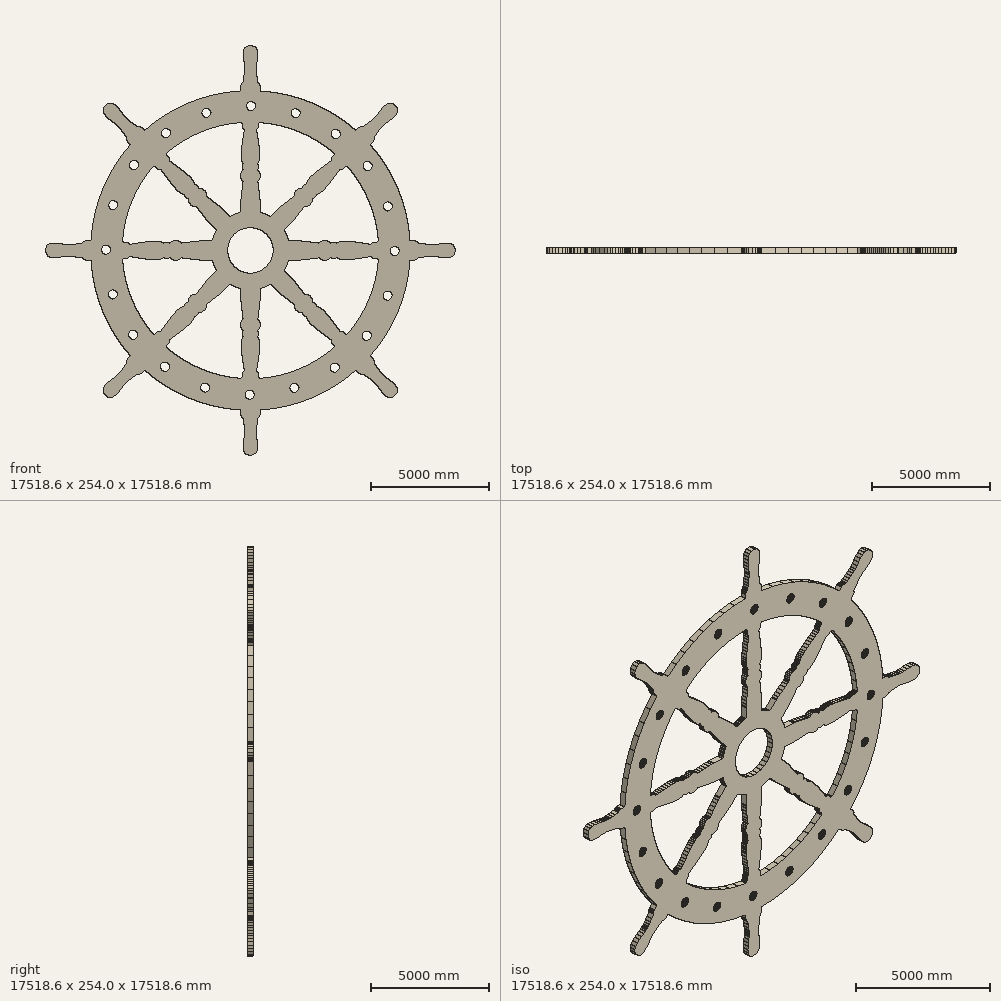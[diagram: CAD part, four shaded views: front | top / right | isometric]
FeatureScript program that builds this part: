
annotation { "Feature Type Name" : "Feature", "Feature Type Description" : "" }
export const myFeature = defineFeature(function(context is Context, id is Id, definition is map)
    precondition{}
    {
        {
            var Q0;
            Q0=qCreatedBy(makeId("Front.planeOp"),FACE);
            var sketch = newSketch(context, id + "F0", { "sketchPlane" : qUnion([Q0])});
            skLineSegment(sketch, "E0", {"start": v(6165.33, -222.67) * mm, "end": v(6126.68, -217.26) * mm});
            skLineSegment(sketch, "E1", {"start": v(6126.68, -217.26) * mm, "end": v(6090.75, -204.87) * mm});
            skLineSegment(sketch, "E2", {"start": v(6090.75, -204.87) * mm, "end": v(6058.31, -186.3) * mm});
            skLineSegment(sketch, "E3", {"start": v(6058.31, -186.3) * mm, "end": v(6030.13, -162.3) * mm});
            skLineSegment(sketch, "E4", {"start": v(6030.13, -162.3) * mm, "end": v(6006.97, -133.67) * mm});
            skLineSegment(sketch, "E5", {"start": v(6006.97, -133.67) * mm, "end": v(5989.6, -101.2) * mm});
            skLineSegment(sketch, "E6", {"start": v(5989.6, -101.2) * mm, "end": v(5978.78, -65.68) * mm});
            skLineSegment(sketch, "E7", {"start": v(5978.78, -65.68) * mm, "end": v(5975.29, -27.88) * mm});
            skLineSegment(sketch, "E8", {"start": v(5975.29, -27.88) * mm, "end": v(5979.97, 9.9) * mm});
            skLineSegment(sketch, "E9", {"start": v(5979.97, 9.9) * mm, "end": v(5991.44, 45.31) * mm});
            skLineSegment(sketch, "E10", {"start": v(5991.44, 45.31) * mm, "end": v(6009.03, 77.59) * mm});
            skLineSegment(sketch, "E11", {"start": v(6009.03, 77.59) * mm, "end": v(6032.1, 105.96) * mm});
            skLineSegment(sketch, "E12", {"start": v(6032.1, 105.96) * mm, "end": v(6060, 129.65) * mm});
            skLineSegment(sketch, "E13", {"start": v(6060, 129.65) * mm, "end": v(6092.04, 147.88) * mm});
            skLineSegment(sketch, "E14", {"start": v(6092.04, 147.88) * mm, "end": v(6127.58, 159.9) * mm});
            skLineSegment(sketch, "E15", {"start": v(6127.58, 159.9) * mm, "end": v(6165.96, 164.9) * mm});
            skLineSegment(sketch, "E16", {"start": v(6165.96, 164.9) * mm, "end": v(6205, 162.05) * mm});
            skLineSegment(sketch, "E17", {"start": v(6205, 162.05) * mm, "end": v(6241.57, 151.48) * mm});
            skLineSegment(sketch, "E18", {"start": v(6241.57, 151.48) * mm, "end": v(6274.8, 134) * mm});
            skLineSegment(sketch, "E19", {"start": v(6274.8, 134) * mm, "end": v(6303.79, 110.38) * mm});
            skLineSegment(sketch, "E20", {"start": v(6303.79, 110.38) * mm, "end": v(6327.65, 81.4) * mm});
            skLineSegment(sketch, "E21", {"start": v(6327.65, 81.4) * mm, "end": v(6345.5, 47.85) * mm});
            skLineSegment(sketch, "E22", {"start": v(6345.5, 47.85) * mm, "end": v(6356.43, 10.5) * mm});
            skLineSegment(sketch, "E23", {"start": v(6356.43, 10.5) * mm, "end": v(6359.56, -29.86) * mm});
            skLineSegment(sketch, "E24", {"start": v(6359.56, -29.86) * mm, "end": v(6355.22, -70.17) * mm});
            skLineSegment(sketch, "E25", {"start": v(6355.22, -70.17) * mm, "end": v(6343.62, -107.4) * mm});
            skLineSegment(sketch, "E26", {"start": v(6343.62, -107.4) * mm, "end": v(6325.54, -140.77) * mm});
            skLineSegment(sketch, "E27", {"start": v(6325.54, -140.77) * mm, "end": v(6301.76, -169.52) * mm});
            skLineSegment(sketch, "E28", {"start": v(6301.76, -169.52) * mm, "end": v(6273.06, -192.85) * mm});
            skLineSegment(sketch, "E29", {"start": v(6273.06, -192.85) * mm, "end": v(6240.24, -210) * mm});
            skLineSegment(sketch, "E30", {"start": v(6240.24, -210) * mm, "end": v(6204.07, -220.2) * mm});
            skLineSegment(sketch, "E31", {"start": v(6204.07, -220.2) * mm, "end": v(6165.33, -222.67) * mm});
            skLineSegment(sketch, "E32", {"start": v(6040.7, -1994.04) * mm, "end": v(6024.87, -2031.33) * mm});
            skLineSegment(sketch, "E33", {"start": v(6024.87, -2031.33) * mm, "end": v(6002.57, -2063.26) * mm});
            skLineSegment(sketch, "E34", {"start": v(6002.57, -2063.26) * mm, "end": v(5974.91, -2089.38) * mm});
            skLineSegment(sketch, "E35", {"start": v(5974.91, -2089.38) * mm, "end": v(5943, -2109.25) * mm});
            skLineSegment(sketch, "E36", {"start": v(5943, -2109.25) * mm, "end": v(5907.94, -2122.4) * mm});
            skLineSegment(sketch, "E37", {"start": v(5907.94, -2122.4) * mm, "end": v(5870.85, -2128.39) * mm});
            skLineSegment(sketch, "E38", {"start": v(5870.85, -2128.39) * mm, "end": v(5832.83, -2126.75) * mm});
            skLineSegment(sketch, "E39", {"start": v(5832.83, -2126.75) * mm, "end": v(5795, -2117.05) * mm});
            skLineSegment(sketch, "E40", {"start": v(5795, -2117.05) * mm, "end": v(5760.14, -2100.05) * mm});
            skLineSegment(sketch, "E41", {"start": v(5760.14, -2100.05) * mm, "end": v(5730.25, -2077.34) * mm});
            skLineSegment(sketch, "E42", {"start": v(5730.25, -2077.34) * mm, "end": v(5705.7, -2049.86) * mm});
            skLineSegment(sketch, "E43", {"start": v(5705.7, -2049.86) * mm, "end": v(5686.86, -2018.55) * mm});
            skLineSegment(sketch, "E44", {"start": v(5686.86, -2018.55) * mm, "end": v(5674.07, -1984.35) * mm});
            skLineSegment(sketch, "E45", {"start": v(5674.07, -1984.35) * mm, "end": v(5667.7, -1948.2) * mm});
            skLineSegment(sketch, "E46", {"start": v(5667.7, -1948.2) * mm, "end": v(5668.14, -1911.01) * mm});
            skLineSegment(sketch, "E47", {"start": v(5668.14, -1911.01) * mm, "end": v(5675.72, -1873.75) * mm});
            skLineSegment(sketch, "E48", {"start": v(5675.72, -1873.75) * mm, "end": v(5691.01, -1839.02) * mm});
            skLineSegment(sketch, "E49", {"start": v(5691.01, -1839.02) * mm, "end": v(5712.57, -1808.8) * mm});
            skLineSegment(sketch, "E50", {"start": v(5712.57, -1808.8) * mm, "end": v(5739.38, -1783.55) * mm});
            skLineSegment(sketch, "E51", {"start": v(5739.38, -1783.55) * mm, "end": v(5770.46, -1763.79) * mm});
            skLineSegment(sketch, "E52", {"start": v(5770.46, -1763.79) * mm, "end": v(5804.81, -1750) * mm});
            skLineSegment(sketch, "E53", {"start": v(5804.81, -1750) * mm, "end": v(5841.44, -1742.66) * mm});
            skLineSegment(sketch, "E54", {"start": v(5841.44, -1742.66) * mm, "end": v(5879.33, -1742.29) * mm});
            skLineSegment(sketch, "E55", {"start": v(5879.33, -1742.29) * mm, "end": v(5917.5, -1749.36) * mm});
            skLineSegment(sketch, "E56", {"start": v(5917.5, -1749.36) * mm, "end": v(5953.66, -1764.05) * mm});
            skLineSegment(sketch, "E57", {"start": v(5953.66, -1764.05) * mm, "end": v(5984.83, -1785.24) * mm});
            skLineSegment(sketch, "E58", {"start": v(5984.83, -1785.24) * mm, "end": v(6010.55, -1811.94) * mm});
            skLineSegment(sketch, "E59", {"start": v(6010.55, -1811.94) * mm, "end": v(6030.34, -1843.18) * mm});
            skLineSegment(sketch, "E60", {"start": v(6030.34, -1843.18) * mm, "end": v(6043.72, -1878) * mm});
            skLineSegment(sketch, "E61", {"start": v(6043.72, -1878) * mm, "end": v(6050.23, -1915.39) * mm});
            skLineSegment(sketch, "E62", {"start": v(6050.23, -1915.39) * mm, "end": v(6049.37, -1954.4) * mm});
            skLineSegment(sketch, "E63", {"start": v(6049.37, -1954.4) * mm, "end": v(6040.7, -1994.04) * mm});
            skLineSegment(sketch, "E64", {"start": v(5397.18, 330.57) * mm, "end": v(5367.67, 344) * mm});
            skLineSegment(sketch, "E65", {"start": v(5367.67, 344) * mm, "end": v(5335.19, 351.84) * mm});
            skLineSegment(sketch, "E66", {"start": v(5335.19, 351.84) * mm, "end": v(5301.14, 353.77) * mm});
            skLineSegment(sketch, "E67", {"start": v(5301.14, 353.77) * mm, "end": v(5266.96, 349.46) * mm});
            skLineSegment(sketch, "E68", {"start": v(5266.96, 349.46) * mm, "end": v(5234.05, 338.56) * mm});
            skLineSegment(sketch, "E69", {"start": v(5234.05, 338.56) * mm, "end": v(5203.85, 320.72) * mm});
            skLineSegment(sketch, "E70", {"start": v(5203.85, 320.72) * mm, "end": v(5177.77, 295.63) * mm});
            skLineSegment(sketch, "E71", {"start": v(5177.77, 295.63) * mm, "end": v(5157.23, 262.93) * mm});
            skLineSegment(sketch, "E72", {"start": v(5157.23, 262.93) * mm, "end": v(5077.23, 273.12) * mm});
            skLineSegment(sketch, "E73", {"start": v(5077.23, 273.12) * mm, "end": v(4981.6, 288) * mm});
            skLineSegment(sketch, "E74", {"start": v(4981.6, 288) * mm, "end": v(4872.77, 306.01) * mm});
            skLineSegment(sketch, "E75", {"start": v(4872.77, 306.01) * mm, "end": v(4753.25, 325.62) * mm});
            skLineSegment(sketch, "E76", {"start": v(4753.25, 325.62) * mm, "end": v(4625.5, 345.3) * mm});
            skLineSegment(sketch, "E77", {"start": v(4625.5, 345.3) * mm, "end": v(4491.98, 363.47) * mm});
            skLineSegment(sketch, "E78", {"start": v(4491.98, 363.47) * mm, "end": v(4355.17, 378.63) * mm});
            skLineSegment(sketch, "E79", {"start": v(4355.17, 378.63) * mm, "end": v(4217.53, 389.22) * mm});
            skLineSegment(sketch, "E80", {"start": v(4217.53, 389.22) * mm, "end": v(4132.41, 393.71) * mm});
            skLineSegment(sketch, "E81", {"start": v(4132.41, 393.71) * mm, "end": v(4054.2, 396.17) * mm});
            skLineSegment(sketch, "E82", {"start": v(4054.2, 396.17) * mm, "end": v(3982.82, 395.69) * mm});
            skLineSegment(sketch, "E83", {"start": v(3982.82, 395.69) * mm, "end": v(3918.18, 391.33) * mm});
            skLineSegment(sketch, "E84", {"start": v(3918.18, 391.33) * mm, "end": v(3860.2, 382.17) * mm});
            skLineSegment(sketch, "E85", {"start": v(3860.2, 382.17) * mm, "end": v(3808.8, 367.3) * mm});
            skLineSegment(sketch, "E86", {"start": v(3808.8, 367.3) * mm, "end": v(3763.9, 345.8) * mm});
            skLineSegment(sketch, "E87", {"start": v(3763.9, 345.8) * mm, "end": v(3725.4, 316.73) * mm});
            skLineSegment(sketch, "E88", {"start": v(3725.4, 316.73) * mm, "end": v(3697.85, 284.72) * mm});
            skLineSegment(sketch, "E89", {"start": v(3697.85, 284.72) * mm, "end": v(3671.26, 314.52) * mm});
            skLineSegment(sketch, "E90", {"start": v(3671.26, 314.52) * mm, "end": v(3639.37, 335.7) * mm});
            skLineSegment(sketch, "E91", {"start": v(3639.37, 335.7) * mm, "end": v(3603.92, 348.64) * mm});
            skLineSegment(sketch, "E92", {"start": v(3603.92, 348.64) * mm, "end": v(3566.66, 353.65) * mm});
            skLineSegment(sketch, "E93", {"start": v(3566.66, 353.65) * mm, "end": v(3529.36, 351.09) * mm});
            skLineSegment(sketch, "E94", {"start": v(3529.36, 351.09) * mm, "end": v(3493.75, 341.3) * mm});
            skLineSegment(sketch, "E95", {"start": v(3493.75, 341.3) * mm, "end": v(3461.59, 324.61) * mm});
            skLineSegment(sketch, "E96", {"start": v(3461.59, 324.61) * mm, "end": v(3434.63, 301.38) * mm});
            skLineSegment(sketch, "E97", {"start": v(3434.63, 301.38) * mm, "end": v(3386.15, 355.66) * mm});
            skLineSegment(sketch, "E98", {"start": v(3386.15, 355.66) * mm, "end": v(3327.83, 394.55) * mm});
            skLineSegment(sketch, "E99", {"start": v(3327.83, 394.55) * mm, "end": v(3262.94, 418.1) * mm});
            skLineSegment(sketch, "E100", {"start": v(3262.94, 418.1) * mm, "end": v(3194.72, 426.34) * mm});
            skLineSegment(sketch, "E101", {"start": v(3194.72, 426.34) * mm, "end": v(3126.42, 419.32) * mm});
            skLineSegment(sketch, "E102", {"start": v(3126.42, 419.32) * mm, "end": v(3061.29, 397.08) * mm});
            skLineSegment(sketch, "E103", {"start": v(3061.29, 397.08) * mm, "end": v(3002.58, 359.67) * mm});
            skLineSegment(sketch, "E104", {"start": v(3002.58, 359.67) * mm, "end": v(2953.55, 307.12) * mm});
            skLineSegment(sketch, "E105", {"start": v(2953.55, 307.12) * mm, "end": v(2912.72, 316.6) * mm});
            skLineSegment(sketch, "E106", {"start": v(2912.72, 316.6) * mm, "end": v(2815.67, 330.94) * mm});
            skLineSegment(sketch, "E107", {"start": v(2815.67, 330.94) * mm, "end": v(2681.25, 348.26) * mm});
            skLineSegment(sketch, "E108", {"start": v(2681.25, 348.26) * mm, "end": v(2528.3, 366.67) * mm});
            skLineSegment(sketch, "E109", {"start": v(2528.3, 366.67) * mm, "end": v(2375.69, 384.28) * mm});
            skLineSegment(sketch, "E110", {"start": v(2375.69, 384.28) * mm, "end": v(2242.25, 399.2) * mm});
            skLineSegment(sketch, "E111", {"start": v(2242.25, 399.2) * mm, "end": v(2146.85, 409.53) * mm});
            skLineSegment(sketch, "E112", {"start": v(2146.85, 409.53) * mm, "end": v(2108.31, 413.4) * mm});
            skLineSegment(sketch, "E113", {"start": v(2108.31, 413.4) * mm, "end": v(1632.95, 413.4) * mm});
            skLineSegment(sketch, "E114", {"start": v(1632.95, 413.4) * mm, "end": v(1616.76, 472.95) * mm});
            skLineSegment(sketch, "E115", {"start": v(1616.76, 472.95) * mm, "end": v(1598.48, 531.58) * mm});
            skLineSegment(sketch, "E116", {"start": v(1598.48, 531.58) * mm, "end": v(1578.16, 589.26) * mm});
            skLineSegment(sketch, "E117", {"start": v(1578.16, 589.26) * mm, "end": v(1555.84, 645.95) * mm});
            skLineSegment(sketch, "E118", {"start": v(1555.84, 645.95) * mm, "end": v(1531.54, 701.62) * mm});
            skLineSegment(sketch, "E119", {"start": v(1531.54, 701.62) * mm, "end": v(1505.3, 756.22) * mm});
            skLineSegment(sketch, "E120", {"start": v(1505.3, 756.22) * mm, "end": v(1477.18, 809.72) * mm});
            skLineSegment(sketch, "E121", {"start": v(1477.18, 809.72) * mm, "end": v(1447.18, 862.09) * mm});
            skLineSegment(sketch, "E122", {"start": v(1447.18, 862.09) * mm, "end": v(1783.35, 1198.26) * mm});
            skLineSegment(sketch, "E123", {"start": v(1783.35, 1198.26) * mm, "end": v(1807.94, 1228.36) * mm});
            skLineSegment(sketch, "E124", {"start": v(1807.94, 1228.36) * mm, "end": v(1868.11, 1303.26) * mm});
            skLineSegment(sketch, "E125", {"start": v(1868.11, 1303.26) * mm, "end": v(1951.9, 1408.28) * mm});
            skLineSegment(sketch, "E126", {"start": v(1951.9, 1408.28) * mm, "end": v(2047.3, 1528.73) * mm});
            skLineSegment(sketch, "E127", {"start": v(2047.3, 1528.73) * mm, "end": v(2142.36, 1649.94) * mm});
            skLineSegment(sketch, "E128", {"start": v(2142.36, 1649.94) * mm, "end": v(2225.1, 1757.23) * mm});
            skLineSegment(sketch, "E129", {"start": v(2225.1, 1757.23) * mm, "end": v(2283.54, 1835.91) * mm});
            skLineSegment(sketch, "E130", {"start": v(2283.54, 1835.91) * mm, "end": v(2305.7, 1871.3) * mm});
            skLineSegment(sketch, "E131", {"start": v(2305.7, 1871.3) * mm, "end": v(2377.28, 1868.88) * mm});
            skLineSegment(sketch, "E132", {"start": v(2377.28, 1868.88) * mm, "end": v(2445.15, 1883.9) * mm});
            skLineSegment(sketch, "E133", {"start": v(2445.15, 1883.9) * mm, "end": v(2506.94, 1914.13) * mm});
            skLineSegment(sketch, "E134", {"start": v(2506.94, 1914.13) * mm, "end": v(2560.27, 1957.35) * mm});
            skLineSegment(sketch, "E135", {"start": v(2560.27, 1957.35) * mm, "end": v(2602.78, 2011.34) * mm});
            skLineSegment(sketch, "E136", {"start": v(2602.78, 2011.34) * mm, "end": v(2632.1, 2073.87) * mm});
            skLineSegment(sketch, "E137", {"start": v(2632.1, 2073.87) * mm, "end": v(2645.85, 2142.7) * mm});
            skLineSegment(sketch, "E138", {"start": v(2645.85, 2142.7) * mm, "end": v(2641.66, 2215.63) * mm});
            skLineSegment(sketch, "E139", {"start": v(2641.66, 2215.63) * mm, "end": v(2677.56, 2218.4) * mm});
            skLineSegment(sketch, "E140", {"start": v(2677.56, 2218.4) * mm, "end": v(2712.27, 2229.58) * mm});
            skLineSegment(sketch, "E141", {"start": v(2712.27, 2229.58) * mm, "end": v(2744.37, 2248.12) * mm});
            skLineSegment(sketch, "E142", {"start": v(2744.37, 2248.12) * mm, "end": v(2772.44, 2272.94) * mm});
            skLineSegment(sketch, "E143", {"start": v(2772.44, 2272.94) * mm, "end": v(2795.04, 2302.98) * mm});
            skLineSegment(sketch, "E144", {"start": v(2795.04, 2302.98) * mm, "end": v(2810.75, 2337.17) * mm});
            skLineSegment(sketch, "E145", {"start": v(2810.75, 2337.17) * mm, "end": v(2818.15, 2374.44) * mm});
            skLineSegment(sketch, "E146", {"start": v(2818.15, 2374.44) * mm, "end": v(2815.8, 2413.72) * mm});
            skLineSegment(sketch, "E147", {"start": v(2815.8, 2413.72) * mm, "end": v(2858.15, 2410.4) * mm});
            skLineSegment(sketch, "E148", {"start": v(2858.15, 2410.4) * mm, "end": v(2905.94, 2417.03) * mm});
            skLineSegment(sketch, "E149", {"start": v(2905.94, 2417.03) * mm, "end": v(2952.9, 2433.57) * mm});
            skLineSegment(sketch, "E150", {"start": v(2952.9, 2433.57) * mm, "end": v(2999.76, 2459.4) * mm});
            skLineSegment(sketch, "E151", {"start": v(2999.76, 2459.4) * mm, "end": v(3047.22, 2493.93) * mm});
            skLineSegment(sketch, "E152", {"start": v(3047.22, 2493.93) * mm, "end": v(3096, 2536.56) * mm});
            skLineSegment(sketch, "E153", {"start": v(3096, 2536.56) * mm, "end": v(3146.82, 2586.68) * mm});
            skLineSegment(sketch, "E154", {"start": v(3146.82, 2586.68) * mm, "end": v(3200.41, 2643.7) * mm});
            skLineSegment(sketch, "E155", {"start": v(3200.41, 2643.7) * mm, "end": v(3257.49, 2707) * mm});
            skLineSegment(sketch, "E156", {"start": v(3257.49, 2707) * mm, "end": v(3347.23, 2811.91) * mm});
            skLineSegment(sketch, "E157", {"start": v(3347.23, 2811.91) * mm, "end": v(3433.2, 2919.44) * mm});
            skLineSegment(sketch, "E158", {"start": v(3433.2, 2919.44) * mm, "end": v(3514.72, 3026.74) * mm});
            skLineSegment(sketch, "E159", {"start": v(3514.72, 3026.74) * mm, "end": v(3591.15, 3131) * mm});
            skLineSegment(sketch, "E160", {"start": v(3591.15, 3131) * mm, "end": v(3661.81, 3229.35) * mm});
            skLineSegment(sketch, "E161", {"start": v(3661.81, 3229.35) * mm, "end": v(3726.06, 3319) * mm});
            skLineSegment(sketch, "E162", {"start": v(3726.06, 3319) * mm, "end": v(3783.22, 3397.08) * mm});
            skLineSegment(sketch, "E163", {"start": v(3783.22, 3397.08) * mm, "end": v(3832.64, 3460.79) * mm});
            skLineSegment(sketch, "E164", {"start": v(3832.64, 3460.79) * mm, "end": v(3870.51, 3452.18) * mm});
            skLineSegment(sketch, "E165", {"start": v(3870.51, 3452.18) * mm, "end": v(3906.84, 3453) * mm});
            skLineSegment(sketch, "E166", {"start": v(3906.84, 3453) * mm, "end": v(3940.88, 3461.94) * mm});
            skLineSegment(sketch, "E167", {"start": v(3940.88, 3461.94) * mm, "end": v(3971.86, 3477.7) * mm});
            skLineSegment(sketch, "E168", {"start": v(3971.86, 3477.7) * mm, "end": v(3999.04, 3498.95) * mm});
            skLineSegment(sketch, "E169", {"start": v(3999.04, 3498.95) * mm, "end": v(4021.65, 3524.4) * mm});
            skLineSegment(sketch, "E170", {"start": v(4021.65, 3524.4) * mm, "end": v(4038.94, 3552.72) * mm});
            skLineSegment(sketch, "E171", {"start": v(4038.94, 3552.72) * mm, "end": v(4050.14, 3582.63) * mm});
            skLineSegment(sketch, "E172", {"start": v(4050.14, 3582.63) * mm, "end": v(4062.27, 3578.85) * mm});
            skLineSegment(sketch, "E173", {"start": v(4062.27, 3578.85) * mm, "end": v(4074.6, 3576.1) * mm});
            skLineSegment(sketch, "E174", {"start": v(4074.6, 3576.1) * mm, "end": v(4087.07, 3574.34) * mm});
            skLineSegment(sketch, "E175", {"start": v(4087.07, 3574.34) * mm, "end": v(4099.64, 3573.56) * mm});
            skLineSegment(sketch, "E176", {"start": v(4099.64, 3573.56) * mm, "end": v(4112.24, 3573.74) * mm});
            skLineSegment(sketch, "E177", {"start": v(4112.24, 3573.74) * mm, "end": v(4124.83, 3574.86) * mm});
            skLineSegment(sketch, "E178", {"start": v(4124.83, 3574.86) * mm, "end": v(4137.35, 3576.88) * mm});
            skLineSegment(sketch, "E179", {"start": v(4137.35, 3576.88) * mm, "end": v(4149.74, 3579.79) * mm});
            skLineSegment(sketch, "E180", {"start": v(4149.74, 3579.79) * mm, "end": v(4417.16, 3244.49) * mm});
            skLineSegment(sketch, "E181", {"start": v(4417.16, 3244.49) * mm, "end": v(4658.11, 2888.58) * mm});
            skLineSegment(sketch, "E182", {"start": v(4658.11, 2888.58) * mm, "end": v(4871.13, 2513.54) * mm});
            skLineSegment(sketch, "E183", {"start": v(4871.13, 2513.54) * mm, "end": v(5054.73, 2120.85) * mm});
            skLineSegment(sketch, "E184", {"start": v(5054.73, 2120.85) * mm, "end": v(5207.44, 1711.98) * mm});
            skLineSegment(sketch, "E185", {"start": v(5207.44, 1711.98) * mm, "end": v(5327.78, 1288.4) * mm});
            skLineSegment(sketch, "E186", {"start": v(5327.78, 1288.4) * mm, "end": v(5414.28, 851.6) * mm});
            skLineSegment(sketch, "E187", {"start": v(5414.28, 851.6) * mm, "end": v(5465.46, 403.06) * mm});
            skLineSegment(sketch, "E188", {"start": v(5465.46, 403.06) * mm, "end": v(5454.66, 396.39) * mm});
            skLineSegment(sketch, "E189", {"start": v(5454.66, 396.39) * mm, "end": v(5444.4, 388.99) * mm});
            skLineSegment(sketch, "E190", {"start": v(5444.4, 388.99) * mm, "end": v(5434.73, 380.9) * mm});
            skLineSegment(sketch, "E191", {"start": v(5434.73, 380.9) * mm, "end": v(5425.7, 372.11) * mm});
            skLineSegment(sketch, "E192", {"start": v(5425.7, 372.11) * mm, "end": v(5417.39, 362.67) * mm});
            skLineSegment(sketch, "E193", {"start": v(5417.39, 362.67) * mm, "end": v(5409.83, 352.58) * mm});
            skLineSegment(sketch, "E194", {"start": v(5409.83, 352.58) * mm, "end": v(5403.07, 341.88) * mm});
            skLineSegment(sketch, "E195", {"start": v(5403.07, 341.88) * mm, "end": v(5397.18, 330.57) * mm});
            skLineSegment(sketch, "E196", {"start": v(4149.69, -3579.66) * mm, "end": v(4137.33, -3576.74) * mm});
            skLineSegment(sketch, "E197", {"start": v(4137.33, -3576.74) * mm, "end": v(4124.84, -3574.72) * mm});
            skLineSegment(sketch, "E198", {"start": v(4124.84, -3574.72) * mm, "end": v(4112.27, -3573.6) * mm});
            skLineSegment(sketch, "E199", {"start": v(4112.27, -3573.6) * mm, "end": v(4099.67, -3573.43) * mm});
            skLineSegment(sketch, "E200", {"start": v(4099.67, -3573.43) * mm, "end": v(4087.11, -3574.22) * mm});
            skLineSegment(sketch, "E201", {"start": v(4087.11, -3574.22) * mm, "end": v(4074.63, -3576) * mm});
            skLineSegment(sketch, "E202", {"start": v(4074.63, -3576) * mm, "end": v(4062.28, -3578.8) * mm});
            skLineSegment(sketch, "E203", {"start": v(4062.28, -3578.8) * mm, "end": v(4050.12, -3582.63) * mm});
            skLineSegment(sketch, "E204", {"start": v(4050.12, -3582.63) * mm, "end": v(4038.75, -3552.27) * mm});
            skLineSegment(sketch, "E205", {"start": v(4038.75, -3552.27) * mm, "end": v(4021.33, -3523.75) * mm});
            skLineSegment(sketch, "E206", {"start": v(4021.33, -3523.75) * mm, "end": v(3998.63, -3498.31) * mm});
            skLineSegment(sketch, "E207", {"start": v(3998.63, -3498.31) * mm, "end": v(3971.4, -3477.2) * mm});
            skLineSegment(sketch, "E208", {"start": v(3971.4, -3477.2) * mm, "end": v(3940.42, -3461.63) * mm});
            skLineSegment(sketch, "E209", {"start": v(3940.42, -3461.63) * mm, "end": v(3906.45, -3452.89) * mm});
            skLineSegment(sketch, "E210", {"start": v(3906.45, -3452.89) * mm, "end": v(3870.26, -3452.2) * mm});
            skLineSegment(sketch, "E211", {"start": v(3870.26, -3452.2) * mm, "end": v(3832.62, -3460.79) * mm});
            skLineSegment(sketch, "E212", {"start": v(3832.62, -3460.79) * mm, "end": v(3783.27, -3397.01) * mm});
            skLineSegment(sketch, "E213", {"start": v(3783.27, -3397.01) * mm, "end": v(3726.16, -3318.87) * mm});
            skLineSegment(sketch, "E214", {"start": v(3726.16, -3318.87) * mm, "end": v(3661.96, -3229.18) * mm});
            skLineSegment(sketch, "E215", {"start": v(3661.96, -3229.18) * mm, "end": v(3591.31, -3130.8) * mm});
            skLineSegment(sketch, "E216", {"start": v(3591.31, -3130.8) * mm, "end": v(3514.88, -3026.56) * mm});
            skLineSegment(sketch, "E217", {"start": v(3514.88, -3026.56) * mm, "end": v(3433.33, -2919.3) * mm});
            skLineSegment(sketch, "E218", {"start": v(3433.33, -2919.3) * mm, "end": v(3347.3, -2811.83) * mm});
            skLineSegment(sketch, "E219", {"start": v(3347.3, -2811.83) * mm, "end": v(3257.46, -2707.02) * mm});
            skLineSegment(sketch, "E220", {"start": v(3257.46, -2707.02) * mm, "end": v(3200.45, -2643.66) * mm});
            skLineSegment(sketch, "E221", {"start": v(3200.45, -2643.66) * mm, "end": v(3146.88, -2586.61) * mm});
            skLineSegment(sketch, "E222", {"start": v(3146.88, -2586.61) * mm, "end": v(3096.07, -2536.48) * mm});
            skLineSegment(sketch, "E223", {"start": v(3096.07, -2536.48) * mm, "end": v(3047.28, -2493.86) * mm});
            skLineSegment(sketch, "E224", {"start": v(3047.28, -2493.86) * mm, "end": v(2999.8, -2459.34) * mm});
            skLineSegment(sketch, "E225", {"start": v(2999.8, -2459.34) * mm, "end": v(2952.94, -2433.51) * mm});
            skLineSegment(sketch, "E226", {"start": v(2952.94, -2433.51) * mm, "end": v(2905.98, -2416.97) * mm});
            skLineSegment(sketch, "E227", {"start": v(2905.98, -2416.97) * mm, "end": v(2858.2, -2410.32) * mm});
            skLineSegment(sketch, "E228", {"start": v(2858.2, -2410.32) * mm, "end": v(2816.09, -2413.44) * mm});
            skLineSegment(sketch, "E229", {"start": v(2816.09, -2413.44) * mm, "end": v(2818.36, -2373.57) * mm});
            skLineSegment(sketch, "E230", {"start": v(2818.36, -2373.57) * mm, "end": v(2810.8, -2336.03) * mm});
            skLineSegment(sketch, "E231", {"start": v(2810.8, -2336.03) * mm, "end": v(2794.87, -2301.82) * mm});
            skLineSegment(sketch, "E232", {"start": v(2794.87, -2301.82) * mm, "end": v(2772.07, -2271.93) * mm});
            skLineSegment(sketch, "E233", {"start": v(2772.07, -2271.93) * mm, "end": v(2743.88, -2247.36) * mm});
            skLineSegment(sketch, "E234", {"start": v(2743.88, -2247.36) * mm, "end": v(2711.78, -2229.1) * mm});
            skLineSegment(sketch, "E235", {"start": v(2711.78, -2229.1) * mm, "end": v(2677.25, -2218.16) * mm});
            skLineSegment(sketch, "E236", {"start": v(2677.25, -2218.16) * mm, "end": v(2641.77, -2215.53) * mm});
            skLineSegment(sketch, "E237", {"start": v(2641.77, -2215.53) * mm, "end": v(2645.86, -2142.87) * mm});
            skLineSegment(sketch, "E238", {"start": v(2645.86, -2142.87) * mm, "end": v(2632.13, -2074.14) * mm});
            skLineSegment(sketch, "E239", {"start": v(2632.13, -2074.14) * mm, "end": v(2602.9, -2011.6) * mm});
            skLineSegment(sketch, "E240", {"start": v(2602.9, -2011.6) * mm, "end": v(2560.48, -1957.53) * mm});
            skLineSegment(sketch, "E241", {"start": v(2560.48, -1957.53) * mm, "end": v(2507.22, -1914.2) * mm});
            skLineSegment(sketch, "E242", {"start": v(2507.22, -1914.2) * mm, "end": v(2445.44, -1883.87) * mm});
            skLineSegment(sketch, "E243", {"start": v(2445.44, -1883.87) * mm, "end": v(2377.47, -1868.82) * mm});
            skLineSegment(sketch, "E244", {"start": v(2377.47, -1868.82) * mm, "end": v(2305.65, -1871.3) * mm});
            skLineSegment(sketch, "E245", {"start": v(2305.65, -1871.3) * mm, "end": v(2283.47, -1835.73) * mm});
            skLineSegment(sketch, "E246", {"start": v(2283.47, -1835.73) * mm, "end": v(2224.98, -1756.96) * mm});
            skLineSegment(sketch, "E247", {"start": v(2224.98, -1756.96) * mm, "end": v(2142.17, -1649.66) * mm});
            skLineSegment(sketch, "E248", {"start": v(2142.17, -1649.66) * mm, "end": v(2047.04, -1528.5) * mm});
            skLineSegment(sketch, "E249", {"start": v(2047.04, -1528.5) * mm, "end": v(1951.58, -1408.13) * mm});
            skLineSegment(sketch, "E250", {"start": v(1951.58, -1408.13) * mm, "end": v(1867.77, -1303.24) * mm});
            skLineSegment(sketch, "E251", {"start": v(1867.77, -1303.24) * mm, "end": v(1807.62, -1228.47) * mm});
            skLineSegment(sketch, "E252", {"start": v(1807.62, -1228.47) * mm, "end": v(1783.12, -1198.49) * mm});
            skLineSegment(sketch, "E253", {"start": v(1783.12, -1198.49) * mm, "end": v(1446.97, -862.37) * mm});
            skLineSegment(sketch, "E254", {"start": v(1446.97, -862.37) * mm, "end": v(1476.99, -810) * mm});
            skLineSegment(sketch, "E255", {"start": v(1476.99, -810) * mm, "end": v(1505.14, -756.5) * mm});
            skLineSegment(sketch, "E256", {"start": v(1505.14, -756.5) * mm, "end": v(1531.38, -701.9) * mm});
            skLineSegment(sketch, "E257", {"start": v(1531.38, -701.9) * mm, "end": v(1555.69, -646.25) * mm});
            skLineSegment(sketch, "E258", {"start": v(1555.69, -646.25) * mm, "end": v(1578.02, -589.57) * mm});
            skLineSegment(sketch, "E259", {"start": v(1578.02, -589.57) * mm, "end": v(1598.35, -531.9) * mm});
            skLineSegment(sketch, "E260", {"start": v(1598.35, -531.9) * mm, "end": v(1616.64, -473.27) * mm});
            skLineSegment(sketch, "E261", {"start": v(1616.64, -473.27) * mm, "end": v(1632.85, -413.73) * mm});
            skLineSegment(sketch, "E262", {"start": v(1632.85, -413.73) * mm, "end": v(2108.31, -413.73) * mm});
            skLineSegment(sketch, "E263", {"start": v(2108.31, -413.73) * mm, "end": v(2146.99, -409.83) * mm});
            skLineSegment(sketch, "E264", {"start": v(2146.99, -409.83) * mm, "end": v(2242.5, -399.42) * mm});
            skLineSegment(sketch, "E265", {"start": v(2242.5, -399.42) * mm, "end": v(2376, -384.4) * mm});
            skLineSegment(sketch, "E266", {"start": v(2376, -384.4) * mm, "end": v(2528.63, -366.7) * mm});
            skLineSegment(sketch, "E267", {"start": v(2528.63, -366.7) * mm, "end": v(2681.55, -348.2) * mm});
            skLineSegment(sketch, "E268", {"start": v(2681.55, -348.2) * mm, "end": v(2815.9, -330.84) * mm});
            skLineSegment(sketch, "E269", {"start": v(2815.9, -330.84) * mm, "end": v(2912.86, -316.53) * mm});
            skLineSegment(sketch, "E270", {"start": v(2912.86, -316.53) * mm, "end": v(2953.55, -307.17) * mm});
            skLineSegment(sketch, "E271", {"start": v(2953.55, -307.17) * mm, "end": v(3002.46, -359.5) * mm});
            skLineSegment(sketch, "E272", {"start": v(3002.46, -359.5) * mm, "end": v(3061.07, -396.87) * mm});
            skLineSegment(sketch, "E273", {"start": v(3061.07, -396.87) * mm, "end": v(3126.15, -419.18) * mm});
            skLineSegment(sketch, "E274", {"start": v(3126.15, -419.18) * mm, "end": v(3194.43, -426.33) * mm});
            skLineSegment(sketch, "E275", {"start": v(3194.43, -426.33) * mm, "end": v(3262.67, -418.21) * mm});
            skLineSegment(sketch, "E276", {"start": v(3262.67, -418.21) * mm, "end": v(3327.62, -394.73) * mm});
            skLineSegment(sketch, "E277", {"start": v(3327.62, -394.73) * mm, "end": v(3386.02, -355.78) * mm});
            skLineSegment(sketch, "E278", {"start": v(3386.02, -355.78) * mm, "end": v(3434.63, -301.26) * mm});
            skLineSegment(sketch, "E279", {"start": v(3434.63, -301.26) * mm, "end": v(3461.96, -324.68) * mm});
            skLineSegment(sketch, "E280", {"start": v(3461.96, -324.68) * mm, "end": v(3494.42, -341.31) * mm});
            skLineSegment(sketch, "E281", {"start": v(3494.42, -341.31) * mm, "end": v(3530.22, -350.9) * mm});
            skLineSegment(sketch, "E282", {"start": v(3530.22, -350.9) * mm, "end": v(3567.62, -353.2) * mm});
            skLineSegment(sketch, "E283", {"start": v(3567.62, -353.2) * mm, "end": v(3604.84, -347.93) * mm});
            skLineSegment(sketch, "E284", {"start": v(3604.84, -347.93) * mm, "end": v(3640.13, -334.87) * mm});
            skLineSegment(sketch, "E285", {"start": v(3640.13, -334.87) * mm, "end": v(3671.72, -313.75) * mm});
            skLineSegment(sketch, "E286", {"start": v(3671.72, -313.75) * mm, "end": v(3697.85, -284.31) * mm});
            skLineSegment(sketch, "E287", {"start": v(3697.85, -284.31) * mm, "end": v(3725.4, -316.6) * mm});
            skLineSegment(sketch, "E288", {"start": v(3725.4, -316.6) * mm, "end": v(3763.9, -345.7) * mm});
            skLineSegment(sketch, "E289", {"start": v(3763.9, -345.7) * mm, "end": v(3808.8, -367.23) * mm});
            skLineSegment(sketch, "E290", {"start": v(3808.8, -367.23) * mm, "end": v(3860.2, -382.09) * mm});
            skLineSegment(sketch, "E291", {"start": v(3860.2, -382.09) * mm, "end": v(3918.18, -391.23) * mm});
            skLineSegment(sketch, "E292", {"start": v(3918.18, -391.23) * mm, "end": v(3982.82, -395.58) * mm});
            skLineSegment(sketch, "E293", {"start": v(3982.82, -395.58) * mm, "end": v(4054.2, -396.08) * mm});
            skLineSegment(sketch, "E294", {"start": v(4054.2, -396.08) * mm, "end": v(4132.41, -393.66) * mm});
            skLineSegment(sketch, "E295", {"start": v(4132.41, -393.66) * mm, "end": v(4217.53, -389.24) * mm});
            skLineSegment(sketch, "E296", {"start": v(4217.53, -389.24) * mm, "end": v(4355.17, -378.52) * mm});
            skLineSegment(sketch, "E297", {"start": v(4355.17, -378.52) * mm, "end": v(4491.98, -363.28) * mm});
            skLineSegment(sketch, "E298", {"start": v(4491.98, -363.28) * mm, "end": v(4625.5, -345.05) * mm});
            skLineSegment(sketch, "E299", {"start": v(4625.5, -345.05) * mm, "end": v(4753.25, -325.38) * mm});
            skLineSegment(sketch, "E300", {"start": v(4753.25, -325.38) * mm, "end": v(4872.77, -305.8) * mm});
            skLineSegment(sketch, "E301", {"start": v(4872.77, -305.8) * mm, "end": v(4981.6, -287.85) * mm});
            skLineSegment(sketch, "E302", {"start": v(4981.6, -287.85) * mm, "end": v(5077.23, -273.05) * mm});
            skLineSegment(sketch, "E303", {"start": v(5077.23, -273.05) * mm, "end": v(5157.23, -262.95) * mm});
            skLineSegment(sketch, "E304", {"start": v(5157.23, -262.95) * mm, "end": v(5177.92, -295.8) * mm});
            skLineSegment(sketch, "E305", {"start": v(5177.92, -295.8) * mm, "end": v(5204.19, -320.91) * mm});
            skLineSegment(sketch, "E306", {"start": v(5204.19, -320.91) * mm, "end": v(5234.58, -338.66) * mm});
            skLineSegment(sketch, "E307", {"start": v(5234.58, -338.66) * mm, "end": v(5267.62, -349.43) * mm});
            skLineSegment(sketch, "E308", {"start": v(5267.62, -349.43) * mm, "end": v(5301.87, -353.62) * mm});
            skLineSegment(sketch, "E309", {"start": v(5301.87, -353.62) * mm, "end": v(5335.85, -351.61) * mm});
            skLineSegment(sketch, "E310", {"start": v(5335.85, -351.61) * mm, "end": v(5368.1, -343.81) * mm});
            skLineSegment(sketch, "E311", {"start": v(5368.1, -343.81) * mm, "end": v(5397.18, -330.6) * mm});
            skLineSegment(sketch, "E312", {"start": v(5397.18, -330.6) * mm, "end": v(5403.07, -341.82) * mm});
            skLineSegment(sketch, "E313", {"start": v(5403.07, -341.82) * mm, "end": v(5409.83, -352.47) * mm});
            skLineSegment(sketch, "E314", {"start": v(5409.83, -352.47) * mm, "end": v(5417.39, -362.51) * mm});
            skLineSegment(sketch, "E315", {"start": v(5417.39, -362.51) * mm, "end": v(5425.7, -371.94) * mm});
            skLineSegment(sketch, "E316", {"start": v(5425.7, -371.94) * mm, "end": v(5434.73, -380.72) * mm});
            skLineSegment(sketch, "E317", {"start": v(5434.73, -380.72) * mm, "end": v(5444.4, -388.83) * mm});
            skLineSegment(sketch, "E318", {"start": v(5444.4, -388.83) * mm, "end": v(5454.66, -396.25) * mm});
            skLineSegment(sketch, "E319", {"start": v(5454.66, -396.25) * mm, "end": v(5465.46, -402.96) * mm});
            skLineSegment(sketch, "E320", {"start": v(5465.46, -402.96) * mm, "end": v(5414.28, -851.5) * mm});
            skLineSegment(sketch, "E321", {"start": v(5414.28, -851.5) * mm, "end": v(5327.78, -1288.3) * mm});
            skLineSegment(sketch, "E322", {"start": v(5327.78, -1288.3) * mm, "end": v(5207.44, -1711.86) * mm});
            skLineSegment(sketch, "E323", {"start": v(5207.44, -1711.86) * mm, "end": v(5054.73, -2120.73) * mm});
            skLineSegment(sketch, "E324", {"start": v(5054.73, -2120.73) * mm, "end": v(4871.12, -2513.41) * mm});
            skLineSegment(sketch, "E325", {"start": v(4871.12, -2513.41) * mm, "end": v(4658.1, -2888.45) * mm});
            skLineSegment(sketch, "E326", {"start": v(4658.1, -2888.45) * mm, "end": v(4417.12, -3244.36) * mm});
            skLineSegment(sketch, "E327", {"start": v(4417.12, -3244.36) * mm, "end": v(4149.69, -3579.66) * mm});
            skLineSegment(sketch, "E328", {"start": v(5129.03, -3763.35) * mm, "end": v(5101.35, -3793.08) * mm});
            skLineSegment(sketch, "E329", {"start": v(5101.35, -3793.08) * mm, "end": v(5069.63, -3816.05) * mm});
            skLineSegment(sketch, "E330", {"start": v(5069.63, -3816.05) * mm, "end": v(5034.98, -3832.12) * mm});
            skLineSegment(sketch, "E331", {"start": v(5034.98, -3832.12) * mm, "end": v(4998.5, -3841.13) * mm});
            skLineSegment(sketch, "E332", {"start": v(4998.5, -3841.13) * mm, "end": v(4961.3, -3842.92) * mm});
            skLineSegment(sketch, "E333", {"start": v(4961.3, -3842.92) * mm, "end": v(4924.46, -3837.33) * mm});
            skLineSegment(sketch, "E334", {"start": v(4924.46, -3837.33) * mm, "end": v(4889.08, -3824.2) * mm});
            skLineSegment(sketch, "E335", {"start": v(4889.08, -3824.2) * mm, "end": v(4856.26, -3803.36) * mm});
            skLineSegment(sketch, "E336", {"start": v(4856.26, -3803.36) * mm, "end": v(4828.24, -3776.28) * mm});
            skLineSegment(sketch, "E337", {"start": v(4828.24, -3776.28) * mm, "end": v(4806.61, -3745.22) * mm});
            skLineSegment(sketch, "E338", {"start": v(4806.61, -3745.22) * mm, "end": v(4791.52, -3711.27) * mm});
            skLineSegment(sketch, "E339", {"start": v(4791.52, -3711.27) * mm, "end": v(4783.12, -3675.5) * mm});
            skLineSegment(sketch, "E340", {"start": v(4783.12, -3675.5) * mm, "end": v(4781.55, -3638.98) * mm});
            skLineSegment(sketch, "E341", {"start": v(4781.55, -3638.98) * mm, "end": v(4786.98, -3602.8) * mm});
            skLineSegment(sketch, "E342", {"start": v(4786.98, -3602.8) * mm, "end": v(4799.55, -3568.04) * mm});
            skLineSegment(sketch, "E343", {"start": v(4799.55, -3568.04) * mm, "end": v(4819.4, -3535.77) * mm});
            skLineSegment(sketch, "E344", {"start": v(4819.4, -3535.77) * mm, "end": v(4844.57, -3507.4) * mm});
            skLineSegment(sketch, "E345", {"start": v(4844.57, -3507.4) * mm, "end": v(4874.07, -3485.09) * mm});
            skLineSegment(sketch, "E346", {"start": v(4874.07, -3485.09) * mm, "end": v(4906.9, -3469.06) * mm});
            skLineSegment(sketch, "E347", {"start": v(4906.9, -3469.06) * mm, "end": v(4942.06, -3459.53) * mm});
            skLineSegment(sketch, "E348", {"start": v(4942.06, -3459.53) * mm, "end": v(4978.5, -3456.74) * mm});
            skLineSegment(sketch, "E349", {"start": v(4978.5, -3456.74) * mm, "end": v(5015.24, -3460.88) * mm});
            skLineSegment(sketch, "E350", {"start": v(5015.24, -3460.88) * mm, "end": v(5051.25, -3472.2) * mm});
            skLineSegment(sketch, "E351", {"start": v(5051.25, -3472.2) * mm, "end": v(5085.52, -3490.91) * mm});
            skLineSegment(sketch, "E352", {"start": v(5085.52, -3490.91) * mm, "end": v(5115.15, -3515.97) * mm});
            skLineSegment(sketch, "E353", {"start": v(5115.15, -3515.97) * mm, "end": v(5138.33, -3545.88) * mm});
            skLineSegment(sketch, "E354", {"start": v(5138.33, -3545.88) * mm, "end": v(5154.84, -3579.5) * mm});
            skLineSegment(sketch, "E355", {"start": v(5154.84, -3579.5) * mm, "end": v(5164.44, -3615.68) * mm});
            skLineSegment(sketch, "E356", {"start": v(5164.44, -3615.68) * mm, "end": v(5166.9, -3653.3) * mm});
            skLineSegment(sketch, "E357", {"start": v(5166.9, -3653.3) * mm, "end": v(5161.97, -3691.22) * mm});
            skLineSegment(sketch, "E358", {"start": v(5161.97, -3691.22) * mm, "end": v(5149.43, -3728.28) * mm});
            skLineSegment(sketch, "E359", {"start": v(5149.43, -3728.28) * mm, "end": v(5129.03, -3763.35) * mm});
            skLineSegment(sketch, "E360", {"start": v(3714.23, -5162.87) * mm, "end": v(3679.52, -5183.73) * mm});
            skLineSegment(sketch, "E361", {"start": v(3679.52, -5183.73) * mm, "end": v(3642.7, -5196.44) * mm});
            skLineSegment(sketch, "E362", {"start": v(3642.7, -5196.44) * mm, "end": v(3604.96, -5201.3) * mm});
            skLineSegment(sketch, "E363", {"start": v(3604.96, -5201.3) * mm, "end": v(3567.45, -5198.59) * mm});
            skLineSegment(sketch, "E364", {"start": v(3567.45, -5198.59) * mm, "end": v(3531.34, -5188.6) * mm});
            skLineSegment(sketch, "E365", {"start": v(3531.34, -5188.6) * mm, "end": v(3497.8, -5171.65) * mm});
            skLineSegment(sketch, "E366", {"start": v(3497.8, -5171.65) * mm, "end": v(3468, -5148.02) * mm});
            skLineSegment(sketch, "E367", {"start": v(3468, -5148.02) * mm, "end": v(3443.1, -5117.99) * mm});
            skLineSegment(sketch, "E368", {"start": v(3443.1, -5117.99) * mm, "end": v(3424.85, -5083.7) * mm});
            skLineSegment(sketch, "E369", {"start": v(3424.85, -5083.7) * mm, "end": v(3413.99, -5047.76) * mm});
            skLineSegment(sketch, "E370", {"start": v(3413.99, -5047.76) * mm, "end": v(3410.27, -5011.1) * mm});
            skLineSegment(sketch, "E371", {"start": v(3410.27, -5011.1) * mm, "end": v(3413.43, -4974.72) * mm});
            skLineSegment(sketch, "E372", {"start": v(3413.43, -4974.72) * mm, "end": v(3423.21, -4939.56) * mm});
            skLineSegment(sketch, "E373", {"start": v(3423.21, -4939.56) * mm, "end": v(3439.34, -4906.6) * mm});
            skLineSegment(sketch, "E374", {"start": v(3439.34, -4906.6) * mm, "end": v(3461.56, -4876.78) * mm});
            skLineSegment(sketch, "E375", {"start": v(3461.56, -4876.78) * mm, "end": v(3489.62, -4851.08) * mm});
            skLineSegment(sketch, "E376", {"start": v(3489.62, -4851.08) * mm, "end": v(3522.4, -4831.95) * mm});
            skLineSegment(sketch, "E377", {"start": v(3522.4, -4831.95) * mm, "end": v(3557.6, -4820.16) * mm});
            skLineSegment(sketch, "E378", {"start": v(3557.6, -4820.16) * mm, "end": v(3594.14, -4815.5) * mm});
            skLineSegment(sketch, "E379", {"start": v(3594.14, -4815.5) * mm, "end": v(3630.91, -4817.77) * mm});
            skLineSegment(sketch, "E380", {"start": v(3630.91, -4817.77) * mm, "end": v(3666.81, -4826.8) * mm});
            skLineSegment(sketch, "E381", {"start": v(3666.81, -4826.8) * mm, "end": v(3700.73, -4842.37) * mm});
            skLineSegment(sketch, "E382", {"start": v(3700.73, -4842.37) * mm, "end": v(3731.58, -4864.3) * mm});
            skLineSegment(sketch, "E383", {"start": v(3731.58, -4864.3) * mm, "end": v(3758.25, -4892.38) * mm});
            skLineSegment(sketch, "E384", {"start": v(3758.25, -4892.38) * mm, "end": v(3778.92, -4925.6) * mm});
            skLineSegment(sketch, "E385", {"start": v(3778.92, -4925.6) * mm, "end": v(3791.72, -4961.1) * mm});
            skLineSegment(sketch, "E386", {"start": v(3791.72, -4961.1) * mm, "end": v(3796.84, -4997.84) * mm});
            skLineSegment(sketch, "E387", {"start": v(3796.84, -4997.84) * mm, "end": v(3794.5, -5034.75) * mm});
            skLineSegment(sketch, "E388", {"start": v(3794.5, -5034.75) * mm, "end": v(3784.86, -5070.77) * mm});
            skLineSegment(sketch, "E389", {"start": v(3784.86, -5070.77) * mm, "end": v(3768.14, -5104.84) * mm});
            skLineSegment(sketch, "E390", {"start": v(3768.14, -5104.84) * mm, "end": v(3744.53, -5135.9) * mm});
            skLineSegment(sketch, "E391", {"start": v(3744.53, -5135.9) * mm, "end": v(3714.23, -5162.87) * mm});
            skLineSegment(sketch, "E392", {"start": v(1937.73, -6060.17) * mm, "end": v(1897.87, -6068.02) * mm});
            skLineSegment(sketch, "E393", {"start": v(1897.87, -6068.02) * mm, "end": v(1858.7, -6068.05) * mm});
            skLineSegment(sketch, "E394", {"start": v(1858.7, -6068.05) * mm, "end": v(1821.23, -6060.76) * mm});
            skLineSegment(sketch, "E395", {"start": v(1821.23, -6060.76) * mm, "end": v(1786.42, -6046.67) * mm});
            skLineSegment(sketch, "E396", {"start": v(1786.42, -6046.67) * mm, "end": v(1755.26, -6026.3) * mm});
            skLineSegment(sketch, "E397", {"start": v(1755.26, -6026.3) * mm, "end": v(1728.72, -6000.16) * mm});
            skLineSegment(sketch, "E398", {"start": v(1728.72, -6000.16) * mm, "end": v(1707.8, -5968.77) * mm});
            skLineSegment(sketch, "E399", {"start": v(1707.8, -5968.77) * mm, "end": v(1693.48, -5932.64) * mm});
            skLineSegment(sketch, "E400", {"start": v(1693.48, -5932.64) * mm, "end": v(1686.7, -5894.25) * mm});
            skLineSegment(sketch, "E401", {"start": v(1686.7, -5894.25) * mm, "end": v(1687.43, -5856.39) * mm});
            skLineSegment(sketch, "E402", {"start": v(1687.43, -5856.39) * mm, "end": v(1695.14, -5820.02) * mm});
            skLineSegment(sketch, "E403", {"start": v(1695.14, -5820.02) * mm, "end": v(1709.33, -5786.1) * mm});
            skLineSegment(sketch, "E404", {"start": v(1709.33, -5786.1) * mm, "end": v(1729.5, -5755.6) * mm});
            skLineSegment(sketch, "E405", {"start": v(1729.5, -5755.6) * mm, "end": v(1755.11, -5729.46) * mm});
            skLineSegment(sketch, "E406", {"start": v(1755.11, -5729.46) * mm, "end": v(1785.68, -5708.67) * mm});
            skLineSegment(sketch, "E407", {"start": v(1785.68, -5708.67) * mm, "end": v(1820.68, -5694.16) * mm});
            skLineSegment(sketch, "E408", {"start": v(1820.68, -5694.16) * mm, "end": v(1857.76, -5686.2) * mm});
            skLineSegment(sketch, "E409", {"start": v(1857.76, -5686.2) * mm, "end": v(1894.76, -5685.56) * mm});
            skLineSegment(sketch, "E410", {"start": v(1894.76, -5685.56) * mm, "end": v(1930.75, -5691.86) * mm});
            skLineSegment(sketch, "E411", {"start": v(1930.75, -5691.86) * mm, "end": v(1964.77, -5704.73) * mm});
            skLineSegment(sketch, "E412", {"start": v(1964.77, -5704.73) * mm, "end": v(1995.9, -5723.78) * mm});
            skLineSegment(sketch, "E413", {"start": v(1995.9, -5723.78) * mm, "end": v(2023.18, -5748.62) * mm});
            skLineSegment(sketch, "E414", {"start": v(2023.18, -5748.62) * mm, "end": v(2045.68, -5778.88) * mm});
            skLineSegment(sketch, "E415", {"start": v(2045.68, -5778.88) * mm, "end": v(2062.47, -5814.17) * mm});
            skLineSegment(sketch, "E416", {"start": v(2062.47, -5814.17) * mm, "end": v(2071.73, -5851.81) * mm});
            skLineSegment(sketch, "E417", {"start": v(2071.73, -5851.81) * mm, "end": v(2072.96, -5889.67) * mm});
            skLineSegment(sketch, "E418", {"start": v(2072.96, -5889.67) * mm, "end": v(2066.62, -5926.66) * mm});
            skLineSegment(sketch, "E419", {"start": v(2066.62, -5926.66) * mm, "end": v(2053.18, -5961.67) * mm});
            skLineSegment(sketch, "E420", {"start": v(2053.18, -5961.67) * mm, "end": v(2033.1, -5993.62) * mm});
            skLineSegment(sketch, "E421", {"start": v(2033.1, -5993.62) * mm, "end": v(2006.86, -6021.42) * mm});
            skLineSegment(sketch, "E422", {"start": v(2006.86, -6021.42) * mm, "end": v(1974.9, -6043.97) * mm});
            skLineSegment(sketch, "E423", {"start": v(1974.9, -6043.97) * mm, "end": v(1937.73, -6060.17) * mm});
            skLineSegment(sketch, "E424", {"start": v(403.06, -5465.48) * mm, "end": v(396.39, -5454.68) * mm});
            skLineSegment(sketch, "E425", {"start": v(396.39, -5454.68) * mm, "end": v(388.99, -5444.4) * mm});
            skLineSegment(sketch, "E426", {"start": v(388.99, -5444.4) * mm, "end": v(380.9, -5434.74) * mm});
            skLineSegment(sketch, "E427", {"start": v(380.9, -5434.74) * mm, "end": v(372.11, -5425.71) * mm});
            skLineSegment(sketch, "E428", {"start": v(372.11, -5425.71) * mm, "end": v(362.67, -5417.4) * mm});
            skLineSegment(sketch, "E429", {"start": v(362.67, -5417.4) * mm, "end": v(352.58, -5409.83) * mm});
            skLineSegment(sketch, "E430", {"start": v(352.58, -5409.83) * mm, "end": v(341.88, -5403.07) * mm});
            skLineSegment(sketch, "E431", {"start": v(341.88, -5403.07) * mm, "end": v(330.57, -5397.18) * mm});
            skLineSegment(sketch, "E432", {"start": v(330.57, -5397.18) * mm, "end": v(344, -5367.67) * mm});
            skLineSegment(sketch, "E433", {"start": v(344, -5367.67) * mm, "end": v(351.84, -5335.18) * mm});
            skLineSegment(sketch, "E434", {"start": v(351.84, -5335.18) * mm, "end": v(353.77, -5301.13) * mm});
            skLineSegment(sketch, "E435", {"start": v(353.77, -5301.13) * mm, "end": v(349.46, -5266.95) * mm});
            skLineSegment(sketch, "E436", {"start": v(349.46, -5266.95) * mm, "end": v(338.55, -5234.04) * mm});
            skLineSegment(sketch, "E437", {"start": v(338.55, -5234.04) * mm, "end": v(320.71, -5203.84) * mm});
            skLineSegment(sketch, "E438", {"start": v(320.71, -5203.84) * mm, "end": v(295.61, -5177.76) * mm});
            skLineSegment(sketch, "E439", {"start": v(295.61, -5177.76) * mm, "end": v(262.9, -5157.23) * mm});
            skLineSegment(sketch, "E440", {"start": v(262.9, -5157.23) * mm, "end": v(273.1, -5077.23) * mm});
            skLineSegment(sketch, "E441", {"start": v(273.1, -5077.23) * mm, "end": v(287.99, -4981.59) * mm});
            skLineSegment(sketch, "E442", {"start": v(287.99, -4981.59) * mm, "end": v(306, -4872.77) * mm});
            skLineSegment(sketch, "E443", {"start": v(306, -4872.77) * mm, "end": v(325.62, -4753.25) * mm});
            skLineSegment(sketch, "E444", {"start": v(325.62, -4753.25) * mm, "end": v(345.29, -4625.5) * mm});
            skLineSegment(sketch, "E445", {"start": v(345.29, -4625.5) * mm, "end": v(363.47, -4491.97) * mm});
            skLineSegment(sketch, "E446", {"start": v(363.47, -4491.97) * mm, "end": v(378.63, -4355.15) * mm});
            skLineSegment(sketch, "E447", {"start": v(378.63, -4355.15) * mm, "end": v(389.22, -4217.5) * mm});
            skLineSegment(sketch, "E448", {"start": v(389.22, -4217.5) * mm, "end": v(393.7, -4132.4) * mm});
            skLineSegment(sketch, "E449", {"start": v(393.7, -4132.4) * mm, "end": v(396.16, -4054.19) * mm});
            skLineSegment(sketch, "E450", {"start": v(396.16, -4054.19) * mm, "end": v(395.68, -3982.8) * mm});
            skLineSegment(sketch, "E451", {"start": v(395.68, -3982.8) * mm, "end": v(391.32, -3918.17) * mm});
            skLineSegment(sketch, "E452", {"start": v(391.32, -3918.17) * mm, "end": v(382.16, -3860.19) * mm});
            skLineSegment(sketch, "E453", {"start": v(382.16, -3860.19) * mm, "end": v(367.29, -3808.79) * mm});
            skLineSegment(sketch, "E454", {"start": v(367.29, -3808.79) * mm, "end": v(345.78, -3763.88) * mm});
            skLineSegment(sketch, "E455", {"start": v(345.78, -3763.88) * mm, "end": v(316.7, -3725.38) * mm});
            skLineSegment(sketch, "E456", {"start": v(316.7, -3725.38) * mm, "end": v(284.72, -3697.85) * mm});
            skLineSegment(sketch, "E457", {"start": v(284.72, -3697.85) * mm, "end": v(314.52, -3671.25) * mm});
            skLineSegment(sketch, "E458", {"start": v(314.52, -3671.25) * mm, "end": v(335.7, -3639.35) * mm});
            skLineSegment(sketch, "E459", {"start": v(335.7, -3639.35) * mm, "end": v(348.64, -3603.9) * mm});
            skLineSegment(sketch, "E460", {"start": v(348.64, -3603.9) * mm, "end": v(353.65, -3566.64) * mm});
            skLineSegment(sketch, "E461", {"start": v(353.65, -3566.64) * mm, "end": v(351.09, -3529.33) * mm});
            skLineSegment(sketch, "E462", {"start": v(351.09, -3529.33) * mm, "end": v(341.3, -3493.72) * mm});
            skLineSegment(sketch, "E463", {"start": v(341.3, -3493.72) * mm, "end": v(324.61, -3461.56) * mm});
            skLineSegment(sketch, "E464", {"start": v(324.61, -3461.56) * mm, "end": v(301.38, -3434.6) * mm});
            skLineSegment(sketch, "E465", {"start": v(301.38, -3434.6) * mm, "end": v(355.66, -3386.13) * mm});
            skLineSegment(sketch, "E466", {"start": v(355.66, -3386.13) * mm, "end": v(394.54, -3327.82) * mm});
            skLineSegment(sketch, "E467", {"start": v(394.54, -3327.82) * mm, "end": v(418.08, -3262.93) * mm});
            skLineSegment(sketch, "E468", {"start": v(418.08, -3262.93) * mm, "end": v(426.33, -3194.71) * mm});
            skLineSegment(sketch, "E469", {"start": v(426.33, -3194.71) * mm, "end": v(419.3, -3126.41) * mm});
            skLineSegment(sketch, "E470", {"start": v(419.3, -3126.41) * mm, "end": v(397.07, -3061.29) * mm});
            skLineSegment(sketch, "E471", {"start": v(397.07, -3061.29) * mm, "end": v(359.67, -3002.58) * mm});
            skLineSegment(sketch, "E472", {"start": v(359.67, -3002.58) * mm, "end": v(307.12, -2953.55) * mm});
            skLineSegment(sketch, "E473", {"start": v(307.12, -2953.55) * mm, "end": v(316.6, -2912.7) * mm});
            skLineSegment(sketch, "E474", {"start": v(316.6, -2912.7) * mm, "end": v(330.94, -2815.65) * mm});
            skLineSegment(sketch, "E475", {"start": v(330.94, -2815.65) * mm, "end": v(348.25, -2681.23) * mm});
            skLineSegment(sketch, "E476", {"start": v(348.25, -2681.23) * mm, "end": v(366.66, -2528.28) * mm});
            skLineSegment(sketch, "E477", {"start": v(366.66, -2528.28) * mm, "end": v(384.26, -2375.67) * mm});
            skLineSegment(sketch, "E478", {"start": v(384.26, -2375.67) * mm, "end": v(399.17, -2242.24) * mm});
            skLineSegment(sketch, "E479", {"start": v(399.17, -2242.24) * mm, "end": v(409.5, -2146.84) * mm});
            skLineSegment(sketch, "E480", {"start": v(409.5, -2146.84) * mm, "end": v(413.37, -2108.31) * mm});
            skLineSegment(sketch, "E481", {"start": v(413.37, -2108.31) * mm, "end": v(413.37, -1632.98) * mm});
            skLineSegment(sketch, "E482", {"start": v(413.37, -1632.98) * mm, "end": v(472.92, -1616.78) * mm});
            skLineSegment(sketch, "E483", {"start": v(472.92, -1616.78) * mm, "end": v(531.56, -1598.5) * mm});
            skLineSegment(sketch, "E484", {"start": v(531.56, -1598.5) * mm, "end": v(589.24, -1578.18) * mm});
            skLineSegment(sketch, "E485", {"start": v(589.24, -1578.18) * mm, "end": v(645.93, -1555.85) * mm});
            skLineSegment(sketch, "E486", {"start": v(645.93, -1555.85) * mm, "end": v(701.6, -1531.55) * mm});
            skLineSegment(sketch, "E487", {"start": v(701.6, -1531.55) * mm, "end": v(756.2, -1505.32) * mm});
            skLineSegment(sketch, "E488", {"start": v(756.2, -1505.32) * mm, "end": v(809.71, -1477.18) * mm});
            skLineSegment(sketch, "E489", {"start": v(809.71, -1477.18) * mm, "end": v(862.09, -1447.18) * mm});
            skLineSegment(sketch, "E490", {"start": v(862.09, -1447.18) * mm, "end": v(1198.26, -1783.35) * mm});
            skLineSegment(sketch, "E491", {"start": v(1198.26, -1783.35) * mm, "end": v(1228.35, -1807.94) * mm});
            skLineSegment(sketch, "E492", {"start": v(1228.35, -1807.94) * mm, "end": v(1303.25, -1868.11) * mm});
            skLineSegment(sketch, "E493", {"start": v(1303.25, -1868.11) * mm, "end": v(1408.27, -1951.9) * mm});
            skLineSegment(sketch, "E494", {"start": v(1408.27, -1951.9) * mm, "end": v(1528.72, -2047.3) * mm});
            skLineSegment(sketch, "E495", {"start": v(1528.72, -2047.3) * mm, "end": v(1649.93, -2142.36) * mm});
            skLineSegment(sketch, "E496", {"start": v(1649.93, -2142.36) * mm, "end": v(1757.22, -2225.1) * mm});
            skLineSegment(sketch, "E497", {"start": v(1757.22, -2225.1) * mm, "end": v(1835.9, -2283.54) * mm});
            skLineSegment(sketch, "E498", {"start": v(1835.9, -2283.54) * mm, "end": v(1871.28, -2305.7) * mm});
            skLineSegment(sketch, "E499", {"start": v(1871.28, -2305.7) * mm, "end": v(1868.85, -2377.28) * mm});
            skLineSegment(sketch, "E500", {"start": v(1868.85, -2377.28) * mm, "end": v(1883.87, -2445.15) * mm});
            skLineSegment(sketch, "E501", {"start": v(1883.87, -2445.15) * mm, "end": v(1914.1, -2506.94) * mm});
            skLineSegment(sketch, "E502", {"start": v(1914.1, -2506.94) * mm, "end": v(1957.34, -2560.27) * mm});
            skLineSegment(sketch, "E503", {"start": v(1957.34, -2560.27) * mm, "end": v(2011.34, -2602.78) * mm});
            skLineSegment(sketch, "E504", {"start": v(2011.34, -2602.78) * mm, "end": v(2073.87, -2632.1) * mm});
            skLineSegment(sketch, "E505", {"start": v(2073.87, -2632.1) * mm, "end": v(2142.7, -2645.85) * mm});
            skLineSegment(sketch, "E506", {"start": v(2142.7, -2645.85) * mm, "end": v(2215.63, -2641.66) * mm});
            skLineSegment(sketch, "E507", {"start": v(2215.63, -2641.66) * mm, "end": v(2218.4, -2677.56) * mm});
            skLineSegment(sketch, "E508", {"start": v(2218.4, -2677.56) * mm, "end": v(2229.58, -2712.27) * mm});
            skLineSegment(sketch, "E509", {"start": v(2229.58, -2712.27) * mm, "end": v(2248.12, -2744.37) * mm});
            skLineSegment(sketch, "E510", {"start": v(2248.12, -2744.37) * mm, "end": v(2272.94, -2772.44) * mm});
            skLineSegment(sketch, "E511", {"start": v(2272.94, -2772.44) * mm, "end": v(2302.98, -2795.04) * mm});
            skLineSegment(sketch, "E512", {"start": v(2302.98, -2795.04) * mm, "end": v(2337.17, -2810.75) * mm});
            skLineSegment(sketch, "E513", {"start": v(2337.17, -2810.75) * mm, "end": v(2374.44, -2818.15) * mm});
            skLineSegment(sketch, "E514", {"start": v(2374.44, -2818.15) * mm, "end": v(2413.72, -2815.8) * mm});
            skLineSegment(sketch, "E515", {"start": v(2413.72, -2815.8) * mm, "end": v(2410.37, -2858.12) * mm});
            skLineSegment(sketch, "E516", {"start": v(2410.37, -2858.12) * mm, "end": v(2417, -2905.93) * mm});
            skLineSegment(sketch, "E517", {"start": v(2417, -2905.93) * mm, "end": v(2433.55, -2952.9) * mm});
            skLineSegment(sketch, "E518", {"start": v(2433.55, -2952.9) * mm, "end": v(2459.39, -2999.75) * mm});
            skLineSegment(sketch, "E519", {"start": v(2459.39, -2999.75) * mm, "end": v(2493.92, -3047.21) * mm});
            skLineSegment(sketch, "E520", {"start": v(2493.92, -3047.21) * mm, "end": v(2536.55, -3096) * mm});
            skLineSegment(sketch, "E521", {"start": v(2536.55, -3096) * mm, "end": v(2586.68, -3146.82) * mm});
            skLineSegment(sketch, "E522", {"start": v(2586.68, -3146.82) * mm, "end": v(2643.69, -3200.41) * mm});
            skLineSegment(sketch, "E523", {"start": v(2643.69, -3200.41) * mm, "end": v(2707, -3257.49) * mm});
            skLineSegment(sketch, "E524", {"start": v(2707, -3257.49) * mm, "end": v(2811.9, -3347.23) * mm});
            skLineSegment(sketch, "E525", {"start": v(2811.9, -3347.23) * mm, "end": v(2919.42, -3433.2) * mm});
            skLineSegment(sketch, "E526", {"start": v(2919.42, -3433.2) * mm, "end": v(3026.72, -3514.71) * mm});
            skLineSegment(sketch, "E527", {"start": v(3026.72, -3514.71) * mm, "end": v(3130.97, -3591.14) * mm});
            skLineSegment(sketch, "E528", {"start": v(3130.97, -3591.14) * mm, "end": v(3229.33, -3661.8) * mm});
            skLineSegment(sketch, "E529", {"start": v(3229.33, -3661.8) * mm, "end": v(3318.98, -3726.05) * mm});
            skLineSegment(sketch, "E530", {"start": v(3318.98, -3726.05) * mm, "end": v(3397.07, -3783.22) * mm});
            skLineSegment(sketch, "E531", {"start": v(3397.07, -3783.22) * mm, "end": v(3460.79, -3832.64) * mm});
            skLineSegment(sketch, "E532", {"start": v(3460.79, -3832.64) * mm, "end": v(3452.18, -3870.5) * mm});
            skLineSegment(sketch, "E533", {"start": v(3452.18, -3870.5) * mm, "end": v(3453, -3906.83) * mm});
            skLineSegment(sketch, "E534", {"start": v(3453, -3906.83) * mm, "end": v(3461.93, -3940.87) * mm});
            skLineSegment(sketch, "E535", {"start": v(3461.93, -3940.87) * mm, "end": v(3477.68, -3971.86) * mm});
            skLineSegment(sketch, "E536", {"start": v(3477.68, -3971.86) * mm, "end": v(3498.93, -3999.03) * mm});
            skLineSegment(sketch, "E537", {"start": v(3498.93, -3999.03) * mm, "end": v(3524.38, -4021.65) * mm});
            skLineSegment(sketch, "E538", {"start": v(3524.38, -4021.65) * mm, "end": v(3552.7, -4038.94) * mm});
            skLineSegment(sketch, "E539", {"start": v(3552.7, -4038.94) * mm, "end": v(3582.6, -4050.14) * mm});
            skLineSegment(sketch, "E540", {"start": v(3582.6, -4050.14) * mm, "end": v(3578.83, -4062.26) * mm});
            skLineSegment(sketch, "E541", {"start": v(3578.83, -4062.26) * mm, "end": v(3576.08, -4074.57) * mm});
            skLineSegment(sketch, "E542", {"start": v(3576.08, -4074.57) * mm, "end": v(3574.32, -4087.03) * mm});
            skLineSegment(sketch, "E543", {"start": v(3574.32, -4087.03) * mm, "end": v(3573.54, -4099.59) * mm});
            skLineSegment(sketch, "E544", {"start": v(3573.54, -4099.59) * mm, "end": v(3573.72, -4112.18) * mm});
            skLineSegment(sketch, "E545", {"start": v(3573.72, -4112.18) * mm, "end": v(3574.82, -4124.75) * mm});
            skLineSegment(sketch, "E546", {"start": v(3574.82, -4124.75) * mm, "end": v(3576.84, -4137.26) * mm});
            skLineSegment(sketch, "E547", {"start": v(3576.84, -4137.26) * mm, "end": v(3579.74, -4149.64) * mm});
            skLineSegment(sketch, "E548", {"start": v(3579.74, -4149.64) * mm, "end": v(3244.45, -4417.07) * mm});
            skLineSegment(sketch, "E549", {"start": v(3244.45, -4417.07) * mm, "end": v(2888.56, -4658.05) * mm});
            skLineSegment(sketch, "E550", {"start": v(2888.56, -4658.05) * mm, "end": v(2513.54, -4871.09) * mm});
            skLineSegment(sketch, "E551", {"start": v(2513.54, -4871.09) * mm, "end": v(2120.86, -5054.7) * mm});
            skLineSegment(sketch, "E552", {"start": v(2120.86, -5054.7) * mm, "end": v(1712, -5207.43) * mm});
            skLineSegment(sketch, "E553", {"start": v(1712, -5207.43) * mm, "end": v(1288.43, -5327.79) * mm});
            skLineSegment(sketch, "E554", {"start": v(1288.43, -5327.79) * mm, "end": v(851.62, -5414.3) * mm});
            skLineSegment(sketch, "E555", {"start": v(851.62, -5414.3) * mm, "end": v(403.06, -5465.48) * mm});
            skLineSegment(sketch, "E556", {"start": v(-0.01, -974.86) * mm, "end": v(-196.5, -955.06) * mm});
            skLineSegment(sketch, "E557", {"start": v(-196.5, -955.06) * mm, "end": v(-379.5, -898.25) * mm});
            skLineSegment(sketch, "E558", {"start": v(-379.5, -898.25) * mm, "end": v(-545.11, -808.36) * mm});
            skLineSegment(sketch, "E559", {"start": v(-545.11, -808.36) * mm, "end": v(-689.4, -689.32) * mm});
            skLineSegment(sketch, "E560", {"start": v(-689.4, -689.32) * mm, "end": v(-808.44, -545.04) * mm});
            skLineSegment(sketch, "E561", {"start": v(-808.44, -545.04) * mm, "end": v(-898.33, -379.44) * mm});
            skLineSegment(sketch, "E562", {"start": v(-898.33, -379.44) * mm, "end": v(-955.13, -196.45) * mm});
            skLineSegment(sketch, "E563", {"start": v(-955.13, -196.45) * mm, "end": v(-974.94, 0.01) * mm});
            skLineSegment(sketch, "E564", {"start": v(-974.94, 0.01) * mm, "end": v(-955.13, 196.5) * mm});
            skLineSegment(sketch, "E565", {"start": v(-955.13, 196.5) * mm, "end": v(-898.33, 379.5) * mm});
            skLineSegment(sketch, "E566", {"start": v(-898.33, 379.5) * mm, "end": v(-808.44, 545.1) * mm});
            skLineSegment(sketch, "E567", {"start": v(-808.44, 545.1) * mm, "end": v(-689.4, 689.38) * mm});
            skLineSegment(sketch, "E568", {"start": v(-689.4, 689.38) * mm, "end": v(-545.11, 808.42) * mm});
            skLineSegment(sketch, "E569", {"start": v(-545.11, 808.42) * mm, "end": v(-379.5, 898.3) * mm});
            skLineSegment(sketch, "E570", {"start": v(-379.5, 898.3) * mm, "end": v(-196.5, 955.1) * mm});
            skLineSegment(sketch, "E571", {"start": v(-196.5, 955.1) * mm, "end": v(-0.01, 974.92) * mm});
            skLineSegment(sketch, "E572", {"start": v(-0.01, 974.92) * mm, "end": v(196.46, 955.1) * mm});
            skLineSegment(sketch, "E573", {"start": v(196.46, 955.1) * mm, "end": v(379.46, 898.3) * mm});
            skLineSegment(sketch, "E574", {"start": v(379.46, 898.3) * mm, "end": v(545.06, 808.42) * mm});
            skLineSegment(sketch, "E575", {"start": v(545.06, 808.42) * mm, "end": v(689.34, 689.38) * mm});
            skLineSegment(sketch, "E576", {"start": v(689.34, 689.38) * mm, "end": v(808.38, 545.1) * mm});
            skLineSegment(sketch, "E577", {"start": v(808.38, 545.1) * mm, "end": v(898.26, 379.5) * mm});
            skLineSegment(sketch, "E578", {"start": v(898.26, 379.5) * mm, "end": v(955.06, 196.5) * mm});
            skLineSegment(sketch, "E579", {"start": v(955.06, 196.5) * mm, "end": v(974.86, 0.01) * mm});
            skLineSegment(sketch, "E580", {"start": v(974.86, 0.01) * mm, "end": v(955.06, -196.45) * mm});
            skLineSegment(sketch, "E581", {"start": v(955.06, -196.45) * mm, "end": v(898.26, -379.44) * mm});
            skLineSegment(sketch, "E582", {"start": v(898.26, -379.44) * mm, "end": v(808.38, -545.04) * mm});
            skLineSegment(sketch, "E583", {"start": v(808.38, -545.04) * mm, "end": v(689.34, -689.32) * mm});
            skLineSegment(sketch, "E584", {"start": v(689.34, -689.32) * mm, "end": v(545.06, -808.36) * mm});
            skLineSegment(sketch, "E585", {"start": v(545.06, -808.36) * mm, "end": v(379.46, -898.25) * mm});
            skLineSegment(sketch, "E586", {"start": v(379.46, -898.25) * mm, "end": v(196.46, -955.06) * mm});
            skLineSegment(sketch, "E587", {"start": v(196.46, -955.06) * mm, "end": v(-0.01, -974.86) * mm});
            skLineSegment(sketch, "E588", {"start": v(-29.86, -6359.56) * mm, "end": v(-70.17, -6355.22) * mm});
            skLineSegment(sketch, "E589", {"start": v(-70.17, -6355.22) * mm, "end": v(-107.4, -6343.62) * mm});
            skLineSegment(sketch, "E590", {"start": v(-107.4, -6343.62) * mm, "end": v(-140.78, -6325.54) * mm});
            skLineSegment(sketch, "E591", {"start": v(-140.78, -6325.54) * mm, "end": v(-169.53, -6301.76) * mm});
            skLineSegment(sketch, "E592", {"start": v(-169.53, -6301.76) * mm, "end": v(-192.87, -6273.06) * mm});
            skLineSegment(sketch, "E593", {"start": v(-192.87, -6273.06) * mm, "end": v(-210.03, -6240.24) * mm});
            skLineSegment(sketch, "E594", {"start": v(-210.03, -6240.24) * mm, "end": v(-220.23, -6204.07) * mm});
            skLineSegment(sketch, "E595", {"start": v(-220.23, -6204.07) * mm, "end": v(-222.7, -6165.33) * mm});
            skLineSegment(sketch, "E596", {"start": v(-222.7, -6165.33) * mm, "end": v(-217.28, -6126.68) * mm});
            skLineSegment(sketch, "E597", {"start": v(-217.28, -6126.68) * mm, "end": v(-204.89, -6090.75) * mm});
            skLineSegment(sketch, "E598", {"start": v(-204.89, -6090.75) * mm, "end": v(-186.3, -6058.3) * mm});
            skLineSegment(sketch, "E599", {"start": v(-186.3, -6058.3) * mm, "end": v(-162.3, -6030.12) * mm});
            skLineSegment(sketch, "E600", {"start": v(-162.3, -6030.12) * mm, "end": v(-133.69, -6006.96) * mm});
            skLineSegment(sketch, "E601", {"start": v(-133.69, -6006.96) * mm, "end": v(-101.22, -5989.59) * mm});
            skLineSegment(sketch, "E602", {"start": v(-101.22, -5989.59) * mm, "end": v(-65.69, -5978.78) * mm});
            skLineSegment(sketch, "E603", {"start": v(-65.69, -5978.78) * mm, "end": v(-27.88, -5975.29) * mm});
            skLineSegment(sketch, "E604", {"start": v(-27.88, -5975.29) * mm, "end": v(9.9, -5979.96) * mm});
            skLineSegment(sketch, "E605", {"start": v(9.9, -5979.96) * mm, "end": v(45.31, -5991.42) * mm});
            skLineSegment(sketch, "E606", {"start": v(45.31, -5991.42) * mm, "end": v(77.59, -6009.02) * mm});
            skLineSegment(sketch, "E607", {"start": v(77.59, -6009.02) * mm, "end": v(105.96, -6032.09) * mm});
            skLineSegment(sketch, "E608", {"start": v(105.96, -6032.09) * mm, "end": v(129.64, -6059.98) * mm});
            skLineSegment(sketch, "E609", {"start": v(129.64, -6059.98) * mm, "end": v(147.87, -6092.02) * mm});
            skLineSegment(sketch, "E610", {"start": v(147.87, -6092.02) * mm, "end": v(159.88, -6127.57) * mm});
            skLineSegment(sketch, "E611", {"start": v(159.88, -6127.57) * mm, "end": v(164.88, -6165.96) * mm});
            skLineSegment(sketch, "E612", {"start": v(164.88, -6165.96) * mm, "end": v(162.03, -6205) * mm});
            skLineSegment(sketch, "E613", {"start": v(162.03, -6205) * mm, "end": v(151.47, -6241.57) * mm});
            skLineSegment(sketch, "E614", {"start": v(151.47, -6241.57) * mm, "end": v(133.99, -6274.8) * mm});
            skLineSegment(sketch, "E615", {"start": v(133.99, -6274.8) * mm, "end": v(110.37, -6303.79) * mm});
            skLineSegment(sketch, "E616", {"start": v(110.37, -6303.79) * mm, "end": v(81.39, -6327.65) * mm});
            skLineSegment(sketch, "E617", {"start": v(81.39, -6327.65) * mm, "end": v(47.84, -6345.5) * mm});
            skLineSegment(sketch, "E618", {"start": v(47.84, -6345.5) * mm, "end": v(10.5, -6356.43) * mm});
            skLineSegment(sketch, "E619", {"start": v(10.5, -6356.43) * mm, "end": v(-29.86, -6359.56) * mm});
            skLineSegment(sketch, "E620", {"start": v(-330.6, -5397.18) * mm, "end": v(-341.83, -5403.07) * mm});
            skLineSegment(sketch, "E621", {"start": v(-341.83, -5403.07) * mm, "end": v(-352.48, -5409.83) * mm});
            skLineSegment(sketch, "E622", {"start": v(-352.48, -5409.83) * mm, "end": v(-362.54, -5417.4) * mm});
            skLineSegment(sketch, "E623", {"start": v(-362.54, -5417.4) * mm, "end": v(-371.97, -5425.72) * mm});
            skLineSegment(sketch, "E624", {"start": v(-371.97, -5425.72) * mm, "end": v(-380.75, -5434.75) * mm});
            skLineSegment(sketch, "E625", {"start": v(-380.75, -5434.75) * mm, "end": v(-388.87, -5444.42) * mm});
            skLineSegment(sketch, "E626", {"start": v(-388.87, -5444.42) * mm, "end": v(-396.28, -5454.68) * mm});
            skLineSegment(sketch, "E627", {"start": v(-396.28, -5454.68) * mm, "end": v(-402.98, -5465.48) * mm});
            skLineSegment(sketch, "E628", {"start": v(-402.98, -5465.48) * mm, "end": v(-851.53, -5414.3) * mm});
            skLineSegment(sketch, "E629", {"start": v(-851.53, -5414.3) * mm, "end": v(-1288.33, -5327.81) * mm});
            skLineSegment(sketch, "E630", {"start": v(-1288.33, -5327.81) * mm, "end": v(-1711.9, -5207.48) * mm});
            skLineSegment(sketch, "E631", {"start": v(-1711.9, -5207.48) * mm, "end": v(-2120.77, -5054.77) * mm});
            skLineSegment(sketch, "E632", {"start": v(-2120.77, -5054.77) * mm, "end": v(-2513.46, -4871.17) * mm});
            skLineSegment(sketch, "E633", {"start": v(-2513.46, -4871.17) * mm, "end": v(-2888.5, -4658.16) * mm});
            skLineSegment(sketch, "E634", {"start": v(-2888.5, -4658.16) * mm, "end": v(-3244.4, -4417.2) * mm});
            skLineSegment(sketch, "E635", {"start": v(-3244.4, -4417.2) * mm, "end": v(-3579.71, -4149.79) * mm});
            skLineSegment(sketch, "E636", {"start": v(-3579.71, -4149.79) * mm, "end": v(-3576.79, -4137.42) * mm});
            skLineSegment(sketch, "E637", {"start": v(-3576.79, -4137.42) * mm, "end": v(-3574.75, -4124.91) * mm});
            skLineSegment(sketch, "E638", {"start": v(-3574.75, -4124.91) * mm, "end": v(-3573.63, -4112.33) * mm});
            skLineSegment(sketch, "E639", {"start": v(-3573.63, -4112.33) * mm, "end": v(-3573.45, -4099.73) * mm});
            skLineSegment(sketch, "E640", {"start": v(-3573.45, -4099.73) * mm, "end": v(-3574.24, -4087.15) * mm});
            skLineSegment(sketch, "E641", {"start": v(-3574.24, -4087.15) * mm, "end": v(-3576.02, -4074.65) * mm});
            skLineSegment(sketch, "E642", {"start": v(-3576.02, -4074.65) * mm, "end": v(-3578.82, -4062.3) * mm});
            skLineSegment(sketch, "E643", {"start": v(-3578.82, -4062.3) * mm, "end": v(-3582.66, -4050.12) * mm});
            skLineSegment(sketch, "E644", {"start": v(-3582.66, -4050.12) * mm, "end": v(-3552.3, -4038.75) * mm});
            skLineSegment(sketch, "E645", {"start": v(-3552.3, -4038.75) * mm, "end": v(-3523.77, -4021.33) * mm});
            skLineSegment(sketch, "E646", {"start": v(-3523.77, -4021.33) * mm, "end": v(-3498.33, -3998.63) * mm});
            skLineSegment(sketch, "E647", {"start": v(-3498.33, -3998.63) * mm, "end": v(-3477.2, -3971.4) * mm});
            skLineSegment(sketch, "E648", {"start": v(-3477.2, -3971.4) * mm, "end": v(-3461.65, -3940.42) * mm});
            skLineSegment(sketch, "E649", {"start": v(-3461.65, -3940.42) * mm, "end": v(-3452.9, -3906.45) * mm});
            skLineSegment(sketch, "E650", {"start": v(-3452.9, -3906.45) * mm, "end": v(-3452.2, -3870.26) * mm});
            skLineSegment(sketch, "E651", {"start": v(-3452.2, -3870.26) * mm, "end": v(-3460.81, -3832.62) * mm});
            skLineSegment(sketch, "E652", {"start": v(-3460.81, -3832.62) * mm, "end": v(-3397.03, -3783.27) * mm});
            skLineSegment(sketch, "E653", {"start": v(-3397.03, -3783.27) * mm, "end": v(-3318.88, -3726.16) * mm});
            skLineSegment(sketch, "E654", {"start": v(-3318.88, -3726.16) * mm, "end": v(-3229.2, -3661.96) * mm});
            skLineSegment(sketch, "E655", {"start": v(-3229.2, -3661.96) * mm, "end": v(-3130.82, -3591.31) * mm});
            skLineSegment(sketch, "E656", {"start": v(-3130.82, -3591.31) * mm, "end": v(-3026.57, -3514.88) * mm});
            skLineSegment(sketch, "E657", {"start": v(-3026.57, -3514.88) * mm, "end": v(-2919.3, -3433.33) * mm});
            skLineSegment(sketch, "E658", {"start": v(-2919.3, -3433.33) * mm, "end": v(-2811.84, -3347.3) * mm});
            skLineSegment(sketch, "E659", {"start": v(-2811.84, -3347.3) * mm, "end": v(-2707.02, -3257.46) * mm});
            skLineSegment(sketch, "E660", {"start": v(-2707.02, -3257.46) * mm, "end": v(-2643.66, -3200.45) * mm});
            skLineSegment(sketch, "E661", {"start": v(-2643.66, -3200.45) * mm, "end": v(-2586.62, -3146.88) * mm});
            skLineSegment(sketch, "E662", {"start": v(-2586.62, -3146.88) * mm, "end": v(-2536.5, -3096.06) * mm});
            skLineSegment(sketch, "E663", {"start": v(-2536.5, -3096.06) * mm, "end": v(-2493.87, -3047.27) * mm});
            skLineSegment(sketch, "E664", {"start": v(-2493.87, -3047.27) * mm, "end": v(-2459.35, -2999.8) * mm});
            skLineSegment(sketch, "E665", {"start": v(-2459.35, -2999.8) * mm, "end": v(-2433.52, -2952.93) * mm});
            skLineSegment(sketch, "E666", {"start": v(-2433.52, -2952.93) * mm, "end": v(-2416.98, -2905.97) * mm});
            skLineSegment(sketch, "E667", {"start": v(-2416.98, -2905.97) * mm, "end": v(-2410.32, -2858.2) * mm});
            skLineSegment(sketch, "E668", {"start": v(-2410.32, -2858.2) * mm, "end": v(-2413.44, -2816.09) * mm});
            skLineSegment(sketch, "E669", {"start": v(-2413.44, -2816.09) * mm, "end": v(-2373.58, -2818.36) * mm});
            skLineSegment(sketch, "E670", {"start": v(-2373.58, -2818.36) * mm, "end": v(-2336.04, -2810.8) * mm});
            skLineSegment(sketch, "E671", {"start": v(-2336.04, -2810.8) * mm, "end": v(-2301.84, -2794.87) * mm});
            skLineSegment(sketch, "E672", {"start": v(-2301.84, -2794.87) * mm, "end": v(-2271.95, -2772.07) * mm});
            skLineSegment(sketch, "E673", {"start": v(-2271.95, -2772.07) * mm, "end": v(-2247.38, -2743.88) * mm});
            skLineSegment(sketch, "E674", {"start": v(-2247.38, -2743.88) * mm, "end": v(-2229.13, -2711.77) * mm});
            skLineSegment(sketch, "E675", {"start": v(-2229.13, -2711.77) * mm, "end": v(-2218.19, -2677.23) * mm});
            skLineSegment(sketch, "E676", {"start": v(-2218.19, -2677.23) * mm, "end": v(-2215.55, -2641.74) * mm});
            skLineSegment(sketch, "E677", {"start": v(-2215.55, -2641.74) * mm, "end": v(-2142.9, -2645.84) * mm});
            skLineSegment(sketch, "E678", {"start": v(-2142.9, -2645.84) * mm, "end": v(-2074.16, -2632.1) * mm});
            skLineSegment(sketch, "E679", {"start": v(-2074.16, -2632.1) * mm, "end": v(-2011.63, -2602.87) * mm});
            skLineSegment(sketch, "E680", {"start": v(-2011.63, -2602.87) * mm, "end": v(-1957.56, -2560.46) * mm});
            skLineSegment(sketch, "E681", {"start": v(-1957.56, -2560.46) * mm, "end": v(-1914.22, -2507.2) * mm});
            skLineSegment(sketch, "E682", {"start": v(-1914.22, -2507.2) * mm, "end": v(-1883.9, -2445.43) * mm});
            skLineSegment(sketch, "E683", {"start": v(-1883.9, -2445.43) * mm, "end": v(-1868.84, -2377.47) * mm});
            skLineSegment(sketch, "E684", {"start": v(-1868.84, -2377.47) * mm, "end": v(-1871.33, -2305.65) * mm});
            skLineSegment(sketch, "E685", {"start": v(-1871.33, -2305.65) * mm, "end": v(-1835.75, -2283.47) * mm});
            skLineSegment(sketch, "E686", {"start": v(-1835.75, -2283.47) * mm, "end": v(-1756.98, -2224.98) * mm});
            skLineSegment(sketch, "E687", {"start": v(-1756.98, -2224.98) * mm, "end": v(-1649.68, -2142.17) * mm});
            skLineSegment(sketch, "E688", {"start": v(-1649.68, -2142.17) * mm, "end": v(-1528.51, -2047.04) * mm});
            skLineSegment(sketch, "E689", {"start": v(-1528.51, -2047.04) * mm, "end": v(-1408.15, -1951.57) * mm});
            skLineSegment(sketch, "E690", {"start": v(-1408.15, -1951.57) * mm, "end": v(-1303.25, -1867.76) * mm});
            skLineSegment(sketch, "E691", {"start": v(-1303.25, -1867.76) * mm, "end": v(-1228.48, -1807.6) * mm});
            skLineSegment(sketch, "E692", {"start": v(-1228.48, -1807.6) * mm, "end": v(-1198.51, -1783.1) * mm});
            skLineSegment(sketch, "E693", {"start": v(-1198.51, -1783.1) * mm, "end": v(-862.4, -1446.97) * mm});
            skLineSegment(sketch, "E694", {"start": v(-862.4, -1446.97) * mm, "end": v(-810.03, -1477) * mm});
            skLineSegment(sketch, "E695", {"start": v(-810.03, -1477) * mm, "end": v(-756.53, -1505.14) * mm});
            skLineSegment(sketch, "E696", {"start": v(-756.53, -1505.14) * mm, "end": v(-701.93, -1531.39) * mm});
            skLineSegment(sketch, "E697", {"start": v(-701.93, -1531.39) * mm, "end": v(-646.27, -1555.7) * mm});
            skLineSegment(sketch, "E698", {"start": v(-646.27, -1555.7) * mm, "end": v(-589.59, -1578.05) * mm});
            skLineSegment(sketch, "E699", {"start": v(-589.59, -1578.05) * mm, "end": v(-531.9, -1598.38) * mm});
            skLineSegment(sketch, "E700", {"start": v(-531.9, -1598.38) * mm, "end": v(-473.28, -1616.68) * mm});
            skLineSegment(sketch, "E701", {"start": v(-473.28, -1616.68) * mm, "end": v(-413.73, -1632.9) * mm});
            skLineSegment(sketch, "E702", {"start": v(-413.73, -1632.9) * mm, "end": v(-413.73, -2108.31) * mm});
            skLineSegment(sketch, "E703", {"start": v(-413.73, -2108.31) * mm, "end": v(-409.83, -2146.98) * mm});
            skLineSegment(sketch, "E704", {"start": v(-409.83, -2146.98) * mm, "end": v(-399.42, -2242.49) * mm});
            skLineSegment(sketch, "E705", {"start": v(-399.42, -2242.49) * mm, "end": v(-384.4, -2375.98) * mm});
            skLineSegment(sketch, "E706", {"start": v(-384.4, -2375.98) * mm, "end": v(-366.7, -2528.62) * mm});
            skLineSegment(sketch, "E707", {"start": v(-366.7, -2528.62) * mm, "end": v(-348.2, -2681.54) * mm});
            skLineSegment(sketch, "E708", {"start": v(-348.2, -2681.54) * mm, "end": v(-330.84, -2815.9) * mm});
            skLineSegment(sketch, "E709", {"start": v(-330.84, -2815.9) * mm, "end": v(-316.53, -2912.86) * mm});
            skLineSegment(sketch, "E710", {"start": v(-316.53, -2912.86) * mm, "end": v(-307.17, -2953.55) * mm});
            skLineSegment(sketch, "E711", {"start": v(-307.17, -2953.55) * mm, "end": v(-359.5, -3002.46) * mm});
            skLineSegment(sketch, "E712", {"start": v(-359.5, -3002.46) * mm, "end": v(-396.88, -3061.07) * mm});
            skLineSegment(sketch, "E713", {"start": v(-396.88, -3061.07) * mm, "end": v(-419.2, -3126.15) * mm});
            skLineSegment(sketch, "E714", {"start": v(-419.2, -3126.15) * mm, "end": v(-426.34, -3194.43) * mm});
            skLineSegment(sketch, "E715", {"start": v(-426.34, -3194.43) * mm, "end": v(-418.22, -3262.67) * mm});
            skLineSegment(sketch, "E716", {"start": v(-418.22, -3262.67) * mm, "end": v(-394.74, -3327.6) * mm});
            skLineSegment(sketch, "E717", {"start": v(-394.74, -3327.6) * mm, "end": v(-355.8, -3386) * mm});
            skLineSegment(sketch, "E718", {"start": v(-355.8, -3386) * mm, "end": v(-301.28, -3434.6) * mm});
            skLineSegment(sketch, "E719", {"start": v(-301.28, -3434.6) * mm, "end": v(-324.7, -3461.95) * mm});
            skLineSegment(sketch, "E720", {"start": v(-324.7, -3461.95) * mm, "end": v(-341.34, -3494.4) * mm});
            skLineSegment(sketch, "E721", {"start": v(-341.34, -3494.4) * mm, "end": v(-350.93, -3530.22) * mm});
            skLineSegment(sketch, "E722", {"start": v(-350.93, -3530.22) * mm, "end": v(-353.22, -3567.61) * mm});
            skLineSegment(sketch, "E723", {"start": v(-353.22, -3567.61) * mm, "end": v(-347.95, -3604.84) * mm});
            skLineSegment(sketch, "E724", {"start": v(-347.95, -3604.84) * mm, "end": v(-334.88, -3640.13) * mm});
            skLineSegment(sketch, "E725", {"start": v(-334.88, -3640.13) * mm, "end": v(-313.75, -3671.72) * mm});
            skLineSegment(sketch, "E726", {"start": v(-313.75, -3671.72) * mm, "end": v(-284.31, -3697.85) * mm});
            skLineSegment(sketch, "E727", {"start": v(-284.31, -3697.85) * mm, "end": v(-316.62, -3725.38) * mm});
            skLineSegment(sketch, "E728", {"start": v(-316.62, -3725.38) * mm, "end": v(-345.73, -3763.88) * mm});
            skLineSegment(sketch, "E729", {"start": v(-345.73, -3763.88) * mm, "end": v(-367.25, -3808.79) * mm});
            skLineSegment(sketch, "E730", {"start": v(-367.25, -3808.79) * mm, "end": v(-382.1, -3860.19) * mm});
            skLineSegment(sketch, "E731", {"start": v(-382.1, -3860.19) * mm, "end": v(-391.25, -3918.17) * mm});
            skLineSegment(sketch, "E732", {"start": v(-391.25, -3918.17) * mm, "end": v(-395.6, -3982.8) * mm});
            skLineSegment(sketch, "E733", {"start": v(-395.6, -3982.8) * mm, "end": v(-396.1, -4054.19) * mm});
            skLineSegment(sketch, "E734", {"start": v(-396.1, -4054.19) * mm, "end": v(-393.67, -4132.4) * mm});
            skLineSegment(sketch, "E735", {"start": v(-393.67, -4132.4) * mm, "end": v(-389.27, -4217.5) * mm});
            skLineSegment(sketch, "E736", {"start": v(-389.27, -4217.5) * mm, "end": v(-378.54, -4355.15) * mm});
            skLineSegment(sketch, "E737", {"start": v(-378.54, -4355.15) * mm, "end": v(-363.29, -4491.97) * mm});
            skLineSegment(sketch, "E738", {"start": v(-363.29, -4491.97) * mm, "end": v(-345.06, -4625.5) * mm});
            skLineSegment(sketch, "E739", {"start": v(-345.06, -4625.5) * mm, "end": v(-325.39, -4753.25) * mm});
            skLineSegment(sketch, "E740", {"start": v(-325.39, -4753.25) * mm, "end": v(-305.8, -4872.77) * mm});
            skLineSegment(sketch, "E741", {"start": v(-305.8, -4872.77) * mm, "end": v(-287.85, -4981.59) * mm});
            skLineSegment(sketch, "E742", {"start": v(-287.85, -4981.59) * mm, "end": v(-273.05, -5077.23) * mm});
            skLineSegment(sketch, "E743", {"start": v(-273.05, -5077.23) * mm, "end": v(-262.95, -5157.23) * mm});
            skLineSegment(sketch, "E744", {"start": v(-262.95, -5157.23) * mm, "end": v(-295.82, -5177.92) * mm});
            skLineSegment(sketch, "E745", {"start": v(-295.82, -5177.92) * mm, "end": v(-320.93, -5204.19) * mm});
            skLineSegment(sketch, "E746", {"start": v(-320.93, -5204.19) * mm, "end": v(-338.67, -5234.58) * mm});
            skLineSegment(sketch, "E747", {"start": v(-338.67, -5234.58) * mm, "end": v(-349.45, -5267.62) * mm});
            skLineSegment(sketch, "E748", {"start": v(-349.45, -5267.62) * mm, "end": v(-353.63, -5301.87) * mm});
            skLineSegment(sketch, "E749", {"start": v(-353.63, -5301.87) * mm, "end": v(-351.63, -5335.85) * mm});
            skLineSegment(sketch, "E750", {"start": v(-351.63, -5335.85) * mm, "end": v(-343.82, -5368.1) * mm});
            skLineSegment(sketch, "E751", {"start": v(-343.82, -5368.1) * mm, "end": v(-330.6, -5397.18) * mm});
            skLineSegment(sketch, "E752", {"start": v(-1749.36, -5917.48) * mm, "end": v(-1764.05, -5953.64) * mm});
            skLineSegment(sketch, "E753", {"start": v(-1764.05, -5953.64) * mm, "end": v(-1785.24, -5984.82) * mm});
            skLineSegment(sketch, "E754", {"start": v(-1785.24, -5984.82) * mm, "end": v(-1811.94, -6010.55) * mm});
            skLineSegment(sketch, "E755", {"start": v(-1811.94, -6010.55) * mm, "end": v(-1843.18, -6030.33) * mm});
            skLineSegment(sketch, "E756", {"start": v(-1843.18, -6030.33) * mm, "end": v(-1878, -6043.72) * mm});
            skLineSegment(sketch, "E757", {"start": v(-1878, -6043.72) * mm, "end": v(-1915.39, -6050.21) * mm});
            skLineSegment(sketch, "E758", {"start": v(-1915.39, -6050.21) * mm, "end": v(-1954.4, -6049.36) * mm});
            skLineSegment(sketch, "E759", {"start": v(-1954.4, -6049.36) * mm, "end": v(-1994.04, -6040.67) * mm});
            skLineSegment(sketch, "E760", {"start": v(-1994.04, -6040.67) * mm, "end": v(-2031.33, -6024.85) * mm});
            skLineSegment(sketch, "E761", {"start": v(-2031.33, -6024.85) * mm, "end": v(-2063.27, -6002.56) * mm});
            skLineSegment(sketch, "E762", {"start": v(-2063.27, -6002.56) * mm, "end": v(-2089.4, -5974.9) * mm});
            skLineSegment(sketch, "E763", {"start": v(-2089.4, -5974.9) * mm, "end": v(-2109.26, -5943) * mm});
            skLineSegment(sketch, "E764", {"start": v(-2109.26, -5943) * mm, "end": v(-2122.4, -5907.94) * mm});
            skLineSegment(sketch, "E765", {"start": v(-2122.4, -5907.94) * mm, "end": v(-2128.39, -5870.85) * mm});
            skLineSegment(sketch, "E766", {"start": v(-2128.39, -5870.85) * mm, "end": v(-2126.75, -5832.83) * mm});
            skLineSegment(sketch, "E767", {"start": v(-2126.75, -5832.83) * mm, "end": v(-2117.05, -5795) * mm});
            skLineSegment(sketch, "E768", {"start": v(-2117.05, -5795) * mm, "end": v(-2100.05, -5760.14) * mm});
            skLineSegment(sketch, "E769", {"start": v(-2100.05, -5760.14) * mm, "end": v(-2077.35, -5730.25) * mm});
            skLineSegment(sketch, "E770", {"start": v(-2077.35, -5730.25) * mm, "end": v(-2049.87, -5705.7) * mm});
            skLineSegment(sketch, "E771", {"start": v(-2049.87, -5705.7) * mm, "end": v(-2018.56, -5686.86) * mm});
            skLineSegment(sketch, "E772", {"start": v(-2018.56, -5686.86) * mm, "end": v(-1984.36, -5674.07) * mm});
            skLineSegment(sketch, "E773", {"start": v(-1984.36, -5674.07) * mm, "end": v(-1948.2, -5667.7) * mm});
            skLineSegment(sketch, "E774", {"start": v(-1948.2, -5667.7) * mm, "end": v(-1911.01, -5668.14) * mm});
            skLineSegment(sketch, "E775", {"start": v(-1911.01, -5668.14) * mm, "end": v(-1873.75, -5675.72) * mm});
            skLineSegment(sketch, "E776", {"start": v(-1873.75, -5675.72) * mm, "end": v(-1839.03, -5691.01) * mm});
            skLineSegment(sketch, "E777", {"start": v(-1839.03, -5691.01) * mm, "end": v(-1808.8, -5712.56) * mm});
            skLineSegment(sketch, "E778", {"start": v(-1808.8, -5712.56) * mm, "end": v(-1783.57, -5739.38) * mm});
            skLineSegment(sketch, "E779", {"start": v(-1783.57, -5739.38) * mm, "end": v(-1763.8, -5770.46) * mm});
            skLineSegment(sketch, "E780", {"start": v(-1763.8, -5770.46) * mm, "end": v(-1750, -5804.8) * mm});
            skLineSegment(sketch, "E781", {"start": v(-1750, -5804.8) * mm, "end": v(-1742.68, -5841.43) * mm});
            skLineSegment(sketch, "E782", {"start": v(-1742.68, -5841.43) * mm, "end": v(-1742.3, -5879.31) * mm});
            skLineSegment(sketch, "E783", {"start": v(-1742.3, -5879.31) * mm, "end": v(-1749.36, -5917.48) * mm});
            skLineSegment(sketch, "E784", {"start": v(-3490.91, -5085.5) * mm, "end": v(-3515.98, -5115.13) * mm});
            skLineSegment(sketch, "E785", {"start": v(-3515.98, -5115.13) * mm, "end": v(-3545.89, -5138.32) * mm});
            skLineSegment(sketch, "E786", {"start": v(-3545.89, -5138.32) * mm, "end": v(-3579.5, -5154.83) * mm});
            skLineSegment(sketch, "E787", {"start": v(-3579.5, -5154.83) * mm, "end": v(-3615.7, -5164.42) * mm});
            skLineSegment(sketch, "E788", {"start": v(-3615.7, -5164.42) * mm, "end": v(-3653.32, -5166.87) * mm});
            skLineSegment(sketch, "E789", {"start": v(-3653.32, -5166.87) * mm, "end": v(-3691.23, -5161.94) * mm});
            skLineSegment(sketch, "E790", {"start": v(-3691.23, -5161.94) * mm, "end": v(-3728.3, -5149.4) * mm});
            skLineSegment(sketch, "E791", {"start": v(-3728.3, -5149.4) * mm, "end": v(-3763.38, -5129) * mm});
            skLineSegment(sketch, "E792", {"start": v(-3763.38, -5129) * mm, "end": v(-3793.1, -5101.33) * mm});
            skLineSegment(sketch, "E793", {"start": v(-3793.1, -5101.33) * mm, "end": v(-3816.07, -5069.62) * mm});
            skLineSegment(sketch, "E794", {"start": v(-3816.07, -5069.62) * mm, "end": v(-3832.14, -5034.98) * mm});
            skLineSegment(sketch, "E795", {"start": v(-3832.14, -5034.98) * mm, "end": v(-3841.15, -4998.5) * mm});
            skLineSegment(sketch, "E796", {"start": v(-3841.15, -4998.5) * mm, "end": v(-3842.93, -4961.3) * mm});
            skLineSegment(sketch, "E797", {"start": v(-3842.93, -4961.3) * mm, "end": v(-3837.34, -4924.44) * mm});
            skLineSegment(sketch, "E798", {"start": v(-3837.34, -4924.44) * mm, "end": v(-3824.2, -4889.06) * mm});
            skLineSegment(sketch, "E799", {"start": v(-3824.2, -4889.06) * mm, "end": v(-3803.36, -4856.24) * mm});
            skLineSegment(sketch, "E800", {"start": v(-3803.36, -4856.24) * mm, "end": v(-3776.28, -4828.22) * mm});
            skLineSegment(sketch, "E801", {"start": v(-3776.28, -4828.22) * mm, "end": v(-3745.22, -4806.59) * mm});
            skLineSegment(sketch, "E802", {"start": v(-3745.22, -4806.59) * mm, "end": v(-3711.27, -4791.5) * mm});
            skLineSegment(sketch, "E803", {"start": v(-3711.27, -4791.5) * mm, "end": v(-3675.5, -4783.1) * mm});
            skLineSegment(sketch, "E804", {"start": v(-3675.5, -4783.1) * mm, "end": v(-3638.98, -4781.54) * mm});
            skLineSegment(sketch, "E805", {"start": v(-3638.98, -4781.54) * mm, "end": v(-3602.8, -4786.98) * mm});
            skLineSegment(sketch, "E806", {"start": v(-3602.8, -4786.98) * mm, "end": v(-3568.04, -4799.55) * mm});
            skLineSegment(sketch, "E807", {"start": v(-3568.04, -4799.55) * mm, "end": v(-3535.77, -4819.4) * mm});
            skLineSegment(sketch, "E808", {"start": v(-3535.77, -4819.4) * mm, "end": v(-3507.4, -4844.57) * mm});
            skLineSegment(sketch, "E809", {"start": v(-3507.4, -4844.57) * mm, "end": v(-3485.1, -4874.07) * mm});
            skLineSegment(sketch, "E810", {"start": v(-3485.1, -4874.07) * mm, "end": v(-3469.07, -4906.9) * mm});
            skLineSegment(sketch, "E811", {"start": v(-3469.07, -4906.9) * mm, "end": v(-3459.54, -4942.04) * mm});
            skLineSegment(sketch, "E812", {"start": v(-3459.54, -4942.04) * mm, "end": v(-3456.75, -4978.49) * mm});
            skLineSegment(sketch, "E813", {"start": v(-3456.75, -4978.49) * mm, "end": v(-3460.9, -5015.22) * mm});
            skLineSegment(sketch, "E814", {"start": v(-3460.9, -5015.22) * mm, "end": v(-3472.21, -5051.23) * mm});
            skLineSegment(sketch, "E815", {"start": v(-3472.21, -5051.23) * mm, "end": v(-3490.91, -5085.5) * mm});
            skLineSegment(sketch, "E816", {"start": v(-4050.14, -3582.6) * mm, "end": v(-4062.27, -3578.82) * mm});
            skLineSegment(sketch, "E817", {"start": v(-4062.27, -3578.82) * mm, "end": v(-4074.6, -3576.07) * mm});
            skLineSegment(sketch, "E818", {"start": v(-4074.6, -3576.07) * mm, "end": v(-4087.09, -3574.31) * mm});
            skLineSegment(sketch, "E819", {"start": v(-4087.09, -3574.31) * mm, "end": v(-4099.66, -3573.54) * mm});
            skLineSegment(sketch, "E820", {"start": v(-4099.66, -3573.54) * mm, "end": v(-4112.27, -3573.72) * mm});
            skLineSegment(sketch, "E821", {"start": v(-4112.27, -3573.72) * mm, "end": v(-4124.86, -3574.84) * mm});
            skLineSegment(sketch, "E822", {"start": v(-4124.86, -3574.84) * mm, "end": v(-4137.37, -3576.87) * mm});
            skLineSegment(sketch, "E823", {"start": v(-4137.37, -3576.87) * mm, "end": v(-4149.76, -3579.79) * mm});
            skLineSegment(sketch, "E824", {"start": v(-4149.76, -3579.79) * mm, "end": v(-4417.22, -3244.5) * mm});
            skLineSegment(sketch, "E825", {"start": v(-4417.22, -3244.5) * mm, "end": v(-4658.21, -2888.6) * mm});
            skLineSegment(sketch, "E826", {"start": v(-4658.21, -2888.6) * mm, "end": v(-4871.27, -2513.58) * mm});
            skLineSegment(sketch, "E827", {"start": v(-4871.27, -2513.58) * mm, "end": v(-5054.9, -2120.9) * mm});
            skLineSegment(sketch, "E828", {"start": v(-5054.9, -2120.9) * mm, "end": v(-5207.65, -1712.05) * mm});
            skLineSegment(sketch, "E829", {"start": v(-5207.65, -1712.05) * mm, "end": v(-5328.02, -1288.5) * mm});
            skLineSegment(sketch, "E830", {"start": v(-5328.02, -1288.5) * mm, "end": v(-5414.54, -851.72) * mm});
            skLineSegment(sketch, "E831", {"start": v(-5414.54, -851.72) * mm, "end": v(-5465.74, -403.19) * mm});
            skLineSegment(sketch, "E832", {"start": v(-5465.74, -403.19) * mm, "end": v(-5454.9, -396.5) * mm});
            skLineSegment(sketch, "E833", {"start": v(-5454.9, -396.5) * mm, "end": v(-5444.58, -389.1) * mm});
            skLineSegment(sketch, "E834", {"start": v(-5444.58, -389.1) * mm, "end": v(-5434.87, -380.99) * mm});
            skLineSegment(sketch, "E835", {"start": v(-5434.87, -380.99) * mm, "end": v(-5425.81, -372.19) * mm});
            skLineSegment(sketch, "E836", {"start": v(-5425.81, -372.19) * mm, "end": v(-5417.46, -362.73) * mm});
            skLineSegment(sketch, "E837", {"start": v(-5417.46, -362.73) * mm, "end": v(-5409.86, -352.62) * mm});
            skLineSegment(sketch, "E838", {"start": v(-5409.86, -352.62) * mm, "end": v(-5403.09, -341.89) * mm});
            skLineSegment(sketch, "E839", {"start": v(-5403.09, -341.89) * mm, "end": v(-5397.18, -330.54) * mm});
            skLineSegment(sketch, "E840", {"start": v(-5397.18, -330.54) * mm, "end": v(-5367.68, -343.97) * mm});
            skLineSegment(sketch, "E841", {"start": v(-5367.68, -343.97) * mm, "end": v(-5335.2, -351.82) * mm});
            skLineSegment(sketch, "E842", {"start": v(-5335.2, -351.82) * mm, "end": v(-5301.15, -353.76) * mm});
            skLineSegment(sketch, "E843", {"start": v(-5301.15, -353.76) * mm, "end": v(-5266.97, -349.44) * mm});
            skLineSegment(sketch, "E844", {"start": v(-5266.97, -349.44) * mm, "end": v(-5234.06, -338.54) * mm});
            skLineSegment(sketch, "E845", {"start": v(-5234.06, -338.54) * mm, "end": v(-5203.85, -320.7) * mm});
            skLineSegment(sketch, "E846", {"start": v(-5203.85, -320.7) * mm, "end": v(-5177.77, -295.6) * mm});
            skLineSegment(sketch, "E847", {"start": v(-5177.77, -295.6) * mm, "end": v(-5157.23, -262.9) * mm});
            skLineSegment(sketch, "E848", {"start": v(-5157.23, -262.9) * mm, "end": v(-5077.23, -273.1) * mm});
            skLineSegment(sketch, "E849", {"start": v(-5077.23, -273.1) * mm, "end": v(-4981.6, -287.99) * mm});
            skLineSegment(sketch, "E850", {"start": v(-4981.6, -287.99) * mm, "end": v(-4872.77, -306) * mm});
            skLineSegment(sketch, "E851", {"start": v(-4872.77, -306) * mm, "end": v(-4753.25, -325.61) * mm});
            skLineSegment(sketch, "E852", {"start": v(-4753.25, -325.61) * mm, "end": v(-4625.5, -345.28) * mm});
            skLineSegment(sketch, "E853", {"start": v(-4625.5, -345.28) * mm, "end": v(-4491.98, -363.46) * mm});
            skLineSegment(sketch, "E854", {"start": v(-4491.98, -363.46) * mm, "end": v(-4355.17, -378.62) * mm});
            skLineSegment(sketch, "E855", {"start": v(-4355.17, -378.62) * mm, "end": v(-4217.53, -389.22) * mm});
            skLineSegment(sketch, "E856", {"start": v(-4217.53, -389.22) * mm, "end": v(-4132.41, -393.7) * mm});
            skLineSegment(sketch, "E857", {"start": v(-4132.41, -393.7) * mm, "end": v(-4054.2, -396.16) * mm});
            skLineSegment(sketch, "E858", {"start": v(-4054.2, -396.16) * mm, "end": v(-3982.82, -395.68) * mm});
            skLineSegment(sketch, "E859", {"start": v(-3982.82, -395.68) * mm, "end": v(-3918.18, -391.32) * mm});
            skLineSegment(sketch, "E860", {"start": v(-3918.18, -391.32) * mm, "end": v(-3860.2, -382.16) * mm});
            skLineSegment(sketch, "E861", {"start": v(-3860.2, -382.16) * mm, "end": v(-3808.8, -367.29) * mm});
            skLineSegment(sketch, "E862", {"start": v(-3808.8, -367.29) * mm, "end": v(-3763.9, -345.78) * mm});
            skLineSegment(sketch, "E863", {"start": v(-3763.9, -345.78) * mm, "end": v(-3725.4, -316.7) * mm});
            skLineSegment(sketch, "E864", {"start": v(-3725.4, -316.7) * mm, "end": v(-3697.85, -284.72) * mm});
            skLineSegment(sketch, "E865", {"start": v(-3697.85, -284.72) * mm, "end": v(-3671.26, -314.52) * mm});
            skLineSegment(sketch, "E866", {"start": v(-3671.26, -314.52) * mm, "end": v(-3639.37, -335.7) * mm});
            skLineSegment(sketch, "E867", {"start": v(-3639.37, -335.7) * mm, "end": v(-3603.92, -348.64) * mm});
            skLineSegment(sketch, "E868", {"start": v(-3603.92, -348.64) * mm, "end": v(-3566.66, -353.65) * mm});
            skLineSegment(sketch, "E869", {"start": v(-3566.66, -353.65) * mm, "end": v(-3529.36, -351.09) * mm});
            skLineSegment(sketch, "E870", {"start": v(-3529.36, -351.09) * mm, "end": v(-3493.75, -341.3) * mm});
            skLineSegment(sketch, "E871", {"start": v(-3493.75, -341.3) * mm, "end": v(-3461.59, -324.61) * mm});
            skLineSegment(sketch, "E872", {"start": v(-3461.59, -324.61) * mm, "end": v(-3434.63, -301.38) * mm});
            skLineSegment(sketch, "E873", {"start": v(-3434.63, -301.38) * mm, "end": v(-3386.15, -355.66) * mm});
            skLineSegment(sketch, "E874", {"start": v(-3386.15, -355.66) * mm, "end": v(-3327.84, -394.54) * mm});
            skLineSegment(sketch, "E875", {"start": v(-3327.84, -394.54) * mm, "end": v(-3262.95, -418.08) * mm});
            skLineSegment(sketch, "E876", {"start": v(-3262.95, -418.08) * mm, "end": v(-3194.73, -426.32) * mm});
            skLineSegment(sketch, "E877", {"start": v(-3194.73, -426.32) * mm, "end": v(-3126.43, -419.3) * mm});
            skLineSegment(sketch, "E878", {"start": v(-3126.43, -419.3) * mm, "end": v(-3061.3, -397.06) * mm});
            skLineSegment(sketch, "E879", {"start": v(-3061.3, -397.06) * mm, "end": v(-3002.6, -359.65) * mm});
            skLineSegment(sketch, "E880", {"start": v(-3002.6, -359.65) * mm, "end": v(-2953.58, -307.1) * mm});
            skLineSegment(sketch, "E881", {"start": v(-2953.58, -307.1) * mm, "end": v(-2912.74, -316.58) * mm});
            skLineSegment(sketch, "E882", {"start": v(-2912.74, -316.58) * mm, "end": v(-2815.68, -330.93) * mm});
            skLineSegment(sketch, "E883", {"start": v(-2815.68, -330.93) * mm, "end": v(-2681.25, -348.25) * mm});
            skLineSegment(sketch, "E884", {"start": v(-2681.25, -348.25) * mm, "end": v(-2528.3, -366.66) * mm});
            skLineSegment(sketch, "E885", {"start": v(-2528.3, -366.66) * mm, "end": v(-2375.7, -384.26) * mm});
            skLineSegment(sketch, "E886", {"start": v(-2375.7, -384.26) * mm, "end": v(-2242.25, -399.17) * mm});
            skLineSegment(sketch, "E887", {"start": v(-2242.25, -399.17) * mm, "end": v(-2146.85, -409.5) * mm});
            skLineSegment(sketch, "E888", {"start": v(-2146.85, -409.5) * mm, "end": v(-2108.31, -413.37) * mm});
            skLineSegment(sketch, "E889", {"start": v(-2108.31, -413.37) * mm, "end": v(-1632.95, -413.37) * mm});
            skLineSegment(sketch, "E890", {"start": v(-1632.95, -413.37) * mm, "end": v(-1616.75, -472.92) * mm});
            skLineSegment(sketch, "E891", {"start": v(-1616.75, -472.92) * mm, "end": v(-1598.47, -531.56) * mm});
            skLineSegment(sketch, "E892", {"start": v(-1598.47, -531.56) * mm, "end": v(-1578.15, -589.24) * mm});
            skLineSegment(sketch, "E893", {"start": v(-1578.15, -589.24) * mm, "end": v(-1555.83, -645.93) * mm});
            skLineSegment(sketch, "E894", {"start": v(-1555.83, -645.93) * mm, "end": v(-1531.54, -701.6) * mm});
            skLineSegment(sketch, "E895", {"start": v(-1531.54, -701.6) * mm, "end": v(-1505.3, -756.2) * mm});
            skLineSegment(sketch, "E896", {"start": v(-1505.3, -756.2) * mm, "end": v(-1477.17, -809.7) * mm});
            skLineSegment(sketch, "E897", {"start": v(-1477.17, -809.7) * mm, "end": v(-1447.18, -862.06) * mm});
            skLineSegment(sketch, "E898", {"start": v(-1447.18, -862.06) * mm, "end": v(-1783.37, -1198.26) * mm});
            skLineSegment(sketch, "E899", {"start": v(-1783.37, -1198.26) * mm, "end": v(-1807.96, -1228.35) * mm});
            skLineSegment(sketch, "E900", {"start": v(-1807.96, -1228.35) * mm, "end": v(-1868.13, -1303.25) * mm});
            skLineSegment(sketch, "E901", {"start": v(-1868.13, -1303.25) * mm, "end": v(-1951.9, -1408.26) * mm});
            skLineSegment(sketch, "E902", {"start": v(-1951.9, -1408.26) * mm, "end": v(-2047.3, -1528.71) * mm});
            skLineSegment(sketch, "E903", {"start": v(-2047.3, -1528.71) * mm, "end": v(-2142.37, -1649.92) * mm});
            skLineSegment(sketch, "E904", {"start": v(-2142.37, -1649.92) * mm, "end": v(-2225.1, -1757.2) * mm});
            skLineSegment(sketch, "E905", {"start": v(-2225.1, -1757.2) * mm, "end": v(-2283.54, -1835.89) * mm});
            skLineSegment(sketch, "E906", {"start": v(-2283.54, -1835.89) * mm, "end": v(-2305.7, -1871.28) * mm});
            skLineSegment(sketch, "E907", {"start": v(-2305.7, -1871.28) * mm, "end": v(-2377.28, -1868.85) * mm});
            skLineSegment(sketch, "E908", {"start": v(-2377.28, -1868.85) * mm, "end": v(-2445.15, -1883.87) * mm});
            skLineSegment(sketch, "E909", {"start": v(-2445.15, -1883.87) * mm, "end": v(-2506.94, -1914.1) * mm});
            skLineSegment(sketch, "E910", {"start": v(-2506.94, -1914.1) * mm, "end": v(-2560.28, -1957.33) * mm});
            skLineSegment(sketch, "E911", {"start": v(-2560.28, -1957.33) * mm, "end": v(-2602.79, -2011.32) * mm});
            skLineSegment(sketch, "E912", {"start": v(-2602.79, -2011.32) * mm, "end": v(-2632.1, -2073.85) * mm});
            skLineSegment(sketch, "E913", {"start": v(-2632.1, -2073.85) * mm, "end": v(-2645.87, -2142.68) * mm});
            skLineSegment(sketch, "E914", {"start": v(-2645.87, -2142.68) * mm, "end": v(-2641.69, -2215.6) * mm});
            skLineSegment(sketch, "E915", {"start": v(-2641.69, -2215.6) * mm, "end": v(-2677.58, -2218.37) * mm});
            skLineSegment(sketch, "E916", {"start": v(-2677.58, -2218.37) * mm, "end": v(-2712.3, -2229.56) * mm});
            skLineSegment(sketch, "E917", {"start": v(-2712.3, -2229.56) * mm, "end": v(-2744.4, -2248.1) * mm});
            skLineSegment(sketch, "E918", {"start": v(-2744.4, -2248.1) * mm, "end": v(-2772.45, -2272.93) * mm});
            skLineSegment(sketch, "E919", {"start": v(-2772.45, -2272.93) * mm, "end": v(-2795.05, -2302.97) * mm});
            skLineSegment(sketch, "E920", {"start": v(-2795.05, -2302.97) * mm, "end": v(-2810.76, -2337.16) * mm});
            skLineSegment(sketch, "E921", {"start": v(-2810.76, -2337.16) * mm, "end": v(-2818.17, -2374.44) * mm});
            skLineSegment(sketch, "E922", {"start": v(-2818.17, -2374.44) * mm, "end": v(-2815.83, -2413.72) * mm});
            skLineSegment(sketch, "E923", {"start": v(-2815.83, -2413.72) * mm, "end": v(-2858.15, -2410.37) * mm});
            skLineSegment(sketch, "E924", {"start": v(-2858.15, -2410.37) * mm, "end": v(-2905.95, -2417) * mm});
            skLineSegment(sketch, "E925", {"start": v(-2905.95, -2417) * mm, "end": v(-2952.91, -2433.55) * mm});
            skLineSegment(sketch, "E926", {"start": v(-2952.91, -2433.55) * mm, "end": v(-2999.77, -2459.39) * mm});
            skLineSegment(sketch, "E927", {"start": v(-2999.77, -2459.39) * mm, "end": v(-3047.23, -2493.92) * mm});
            skLineSegment(sketch, "E928", {"start": v(-3047.23, -2493.92) * mm, "end": v(-3096, -2536.55) * mm});
            skLineSegment(sketch, "E929", {"start": v(-3096, -2536.55) * mm, "end": v(-3146.83, -2586.68) * mm});
            skLineSegment(sketch, "E930", {"start": v(-3146.83, -2586.68) * mm, "end": v(-3200.42, -2643.69) * mm});
            skLineSegment(sketch, "E931", {"start": v(-3200.42, -2643.69) * mm, "end": v(-3257.49, -2707) * mm});
            skLineSegment(sketch, "E932", {"start": v(-3257.49, -2707) * mm, "end": v(-3347.23, -2811.9) * mm});
            skLineSegment(sketch, "E933", {"start": v(-3347.23, -2811.9) * mm, "end": v(-3433.2, -2919.42) * mm});
            skLineSegment(sketch, "E934", {"start": v(-3433.2, -2919.42) * mm, "end": v(-3514.72, -3026.72) * mm});
            skLineSegment(sketch, "E935", {"start": v(-3514.72, -3026.72) * mm, "end": v(-3591.15, -3130.97) * mm});
            skLineSegment(sketch, "E936", {"start": v(-3591.15, -3130.97) * mm, "end": v(-3661.81, -3229.33) * mm});
            skLineSegment(sketch, "E937", {"start": v(-3661.81, -3229.33) * mm, "end": v(-3726.06, -3318.97) * mm});
            skLineSegment(sketch, "E938", {"start": v(-3726.06, -3318.97) * mm, "end": v(-3783.22, -3397.06) * mm});
            skLineSegment(sketch, "E939", {"start": v(-3783.22, -3397.06) * mm, "end": v(-3832.64, -3460.76) * mm});
            skLineSegment(sketch, "E940", {"start": v(-3832.64, -3460.76) * mm, "end": v(-3870.51, -3452.16) * mm});
            skLineSegment(sketch, "E941", {"start": v(-3870.51, -3452.16) * mm, "end": v(-3906.85, -3452.98) * mm});
            skLineSegment(sketch, "E942", {"start": v(-3906.85, -3452.98) * mm, "end": v(-3940.89, -3461.92) * mm});
            skLineSegment(sketch, "E943", {"start": v(-3940.89, -3461.92) * mm, "end": v(-3971.87, -3477.67) * mm});
            skLineSegment(sketch, "E944", {"start": v(-3971.87, -3477.67) * mm, "end": v(-3999.05, -3498.92) * mm});
            skLineSegment(sketch, "E945", {"start": v(-3999.05, -3498.92) * mm, "end": v(-4021.66, -3524.37) * mm});
            skLineSegment(sketch, "E946", {"start": v(-4021.66, -3524.37) * mm, "end": v(-4038.94, -3552.7) * mm});
            skLineSegment(sketch, "E947", {"start": v(-4038.94, -3552.7) * mm, "end": v(-4050.14, -3582.6) * mm});
            skLineSegment(sketch, "E948", {"start": v(-4892.4, -3758.22) * mm, "end": v(-4925.62, -3778.9) * mm});
            skLineSegment(sketch, "E949", {"start": v(-4925.62, -3778.9) * mm, "end": v(-4961.12, -3791.7) * mm});
            skLineSegment(sketch, "E950", {"start": v(-4961.12, -3791.7) * mm, "end": v(-4997.86, -3796.82) * mm});
            skLineSegment(sketch, "E951", {"start": v(-4997.86, -3796.82) * mm, "end": v(-5034.77, -3794.47) * mm});
            skLineSegment(sketch, "E952", {"start": v(-5034.77, -3794.47) * mm, "end": v(-5070.79, -3784.84) * mm});
            skLineSegment(sketch, "E953", {"start": v(-5070.79, -3784.84) * mm, "end": v(-5104.85, -3768.13) * mm});
            skLineSegment(sketch, "E954", {"start": v(-5104.85, -3768.13) * mm, "end": v(-5135.9, -3744.52) * mm});
            skLineSegment(sketch, "E955", {"start": v(-5135.9, -3744.52) * mm, "end": v(-5162.87, -3714.23) * mm});
            skLineSegment(sketch, "E956", {"start": v(-5162.87, -3714.23) * mm, "end": v(-5183.73, -3679.52) * mm});
            skLineSegment(sketch, "E957", {"start": v(-5183.73, -3679.52) * mm, "end": v(-5196.44, -3642.7) * mm});
            skLineSegment(sketch, "E958", {"start": v(-5196.44, -3642.7) * mm, "end": v(-5201.3, -3604.96) * mm});
            skLineSegment(sketch, "E959", {"start": v(-5201.3, -3604.96) * mm, "end": v(-5198.59, -3567.45) * mm});
            skLineSegment(sketch, "E960", {"start": v(-5198.59, -3567.45) * mm, "end": v(-5188.6, -3531.34) * mm});
            skLineSegment(sketch, "E961", {"start": v(-5188.6, -3531.34) * mm, "end": v(-5171.65, -3497.8) * mm});
            skLineSegment(sketch, "E962", {"start": v(-5171.65, -3497.8) * mm, "end": v(-5148.02, -3468) * mm});
            skLineSegment(sketch, "E963", {"start": v(-5148.02, -3468) * mm, "end": v(-5117.99, -3443.1) * mm});
            skLineSegment(sketch, "E964", {"start": v(-5117.99, -3443.1) * mm, "end": v(-5083.71, -3424.85) * mm});
            skLineSegment(sketch, "E965", {"start": v(-5083.71, -3424.85) * mm, "end": v(-5047.77, -3413.99) * mm});
            skLineSegment(sketch, "E966", {"start": v(-5047.77, -3413.99) * mm, "end": v(-5011.12, -3410.27) * mm});
            skLineSegment(sketch, "E967", {"start": v(-5011.12, -3410.27) * mm, "end": v(-4974.73, -3413.43) * mm});
            skLineSegment(sketch, "E968", {"start": v(-4974.73, -3413.43) * mm, "end": v(-4939.57, -3423.21) * mm});
            skLineSegment(sketch, "E969", {"start": v(-4939.57, -3423.21) * mm, "end": v(-4906.6, -3439.34) * mm});
            skLineSegment(sketch, "E970", {"start": v(-4906.6, -3439.34) * mm, "end": v(-4876.78, -3461.56) * mm});
            skLineSegment(sketch, "E971", {"start": v(-4876.78, -3461.56) * mm, "end": v(-4851.08, -3489.62) * mm});
            skLineSegment(sketch, "E972", {"start": v(-4851.08, -3489.62) * mm, "end": v(-4831.96, -3522.4) * mm});
            skLineSegment(sketch, "E973", {"start": v(-4831.96, -3522.4) * mm, "end": v(-4820.17, -3557.6) * mm});
            skLineSegment(sketch, "E974", {"start": v(-4820.17, -3557.6) * mm, "end": v(-4815.5, -3594.14) * mm});
            skLineSegment(sketch, "E975", {"start": v(-4815.5, -3594.14) * mm, "end": v(-4817.79, -3630.91) * mm});
            skLineSegment(sketch, "E976", {"start": v(-4817.79, -3630.91) * mm, "end": v(-4826.81, -3666.8) * mm});
            skLineSegment(sketch, "E977", {"start": v(-4826.81, -3666.8) * mm, "end": v(-4842.38, -3700.72) * mm});
            skLineSegment(sketch, "E978", {"start": v(-4842.38, -3700.72) * mm, "end": v(-4864.32, -3731.56) * mm});
            skLineSegment(sketch, "E979", {"start": v(-4864.32, -3731.56) * mm, "end": v(-4892.4, -3758.22) * mm});
            skLineSegment(sketch, "E980", {"start": v(-4149.94, 3579.76) * mm, "end": v(-4137.55, 3576.82) * mm});
            skLineSegment(sketch, "E981", {"start": v(-4137.55, 3576.82) * mm, "end": v(-4125.03, 3574.77) * mm});
            skLineSegment(sketch, "E982", {"start": v(-4125.03, 3574.77) * mm, "end": v(-4112.43, 3573.64) * mm});
            skLineSegment(sketch, "E983", {"start": v(-4112.43, 3573.64) * mm, "end": v(-4099.81, 3573.46) * mm});
            skLineSegment(sketch, "E984", {"start": v(-4099.81, 3573.46) * mm, "end": v(-4087.22, 3574.24) * mm});
            skLineSegment(sketch, "E985", {"start": v(-4087.22, 3574.24) * mm, "end": v(-4074.7, 3576.02) * mm});
            skLineSegment(sketch, "E986", {"start": v(-4074.7, 3576.02) * mm, "end": v(-4062.32, 3578.82) * mm});
            skLineSegment(sketch, "E987", {"start": v(-4062.32, 3578.82) * mm, "end": v(-4050.12, 3582.66) * mm});
            skLineSegment(sketch, "E988", {"start": v(-4050.12, 3582.66) * mm, "end": v(-4038.75, 3552.3) * mm});
            skLineSegment(sketch, "E989", {"start": v(-4038.75, 3552.3) * mm, "end": v(-4021.33, 3523.77) * mm});
            skLineSegment(sketch, "E990", {"start": v(-4021.33, 3523.77) * mm, "end": v(-3998.63, 3498.33) * mm});
            skLineSegment(sketch, "E991", {"start": v(-3998.63, 3498.33) * mm, "end": v(-3971.4, 3477.2) * mm});
            skLineSegment(sketch, "E992", {"start": v(-3971.4, 3477.2) * mm, "end": v(-3940.42, 3461.65) * mm});
            skLineSegment(sketch, "E993", {"start": v(-3940.42, 3461.65) * mm, "end": v(-3906.45, 3452.9) * mm});
            skLineSegment(sketch, "E994", {"start": v(-3906.45, 3452.9) * mm, "end": v(-3870.26, 3452.2) * mm});
            skLineSegment(sketch, "E995", {"start": v(-3870.26, 3452.2) * mm, "end": v(-3832.62, 3460.81) * mm});
            skLineSegment(sketch, "E996", {"start": v(-3832.62, 3460.81) * mm, "end": v(-3783.27, 3397.04) * mm});
            skLineSegment(sketch, "E997", {"start": v(-3783.27, 3397.04) * mm, "end": v(-3726.16, 3318.9) * mm});
            skLineSegment(sketch, "E998", {"start": v(-3726.16, 3318.9) * mm, "end": v(-3661.96, 3229.2) * mm});
            skLineSegment(sketch, "E999", {"start": v(-3661.96, 3229.2) * mm, "end": v(-3591.31, 3130.83) * mm});
            skLineSegment(sketch, "E1000", {"start": v(-3591.31, 3130.83) * mm, "end": v(-3514.88, 3026.59) * mm});
            skLineSegment(sketch, "E1001", {"start": v(-3514.88, 3026.59) * mm, "end": v(-3433.33, 2919.32) * mm});
            skLineSegment(sketch, "E1002", {"start": v(-3433.33, 2919.32) * mm, "end": v(-3347.3, 2811.86) * mm});
            skLineSegment(sketch, "E1003", {"start": v(-3347.3, 2811.86) * mm, "end": v(-3257.46, 2707.04) * mm});
            skLineSegment(sketch, "E1004", {"start": v(-3257.46, 2707.04) * mm, "end": v(-3200.45, 2643.68) * mm});
            skLineSegment(sketch, "E1005", {"start": v(-3200.45, 2643.68) * mm, "end": v(-3146.88, 2586.64) * mm});
            skLineSegment(sketch, "E1006", {"start": v(-3146.88, 2586.64) * mm, "end": v(-3096.07, 2536.5) * mm});
            skLineSegment(sketch, "E1007", {"start": v(-3096.07, 2536.5) * mm, "end": v(-3047.28, 2493.88) * mm});
            skLineSegment(sketch, "E1008", {"start": v(-3047.28, 2493.88) * mm, "end": v(-2999.8, 2459.36) * mm});
            skLineSegment(sketch, "E1009", {"start": v(-2999.8, 2459.36) * mm, "end": v(-2952.94, 2433.53) * mm});
            skLineSegment(sketch, "E1010", {"start": v(-2952.94, 2433.53) * mm, "end": v(-2905.98, 2416.98) * mm});
            skLineSegment(sketch, "E1011", {"start": v(-2905.98, 2416.98) * mm, "end": v(-2858.2, 2410.32) * mm});
            skLineSegment(sketch, "E1012", {"start": v(-2858.2, 2410.32) * mm, "end": v(-2816.11, 2413.44) * mm});
            skLineSegment(sketch, "E1013", {"start": v(-2816.11, 2413.44) * mm, "end": v(-2818.38, 2373.58) * mm});
            skLineSegment(sketch, "E1014", {"start": v(-2818.38, 2373.58) * mm, "end": v(-2810.8, 2336.04) * mm});
            skLineSegment(sketch, "E1015", {"start": v(-2810.8, 2336.04) * mm, "end": v(-2794.88, 2301.84) * mm});
            skLineSegment(sketch, "E1016", {"start": v(-2794.88, 2301.84) * mm, "end": v(-2772.08, 2271.95) * mm});
            skLineSegment(sketch, "E1017", {"start": v(-2772.08, 2271.95) * mm, "end": v(-2743.88, 2247.38) * mm});
            skLineSegment(sketch, "E1018", {"start": v(-2743.88, 2247.38) * mm, "end": v(-2711.78, 2229.13) * mm});
            skLineSegment(sketch, "E1019", {"start": v(-2711.78, 2229.13) * mm, "end": v(-2677.25, 2218.19) * mm});
            skLineSegment(sketch, "E1020", {"start": v(-2677.25, 2218.19) * mm, "end": v(-2641.77, 2215.55) * mm});
            skLineSegment(sketch, "E1021", {"start": v(-2641.77, 2215.55) * mm, "end": v(-2645.86, 2142.9) * mm});
            skLineSegment(sketch, "E1022", {"start": v(-2645.86, 2142.9) * mm, "end": v(-2632.13, 2074.16) * mm});
            skLineSegment(sketch, "E1023", {"start": v(-2632.13, 2074.16) * mm, "end": v(-2602.9, 2011.63) * mm});
            skLineSegment(sketch, "E1024", {"start": v(-2602.9, 2011.63) * mm, "end": v(-2560.48, 1957.56) * mm});
            skLineSegment(sketch, "E1025", {"start": v(-2560.48, 1957.56) * mm, "end": v(-2507.22, 1914.22) * mm});
            skLineSegment(sketch, "E1026", {"start": v(-2507.22, 1914.22) * mm, "end": v(-2445.44, 1883.9) * mm});
            skLineSegment(sketch, "E1027", {"start": v(-2445.44, 1883.9) * mm, "end": v(-2377.47, 1868.84) * mm});
            skLineSegment(sketch, "E1028", {"start": v(-2377.47, 1868.84) * mm, "end": v(-2305.65, 1871.33) * mm});
            skLineSegment(sketch, "E1029", {"start": v(-2305.65, 1871.33) * mm, "end": v(-2283.47, 1835.75) * mm});
            skLineSegment(sketch, "E1030", {"start": v(-2283.47, 1835.75) * mm, "end": v(-2224.99, 1756.98) * mm});
            skLineSegment(sketch, "E1031", {"start": v(-2224.99, 1756.98) * mm, "end": v(-2142.18, 1649.68) * mm});
            skLineSegment(sketch, "E1032", {"start": v(-2142.18, 1649.68) * mm, "end": v(-2047.05, 1528.51) * mm});
            skLineSegment(sketch, "E1033", {"start": v(-2047.05, 1528.51) * mm, "end": v(-1951.58, 1408.15) * mm});
            skLineSegment(sketch, "E1034", {"start": v(-1951.58, 1408.15) * mm, "end": v(-1867.78, 1303.25) * mm});
            skLineSegment(sketch, "E1035", {"start": v(-1867.78, 1303.25) * mm, "end": v(-1807.62, 1228.48) * mm});
            skLineSegment(sketch, "E1036", {"start": v(-1807.62, 1228.48) * mm, "end": v(-1783.12, 1198.51) * mm});
            skLineSegment(sketch, "E1037", {"start": v(-1783.12, 1198.51) * mm, "end": v(-1446.97, 862.4) * mm});
            skLineSegment(sketch, "E1038", {"start": v(-1446.97, 862.4) * mm, "end": v(-1477, 810.03) * mm});
            skLineSegment(sketch, "E1039", {"start": v(-1477, 810.03) * mm, "end": v(-1505.14, 756.53) * mm});
            skLineSegment(sketch, "E1040", {"start": v(-1505.14, 756.53) * mm, "end": v(-1531.39, 701.93) * mm});
            skLineSegment(sketch, "E1041", {"start": v(-1531.39, 701.93) * mm, "end": v(-1555.7, 646.27) * mm});
            skLineSegment(sketch, "E1042", {"start": v(-1555.7, 646.27) * mm, "end": v(-1578.04, 589.59) * mm});
            skLineSegment(sketch, "E1043", {"start": v(-1578.04, 589.59) * mm, "end": v(-1598.37, 531.9) * mm});
            skLineSegment(sketch, "E1044", {"start": v(-1598.37, 531.9) * mm, "end": v(-1616.66, 473.28) * mm});
            skLineSegment(sketch, "E1045", {"start": v(-1616.66, 473.28) * mm, "end": v(-1632.88, 413.73) * mm});
            skLineSegment(sketch, "E1046", {"start": v(-1632.88, 413.73) * mm, "end": v(-2108.31, 413.73) * mm});
            skLineSegment(sketch, "E1047", {"start": v(-2108.31, 413.73) * mm, "end": v(-2146.99, 409.83) * mm});
            skLineSegment(sketch, "E1048", {"start": v(-2146.99, 409.83) * mm, "end": v(-2242.5, 399.42) * mm});
            skLineSegment(sketch, "E1049", {"start": v(-2242.5, 399.42) * mm, "end": v(-2376, 384.4) * mm});
            skLineSegment(sketch, "E1050", {"start": v(-2376, 384.4) * mm, "end": v(-2528.64, 366.7) * mm});
            skLineSegment(sketch, "E1051", {"start": v(-2528.64, 366.7) * mm, "end": v(-2681.57, 348.2) * mm});
            skLineSegment(sketch, "E1052", {"start": v(-2681.57, 348.2) * mm, "end": v(-2815.93, 330.84) * mm});
            skLineSegment(sketch, "E1053", {"start": v(-2815.93, 330.84) * mm, "end": v(-2912.88, 316.53) * mm});
            skLineSegment(sketch, "E1054", {"start": v(-2912.88, 316.53) * mm, "end": v(-2953.58, 307.17) * mm});
            skLineSegment(sketch, "E1055", {"start": v(-2953.58, 307.17) * mm, "end": v(-3002.47, 359.5) * mm});
            skLineSegment(sketch, "E1056", {"start": v(-3002.47, 359.5) * mm, "end": v(-3061.08, 396.88) * mm});
            skLineSegment(sketch, "E1057", {"start": v(-3061.08, 396.88) * mm, "end": v(-3126.15, 419.2) * mm});
            skLineSegment(sketch, "E1058", {"start": v(-3126.15, 419.2) * mm, "end": v(-3194.43, 426.35) * mm});
            skLineSegment(sketch, "E1059", {"start": v(-3194.43, 426.35) * mm, "end": v(-3262.67, 418.23) * mm});
            skLineSegment(sketch, "E1060", {"start": v(-3262.67, 418.23) * mm, "end": v(-3327.62, 394.75) * mm});
            skLineSegment(sketch, "E1061", {"start": v(-3327.62, 394.75) * mm, "end": v(-3386.02, 355.8) * mm});
            skLineSegment(sketch, "E1062", {"start": v(-3386.02, 355.8) * mm, "end": v(-3434.63, 301.28) * mm});
            skLineSegment(sketch, "E1063", {"start": v(-3434.63, 301.28) * mm, "end": v(-3461.96, 324.7) * mm});
            skLineSegment(sketch, "E1064", {"start": v(-3461.96, 324.7) * mm, "end": v(-3494.42, 341.34) * mm});
            skLineSegment(sketch, "E1065", {"start": v(-3494.42, 341.34) * mm, "end": v(-3530.22, 350.93) * mm});
            skLineSegment(sketch, "E1066", {"start": v(-3530.22, 350.93) * mm, "end": v(-3567.62, 353.22) * mm});
            skLineSegment(sketch, "E1067", {"start": v(-3567.62, 353.22) * mm, "end": v(-3604.84, 347.96) * mm});
            skLineSegment(sketch, "E1068", {"start": v(-3604.84, 347.96) * mm, "end": v(-3640.13, 334.9) * mm});
            skLineSegment(sketch, "E1069", {"start": v(-3640.13, 334.9) * mm, "end": v(-3671.72, 313.77) * mm});
            skLineSegment(sketch, "E1070", {"start": v(-3671.72, 313.77) * mm, "end": v(-3697.85, 284.34) * mm});
            skLineSegment(sketch, "E1071", {"start": v(-3697.85, 284.34) * mm, "end": v(-3725.4, 316.62) * mm});
            skLineSegment(sketch, "E1072", {"start": v(-3725.4, 316.62) * mm, "end": v(-3763.9, 345.73) * mm});
            skLineSegment(sketch, "E1073", {"start": v(-3763.9, 345.73) * mm, "end": v(-3808.8, 367.25) * mm});
            skLineSegment(sketch, "E1074", {"start": v(-3808.8, 367.25) * mm, "end": v(-3860.2, 382.1) * mm});
            skLineSegment(sketch, "E1075", {"start": v(-3860.2, 382.1) * mm, "end": v(-3918.18, 391.25) * mm});
            skLineSegment(sketch, "E1076", {"start": v(-3918.18, 391.25) * mm, "end": v(-3982.82, 395.6) * mm});
            skLineSegment(sketch, "E1077", {"start": v(-3982.82, 395.6) * mm, "end": v(-4054.2, 396.1) * mm});
            skLineSegment(sketch, "E1078", {"start": v(-4054.2, 396.1) * mm, "end": v(-4132.41, 393.67) * mm});
            skLineSegment(sketch, "E1079", {"start": v(-4132.41, 393.67) * mm, "end": v(-4217.53, 389.27) * mm});
            skLineSegment(sketch, "E1080", {"start": v(-4217.53, 389.27) * mm, "end": v(-4355.17, 378.54) * mm});
            skLineSegment(sketch, "E1081", {"start": v(-4355.17, 378.54) * mm, "end": v(-4491.98, 363.3) * mm});
            skLineSegment(sketch, "E1082", {"start": v(-4491.98, 363.3) * mm, "end": v(-4625.5, 345.07) * mm});
            skLineSegment(sketch, "E1083", {"start": v(-4625.5, 345.07) * mm, "end": v(-4753.25, 325.4) * mm});
            skLineSegment(sketch, "E1084", {"start": v(-4753.25, 325.4) * mm, "end": v(-4872.77, 305.82) * mm});
            skLineSegment(sketch, "E1085", {"start": v(-4872.77, 305.82) * mm, "end": v(-4981.6, 287.86) * mm});
            skLineSegment(sketch, "E1086", {"start": v(-4981.6, 287.86) * mm, "end": v(-5077.23, 273.07) * mm});
            skLineSegment(sketch, "E1087", {"start": v(-5077.23, 273.07) * mm, "end": v(-5157.23, 262.98) * mm});
            skLineSegment(sketch, "E1088", {"start": v(-5157.23, 262.98) * mm, "end": v(-5177.92, 295.83) * mm});
            skLineSegment(sketch, "E1089", {"start": v(-5177.92, 295.83) * mm, "end": v(-5204.19, 320.94) * mm});
            skLineSegment(sketch, "E1090", {"start": v(-5204.19, 320.94) * mm, "end": v(-5234.58, 338.68) * mm});
            skLineSegment(sketch, "E1091", {"start": v(-5234.58, 338.68) * mm, "end": v(-5267.62, 349.45) * mm});
            skLineSegment(sketch, "E1092", {"start": v(-5267.62, 349.45) * mm, "end": v(-5301.87, 353.64) * mm});
            skLineSegment(sketch, "E1093", {"start": v(-5301.87, 353.64) * mm, "end": v(-5335.85, 351.63) * mm});
            skLineSegment(sketch, "E1094", {"start": v(-5335.85, 351.63) * mm, "end": v(-5368.1, 343.82) * mm});
            skLineSegment(sketch, "E1095", {"start": v(-5368.1, 343.82) * mm, "end": v(-5397.18, 330.6) * mm});
            skLineSegment(sketch, "E1096", {"start": v(-5397.18, 330.6) * mm, "end": v(-5403.09, 341.86) * mm});
            skLineSegment(sketch, "E1097", {"start": v(-5403.09, 341.86) * mm, "end": v(-5409.87, 352.54) * mm});
            skLineSegment(sketch, "E1098", {"start": v(-5409.87, 352.54) * mm, "end": v(-5417.46, 362.62) * mm});
            skLineSegment(sketch, "E1099", {"start": v(-5417.46, 362.62) * mm, "end": v(-5425.82, 372.06) * mm});
            skLineSegment(sketch, "E1100", {"start": v(-5425.82, 372.06) * mm, "end": v(-5434.88, 380.85) * mm});
            skLineSegment(sketch, "E1101", {"start": v(-5434.88, 380.85) * mm, "end": v(-5444.6, 388.97) * mm});
            skLineSegment(sketch, "E1102", {"start": v(-5444.6, 388.97) * mm, "end": v(-5454.9, 396.38) * mm});
            skLineSegment(sketch, "E1103", {"start": v(-5454.9, 396.38) * mm, "end": v(-5465.74, 403.09) * mm});
            skLineSegment(sketch, "E1104", {"start": v(-5465.74, 403.09) * mm, "end": v(-5414.56, 851.63) * mm});
            skLineSegment(sketch, "E1105", {"start": v(-5414.56, 851.63) * mm, "end": v(-5328.06, 1288.43) * mm});
            skLineSegment(sketch, "E1106", {"start": v(-5328.06, 1288.43) * mm, "end": v(-5207.71, 1712) * mm});
            skLineSegment(sketch, "E1107", {"start": v(-5207.71, 1712) * mm, "end": v(-5055, 2120.86) * mm});
            skLineSegment(sketch, "E1108", {"start": v(-5055, 2120.86) * mm, "end": v(-4871.38, 2513.54) * mm});
            skLineSegment(sketch, "E1109", {"start": v(-4871.38, 2513.54) * mm, "end": v(-4658.35, 2888.57) * mm});
            skLineSegment(sketch, "E1110", {"start": v(-4658.35, 2888.57) * mm, "end": v(-4417.38, 3244.47) * mm});
            skLineSegment(sketch, "E1111", {"start": v(-4417.38, 3244.47) * mm, "end": v(-4149.94, 3579.76) * mm});
            skLineSegment(sketch, "E1112", {"start": v(-5675.72, 1873.75) * mm, "end": v(-5691.01, 1839.03) * mm});
            skLineSegment(sketch, "E1113", {"start": v(-5691.01, 1839.03) * mm, "end": v(-5712.57, 1808.8) * mm});
            skLineSegment(sketch, "E1114", {"start": v(-5712.57, 1808.8) * mm, "end": v(-5739.38, 1783.57) * mm});
            skLineSegment(sketch, "E1115", {"start": v(-5739.38, 1783.57) * mm, "end": v(-5770.46, 1763.8) * mm});
            skLineSegment(sketch, "E1116", {"start": v(-5770.46, 1763.8) * mm, "end": v(-5804.81, 1750.02) * mm});
            skLineSegment(sketch, "E1117", {"start": v(-5804.81, 1750.02) * mm, "end": v(-5841.44, 1742.69) * mm});
            skLineSegment(sketch, "E1118", {"start": v(-5841.44, 1742.69) * mm, "end": v(-5879.33, 1742.31) * mm});
            skLineSegment(sketch, "E1119", {"start": v(-5879.33, 1742.31) * mm, "end": v(-5917.5, 1749.39) * mm});
            skLineSegment(sketch, "E1120", {"start": v(-5917.5, 1749.39) * mm, "end": v(-5953.66, 1764.07) * mm});
            skLineSegment(sketch, "E1121", {"start": v(-5953.66, 1764.07) * mm, "end": v(-5984.83, 1785.25) * mm});
            skLineSegment(sketch, "E1122", {"start": v(-5984.83, 1785.25) * mm, "end": v(-6010.55, 1811.95) * mm});
            skLineSegment(sketch, "E1123", {"start": v(-6010.55, 1811.95) * mm, "end": v(-6030.34, 1843.2) * mm});
            skLineSegment(sketch, "E1124", {"start": v(-6030.34, 1843.2) * mm, "end": v(-6043.72, 1878) * mm});
            skLineSegment(sketch, "E1125", {"start": v(-6043.72, 1878) * mm, "end": v(-6050.23, 1915.4) * mm});
            skLineSegment(sketch, "E1126", {"start": v(-6050.23, 1915.4) * mm, "end": v(-6049.37, 1954.4) * mm});
            skLineSegment(sketch, "E1127", {"start": v(-6049.37, 1954.4) * mm, "end": v(-6040.7, 1994.04) * mm});
            skLineSegment(sketch, "E1128", {"start": v(-6040.7, 1994.04) * mm, "end": v(-6024.87, 2031.34) * mm});
            skLineSegment(sketch, "E1129", {"start": v(-6024.87, 2031.34) * mm, "end": v(-6002.57, 2063.27) * mm});
            skLineSegment(sketch, "E1130", {"start": v(-6002.57, 2063.27) * mm, "end": v(-5974.92, 2089.4) * mm});
            skLineSegment(sketch, "E1131", {"start": v(-5974.92, 2089.4) * mm, "end": v(-5943.01, 2109.27) * mm});
            skLineSegment(sketch, "E1132", {"start": v(-5943.01, 2109.27) * mm, "end": v(-5907.96, 2122.42) * mm});
            skLineSegment(sketch, "E1133", {"start": v(-5907.96, 2122.42) * mm, "end": v(-5870.87, 2128.41) * mm});
            skLineSegment(sketch, "E1134", {"start": v(-5870.87, 2128.41) * mm, "end": v(-5832.86, 2126.78) * mm});
            skLineSegment(sketch, "E1135", {"start": v(-5832.86, 2126.78) * mm, "end": v(-5795.02, 2117.08) * mm});
            skLineSegment(sketch, "E1136", {"start": v(-5795.02, 2117.08) * mm, "end": v(-5760.16, 2100.07) * mm});
            skLineSegment(sketch, "E1137", {"start": v(-5760.16, 2100.07) * mm, "end": v(-5730.26, 2077.36) * mm});
            skLineSegment(sketch, "E1138", {"start": v(-5730.26, 2077.36) * mm, "end": v(-5705.71, 2049.89) * mm});
            skLineSegment(sketch, "E1139", {"start": v(-5705.71, 2049.89) * mm, "end": v(-5686.86, 2018.58) * mm});
            skLineSegment(sketch, "E1140", {"start": v(-5686.86, 2018.58) * mm, "end": v(-5674.07, 1984.37) * mm});
            skLineSegment(sketch, "E1141", {"start": v(-5674.07, 1984.37) * mm, "end": v(-5667.71, 1948.2) * mm});
            skLineSegment(sketch, "E1142", {"start": v(-5667.71, 1948.2) * mm, "end": v(-5668.14, 1911.02) * mm});
            skLineSegment(sketch, "E1143", {"start": v(-5668.14, 1911.02) * mm, "end": v(-5675.72, 1873.75) * mm});
            skLineSegment(sketch, "E1144", {"start": v(-5814.17, -2062.44) * mm, "end": v(-5851.82, -2071.72) * mm});
            skLineSegment(sketch, "E1145", {"start": v(-5851.82, -2071.72) * mm, "end": v(-5889.68, -2072.95) * mm});
            skLineSegment(sketch, "E1146", {"start": v(-5889.68, -2072.95) * mm, "end": v(-5926.67, -2066.62) * mm});
            skLineSegment(sketch, "E1147", {"start": v(-5926.67, -2066.62) * mm, "end": v(-5961.68, -2053.17) * mm});
            skLineSegment(sketch, "E1148", {"start": v(-5961.68, -2053.17) * mm, "end": v(-5993.64, -2033.1) * mm});
            skLineSegment(sketch, "E1149", {"start": v(-5993.64, -2033.1) * mm, "end": v(-6021.44, -2006.85) * mm});
            skLineSegment(sketch, "E1150", {"start": v(-6021.44, -2006.85) * mm, "end": v(-6044, -1974.9) * mm});
            skLineSegment(sketch, "E1151", {"start": v(-6044, -1974.9) * mm, "end": v(-6060.2, -1937.7) * mm});
            skLineSegment(sketch, "E1152", {"start": v(-6060.2, -1937.7) * mm, "end": v(-6068.05, -1897.84) * mm});
            skLineSegment(sketch, "E1153", {"start": v(-6068.05, -1897.84) * mm, "end": v(-6068.07, -1858.68) * mm});
            skLineSegment(sketch, "E1154", {"start": v(-6068.07, -1858.68) * mm, "end": v(-6060.77, -1821.2) * mm});
            skLineSegment(sketch, "E1155", {"start": v(-6060.77, -1821.2) * mm, "end": v(-6046.68, -1786.4) * mm});
            skLineSegment(sketch, "E1156", {"start": v(-6046.68, -1786.4) * mm, "end": v(-6026.3, -1755.23) * mm});
            skLineSegment(sketch, "E1157", {"start": v(-6026.3, -1755.23) * mm, "end": v(-6000.17, -1728.7) * mm});
            skLineSegment(sketch, "E1158", {"start": v(-6000.17, -1728.7) * mm, "end": v(-5968.77, -1707.78) * mm});
            skLineSegment(sketch, "E1159", {"start": v(-5968.77, -1707.78) * mm, "end": v(-5932.64, -1693.46) * mm});
            skLineSegment(sketch, "E1160", {"start": v(-5932.64, -1693.46) * mm, "end": v(-5894.25, -1686.69) * mm});
            skLineSegment(sketch, "E1161", {"start": v(-5894.25, -1686.69) * mm, "end": v(-5856.4, -1687.42) * mm});
            skLineSegment(sketch, "E1162", {"start": v(-5856.4, -1687.42) * mm, "end": v(-5820.03, -1695.13) * mm});
            skLineSegment(sketch, "E1163", {"start": v(-5820.03, -1695.13) * mm, "end": v(-5786.11, -1709.33) * mm});
            skLineSegment(sketch, "E1164", {"start": v(-5786.11, -1709.33) * mm, "end": v(-5755.6, -1729.49) * mm});
            skLineSegment(sketch, "E1165", {"start": v(-5755.6, -1729.49) * mm, "end": v(-5729.48, -1755.1) * mm});
            skLineSegment(sketch, "E1166", {"start": v(-5729.48, -1755.1) * mm, "end": v(-5708.68, -1785.66) * mm});
            skLineSegment(sketch, "E1167", {"start": v(-5708.68, -1785.66) * mm, "end": v(-5694.18, -1820.66) * mm});
            skLineSegment(sketch, "E1168", {"start": v(-5694.18, -1820.66) * mm, "end": v(-5686.21, -1857.75) * mm});
            skLineSegment(sketch, "E1169", {"start": v(-5686.21, -1857.75) * mm, "end": v(-5685.57, -1894.75) * mm});
            skLineSegment(sketch, "E1170", {"start": v(-5685.57, -1894.75) * mm, "end": v(-5691.87, -1930.73) * mm});
            skLineSegment(sketch, "E1171", {"start": v(-5691.87, -1930.73) * mm, "end": v(-5704.74, -1964.75) * mm});
            skLineSegment(sketch, "E1172", {"start": v(-5704.74, -1964.75) * mm, "end": v(-5723.78, -1995.87) * mm});
            skLineSegment(sketch, "E1173", {"start": v(-5723.78, -1995.87) * mm, "end": v(-5748.62, -2023.16) * mm});
            skLineSegment(sketch, "E1174", {"start": v(-5748.62, -2023.16) * mm, "end": v(-5778.88, -2045.66) * mm});
            skLineSegment(sketch, "E1175", {"start": v(-5778.88, -2045.66) * mm, "end": v(-5814.17, -2062.44) * mm});
            skLineSegment(sketch, "E1176", {"start": v(-6359.56, 29.88) * mm, "end": v(-6355.22, 70.19) * mm});
            skLineSegment(sketch, "E1177", {"start": v(-6355.22, 70.19) * mm, "end": v(-6343.62, 107.42) * mm});
            skLineSegment(sketch, "E1178", {"start": v(-6343.62, 107.42) * mm, "end": v(-6325.54, 140.79) * mm});
            skLineSegment(sketch, "E1179", {"start": v(-6325.54, 140.79) * mm, "end": v(-6301.76, 169.53) * mm});
            skLineSegment(sketch, "E1180", {"start": v(-6301.76, 169.53) * mm, "end": v(-6273.06, 192.87) * mm});
            skLineSegment(sketch, "E1181", {"start": v(-6273.06, 192.87) * mm, "end": v(-6240.24, 210.03) * mm});
            skLineSegment(sketch, "E1182", {"start": v(-6240.24, 210.03) * mm, "end": v(-6204.07, 220.23) * mm});
            skLineSegment(sketch, "E1183", {"start": v(-6204.07, 220.23) * mm, "end": v(-6165.33, 222.7) * mm});
            skLineSegment(sketch, "E1184", {"start": v(-6165.33, 222.7) * mm, "end": v(-6126.68, 217.29) * mm});
            skLineSegment(sketch, "E1185", {"start": v(-6126.68, 217.29) * mm, "end": v(-6090.75, 204.9) * mm});
            skLineSegment(sketch, "E1186", {"start": v(-6090.75, 204.9) * mm, "end": v(-6058.31, 186.31) * mm});
            skLineSegment(sketch, "E1187", {"start": v(-6058.31, 186.31) * mm, "end": v(-6030.13, 162.32) * mm});
            skLineSegment(sketch, "E1188", {"start": v(-6030.13, 162.32) * mm, "end": v(-6006.97, 133.7) * mm});
            skLineSegment(sketch, "E1189", {"start": v(-6006.97, 133.7) * mm, "end": v(-5989.6, 101.22) * mm});
            skLineSegment(sketch, "E1190", {"start": v(-5989.6, 101.22) * mm, "end": v(-5978.78, 65.69) * mm});
            skLineSegment(sketch, "E1191", {"start": v(-5978.78, 65.69) * mm, "end": v(-5975.29, 27.88) * mm});
            skLineSegment(sketch, "E1192", {"start": v(-5975.29, 27.88) * mm, "end": v(-5979.97, -9.9) * mm});
            skLineSegment(sketch, "E1193", {"start": v(-5979.97, -9.9) * mm, "end": v(-5991.44, -45.31) * mm});
            skLineSegment(sketch, "E1194", {"start": v(-5991.44, -45.31) * mm, "end": v(-6009.04, -77.59) * mm});
            skLineSegment(sketch, "E1195", {"start": v(-6009.04, -77.59) * mm, "end": v(-6032.1, -105.96) * mm});
            skLineSegment(sketch, "E1196", {"start": v(-6032.1, -105.96) * mm, "end": v(-6060, -129.64) * mm});
            skLineSegment(sketch, "E1197", {"start": v(-6060, -129.64) * mm, "end": v(-6092.05, -147.87) * mm});
            skLineSegment(sketch, "E1198", {"start": v(-6092.05, -147.87) * mm, "end": v(-6127.6, -159.88) * mm});
            skLineSegment(sketch, "E1199", {"start": v(-6127.6, -159.88) * mm, "end": v(-6165.99, -164.88) * mm});
            skLineSegment(sketch, "E1200", {"start": v(-6165.99, -164.88) * mm, "end": v(-6205, -162.03) * mm});
            skLineSegment(sketch, "E1201", {"start": v(-6205, -162.03) * mm, "end": v(-6241.58, -151.47) * mm});
            skLineSegment(sketch, "E1202", {"start": v(-6241.58, -151.47) * mm, "end": v(-6274.8, -133.99) * mm});
            skLineSegment(sketch, "E1203", {"start": v(-6274.8, -133.99) * mm, "end": v(-6303.8, -110.36) * mm});
            skLineSegment(sketch, "E1204", {"start": v(-6303.8, -110.36) * mm, "end": v(-6327.65, -81.38) * mm});
            skLineSegment(sketch, "E1205", {"start": v(-6327.65, -81.38) * mm, "end": v(-6345.5, -47.83) * mm});
            skLineSegment(sketch, "E1206", {"start": v(-6345.5, -47.83) * mm, "end": v(-6356.43, -10.48) * mm});
            skLineSegment(sketch, "E1207", {"start": v(-6356.43, -10.48) * mm, "end": v(-6359.56, 29.88) * mm});
            skLineSegment(sketch, "E1208", {"start": v(-5129.03, 3763.38) * mm, "end": v(-5101.35, 3793.1) * mm});
            skLineSegment(sketch, "E1209", {"start": v(-5101.35, 3793.1) * mm, "end": v(-5069.63, 3816.07) * mm});
            skLineSegment(sketch, "E1210", {"start": v(-5069.63, 3816.07) * mm, "end": v(-5034.98, 3832.14) * mm});
            skLineSegment(sketch, "E1211", {"start": v(-5034.98, 3832.14) * mm, "end": v(-4998.5, 3841.15) * mm});
            skLineSegment(sketch, "E1212", {"start": v(-4998.5, 3841.15) * mm, "end": v(-4961.3, 3842.94) * mm});
            skLineSegment(sketch, "E1213", {"start": v(-4961.3, 3842.94) * mm, "end": v(-4924.46, 3837.35) * mm});
            skLineSegment(sketch, "E1214", {"start": v(-4924.46, 3837.35) * mm, "end": v(-4889.08, 3824.22) * mm});
            skLineSegment(sketch, "E1215", {"start": v(-4889.08, 3824.22) * mm, "end": v(-4856.26, 3803.38) * mm});
            skLineSegment(sketch, "E1216", {"start": v(-4856.26, 3803.38) * mm, "end": v(-4828.24, 3776.3) * mm});
            skLineSegment(sketch, "E1217", {"start": v(-4828.24, 3776.3) * mm, "end": v(-4806.61, 3745.23) * mm});
            skLineSegment(sketch, "E1218", {"start": v(-4806.61, 3745.23) * mm, "end": v(-4791.52, 3711.27) * mm});
            skLineSegment(sketch, "E1219", {"start": v(-4791.52, 3711.27) * mm, "end": v(-4783.12, 3675.5) * mm});
            skLineSegment(sketch, "E1220", {"start": v(-4783.12, 3675.5) * mm, "end": v(-4781.55, 3638.99) * mm});
            skLineSegment(sketch, "E1221", {"start": v(-4781.55, 3638.99) * mm, "end": v(-4786.98, 3602.8) * mm});
            skLineSegment(sketch, "E1222", {"start": v(-4786.98, 3602.8) * mm, "end": v(-4799.55, 3568.04) * mm});
            skLineSegment(sketch, "E1223", {"start": v(-4799.55, 3568.04) * mm, "end": v(-4819.4, 3535.77) * mm});
            skLineSegment(sketch, "E1224", {"start": v(-4819.4, 3535.77) * mm, "end": v(-4844.57, 3507.4) * mm});
            skLineSegment(sketch, "E1225", {"start": v(-4844.57, 3507.4) * mm, "end": v(-4874.07, 3485.1) * mm});
            skLineSegment(sketch, "E1226", {"start": v(-4874.07, 3485.1) * mm, "end": v(-4906.9, 3469.08) * mm});
            skLineSegment(sketch, "E1227", {"start": v(-4906.9, 3469.08) * mm, "end": v(-4942.06, 3459.55) * mm});
            skLineSegment(sketch, "E1228", {"start": v(-4942.06, 3459.55) * mm, "end": v(-4978.5, 3456.75) * mm});
            skLineSegment(sketch, "E1229", {"start": v(-4978.5, 3456.75) * mm, "end": v(-5015.24, 3460.9) * mm});
            skLineSegment(sketch, "E1230", {"start": v(-5015.24, 3460.9) * mm, "end": v(-5051.25, 3472.21) * mm});
            skLineSegment(sketch, "E1231", {"start": v(-5051.25, 3472.21) * mm, "end": v(-5085.52, 3490.91) * mm});
            skLineSegment(sketch, "E1232", {"start": v(-5085.52, 3490.91) * mm, "end": v(-5115.15, 3515.98) * mm});
            skLineSegment(sketch, "E1233", {"start": v(-5115.15, 3515.98) * mm, "end": v(-5138.33, 3545.89) * mm});
            skLineSegment(sketch, "E1234", {"start": v(-5138.33, 3545.89) * mm, "end": v(-5154.84, 3579.5) * mm});
            skLineSegment(sketch, "E1235", {"start": v(-5154.84, 3579.5) * mm, "end": v(-5164.44, 3615.7) * mm});
            skLineSegment(sketch, "E1236", {"start": v(-5164.44, 3615.7) * mm, "end": v(-5166.9, 3653.32) * mm});
            skLineSegment(sketch, "E1237", {"start": v(-5166.9, 3653.32) * mm, "end": v(-5161.97, 3691.23) * mm});
            skLineSegment(sketch, "E1238", {"start": v(-5161.97, 3691.23) * mm, "end": v(-5149.43, 3728.3) * mm});
            skLineSegment(sketch, "E1239", {"start": v(-5149.43, 3728.3) * mm, "end": v(-5129.03, 3763.38) * mm});
            skLineSegment(sketch, "E1240", {"start": v(-3714.25, 5162.9) * mm, "end": v(-3679.54, 5183.75) * mm});
            skLineSegment(sketch, "E1241", {"start": v(-3679.54, 5183.75) * mm, "end": v(-3642.73, 5196.45) * mm});
            skLineSegment(sketch, "E1242", {"start": v(-3642.73, 5196.45) * mm, "end": v(-3604.98, 5201.3) * mm});
            skLineSegment(sketch, "E1243", {"start": v(-3604.98, 5201.3) * mm, "end": v(-3567.47, 5198.6) * mm});
            skLineSegment(sketch, "E1244", {"start": v(-3567.47, 5198.6) * mm, "end": v(-3531.36, 5188.63) * mm});
            skLineSegment(sketch, "E1245", {"start": v(-3531.36, 5188.63) * mm, "end": v(-3497.82, 5171.68) * mm});
            skLineSegment(sketch, "E1246", {"start": v(-3497.82, 5171.68) * mm, "end": v(-3468.01, 5148.04) * mm});
            skLineSegment(sketch, "E1247", {"start": v(-3468.01, 5148.04) * mm, "end": v(-3443.1, 5118.01) * mm});
            skLineSegment(sketch, "E1248", {"start": v(-3443.1, 5118.01) * mm, "end": v(-3424.85, 5083.73) * mm});
            skLineSegment(sketch, "E1249", {"start": v(-3424.85, 5083.73) * mm, "end": v(-3413.99, 5047.78) * mm});
            skLineSegment(sketch, "E1250", {"start": v(-3413.99, 5047.78) * mm, "end": v(-3410.27, 5011.13) * mm});
            skLineSegment(sketch, "E1251", {"start": v(-3410.27, 5011.13) * mm, "end": v(-3413.43, 4974.74) * mm});
            skLineSegment(sketch, "E1252", {"start": v(-3413.43, 4974.74) * mm, "end": v(-3423.21, 4939.58) * mm});
            skLineSegment(sketch, "E1253", {"start": v(-3423.21, 4939.58) * mm, "end": v(-3439.34, 4906.6) * mm});
            skLineSegment(sketch, "E1254", {"start": v(-3439.34, 4906.6) * mm, "end": v(-3461.56, 4876.8) * mm});
            skLineSegment(sketch, "E1255", {"start": v(-3461.56, 4876.8) * mm, "end": v(-3489.62, 4851.1) * mm});
            skLineSegment(sketch, "E1256", {"start": v(-3489.62, 4851.1) * mm, "end": v(-3522.4, 4831.98) * mm});
            skLineSegment(sketch, "E1257", {"start": v(-3522.4, 4831.98) * mm, "end": v(-3557.6, 4820.18) * mm});
            skLineSegment(sketch, "E1258", {"start": v(-3557.6, 4820.18) * mm, "end": v(-3594.15, 4815.52) * mm});
            skLineSegment(sketch, "E1259", {"start": v(-3594.15, 4815.52) * mm, "end": v(-3630.92, 4817.8) * mm});
            skLineSegment(sketch, "E1260", {"start": v(-3630.92, 4817.8) * mm, "end": v(-3666.82, 4826.82) * mm});
            skLineSegment(sketch, "E1261", {"start": v(-3666.82, 4826.82) * mm, "end": v(-3700.74, 4842.4) * mm});
            skLineSegment(sketch, "E1262", {"start": v(-3700.74, 4842.4) * mm, "end": v(-3731.59, 4864.32) * mm});
            skLineSegment(sketch, "E1263", {"start": v(-3731.59, 4864.32) * mm, "end": v(-3758.25, 4892.4) * mm});
            skLineSegment(sketch, "E1264", {"start": v(-3758.25, 4892.4) * mm, "end": v(-3778.92, 4925.62) * mm});
            skLineSegment(sketch, "E1265", {"start": v(-3778.92, 4925.62) * mm, "end": v(-3791.72, 4961.12) * mm});
            skLineSegment(sketch, "E1266", {"start": v(-3791.72, 4961.12) * mm, "end": v(-3796.85, 4997.86) * mm});
            skLineSegment(sketch, "E1267", {"start": v(-3796.85, 4997.86) * mm, "end": v(-3794.5, 5034.78) * mm});
            skLineSegment(sketch, "E1268", {"start": v(-3794.5, 5034.78) * mm, "end": v(-3784.87, 5070.8) * mm});
            skLineSegment(sketch, "E1269", {"start": v(-3784.87, 5070.8) * mm, "end": v(-3768.15, 5104.86) * mm});
            skLineSegment(sketch, "E1270", {"start": v(-3768.15, 5104.86) * mm, "end": v(-3744.55, 5135.92) * mm});
            skLineSegment(sketch, "E1271", {"start": v(-3744.55, 5135.92) * mm, "end": v(-3714.25, 5162.9) * mm});
            skLineSegment(sketch, "E1272", {"start": v(-1937.73, 6060.2) * mm, "end": v(-1897.87, 6068.05) * mm});
            skLineSegment(sketch, "E1273", {"start": v(-1897.87, 6068.05) * mm, "end": v(-1858.7, 6068.07) * mm});
            skLineSegment(sketch, "E1274", {"start": v(-1858.7, 6068.07) * mm, "end": v(-1821.23, 6060.77) * mm});
            skLineSegment(sketch, "E1275", {"start": v(-1821.23, 6060.77) * mm, "end": v(-1786.42, 6046.68) * mm});
            skLineSegment(sketch, "E1276", {"start": v(-1786.42, 6046.68) * mm, "end": v(-1755.26, 6026.3) * mm});
            skLineSegment(sketch, "E1277", {"start": v(-1755.26, 6026.3) * mm, "end": v(-1728.72, 6000.17) * mm});
            skLineSegment(sketch, "E1278", {"start": v(-1728.72, 6000.17) * mm, "end": v(-1707.8, 5968.77) * mm});
            skLineSegment(sketch, "E1279", {"start": v(-1707.8, 5968.77) * mm, "end": v(-1693.48, 5932.64) * mm});
            skLineSegment(sketch, "E1280", {"start": v(-1693.48, 5932.64) * mm, "end": v(-1686.7, 5894.26) * mm});
            skLineSegment(sketch, "E1281", {"start": v(-1686.7, 5894.26) * mm, "end": v(-1687.43, 5856.4) * mm});
            skLineSegment(sketch, "E1282", {"start": v(-1687.43, 5856.4) * mm, "end": v(-1695.14, 5820.04) * mm});
            skLineSegment(sketch, "E1283", {"start": v(-1695.14, 5820.04) * mm, "end": v(-1709.33, 5786.12) * mm});
            skLineSegment(sketch, "E1284", {"start": v(-1709.33, 5786.12) * mm, "end": v(-1729.5, 5755.62) * mm});
            skLineSegment(sketch, "E1285", {"start": v(-1729.5, 5755.62) * mm, "end": v(-1755.11, 5729.49) * mm});
            skLineSegment(sketch, "E1286", {"start": v(-1755.11, 5729.49) * mm, "end": v(-1785.68, 5708.7) * mm});
            skLineSegment(sketch, "E1287", {"start": v(-1785.68, 5708.7) * mm, "end": v(-1820.68, 5694.18) * mm});
            skLineSegment(sketch, "E1288", {"start": v(-1820.68, 5694.18) * mm, "end": v(-1857.77, 5686.22) * mm});
            skLineSegment(sketch, "E1289", {"start": v(-1857.77, 5686.22) * mm, "end": v(-1894.77, 5685.58) * mm});
            skLineSegment(sketch, "E1290", {"start": v(-1894.77, 5685.58) * mm, "end": v(-1930.76, 5691.89) * mm});
            skLineSegment(sketch, "E1291", {"start": v(-1930.76, 5691.89) * mm, "end": v(-1964.78, 5704.76) * mm});
            skLineSegment(sketch, "E1292", {"start": v(-1964.78, 5704.76) * mm, "end": v(-1995.9, 5723.8) * mm});
            skLineSegment(sketch, "E1293", {"start": v(-1995.9, 5723.8) * mm, "end": v(-2023.18, 5748.65) * mm});
            skLineSegment(sketch, "E1294", {"start": v(-2023.18, 5748.65) * mm, "end": v(-2045.68, 5778.9) * mm});
            skLineSegment(sketch, "E1295", {"start": v(-2045.68, 5778.9) * mm, "end": v(-2062.47, 5814.2) * mm});
            skLineSegment(sketch, "E1296", {"start": v(-2062.47, 5814.2) * mm, "end": v(-2071.74, 5851.84) * mm});
            skLineSegment(sketch, "E1297", {"start": v(-2071.74, 5851.84) * mm, "end": v(-2072.97, 5889.7) * mm});
            skLineSegment(sketch, "E1298", {"start": v(-2072.97, 5889.7) * mm, "end": v(-2066.63, 5926.68) * mm});
            skLineSegment(sketch, "E1299", {"start": v(-2066.63, 5926.68) * mm, "end": v(-2053.19, 5961.7) * mm});
            skLineSegment(sketch, "E1300", {"start": v(-2053.19, 5961.7) * mm, "end": v(-2033.1, 5993.65) * mm});
            skLineSegment(sketch, "E1301", {"start": v(-2033.1, 5993.65) * mm, "end": v(-2006.86, 6021.45) * mm});
            skLineSegment(sketch, "E1302", {"start": v(-2006.86, 6021.45) * mm, "end": v(-1974.91, 6044) * mm});
            skLineSegment(sketch, "E1303", {"start": v(-1974.91, 6044) * mm, "end": v(-1937.73, 6060.2) * mm});
            skLineSegment(sketch, "E1304", {"start": v(-403.14, 5465.64) * mm, "end": v(-396.46, 5454.8) * mm});
            skLineSegment(sketch, "E1305", {"start": v(-396.46, 5454.8) * mm, "end": v(-389.06, 5444.52) * mm});
            skLineSegment(sketch, "E1306", {"start": v(-389.06, 5444.52) * mm, "end": v(-380.96, 5434.83) * mm});
            skLineSegment(sketch, "E1307", {"start": v(-380.96, 5434.83) * mm, "end": v(-372.17, 5425.78) * mm});
            skLineSegment(sketch, "E1308", {"start": v(-372.17, 5425.78) * mm, "end": v(-362.71, 5417.44) * mm});
            skLineSegment(sketch, "E1309", {"start": v(-362.71, 5417.44) * mm, "end": v(-352.62, 5409.85) * mm});
            skLineSegment(sketch, "E1310", {"start": v(-352.62, 5409.85) * mm, "end": v(-341.9, 5403.08) * mm});
            skLineSegment(sketch, "E1311", {"start": v(-341.9, 5403.08) * mm, "end": v(-330.57, 5397.18) * mm});
            skLineSegment(sketch, "E1312", {"start": v(-330.57, 5397.18) * mm, "end": v(-344, 5367.67) * mm});
            skLineSegment(sketch, "E1313", {"start": v(-344, 5367.67) * mm, "end": v(-351.84, 5335.19) * mm});
            skLineSegment(sketch, "E1314", {"start": v(-351.84, 5335.19) * mm, "end": v(-353.77, 5301.14) * mm});
            skLineSegment(sketch, "E1315", {"start": v(-353.77, 5301.14) * mm, "end": v(-349.46, 5266.96) * mm});
            skLineSegment(sketch, "E1316", {"start": v(-349.46, 5266.96) * mm, "end": v(-338.56, 5234.05) * mm});
            skLineSegment(sketch, "E1317", {"start": v(-338.56, 5234.05) * mm, "end": v(-320.72, 5203.85) * mm});
            skLineSegment(sketch, "E1318", {"start": v(-320.72, 5203.85) * mm, "end": v(-295.63, 5177.77) * mm});
            skLineSegment(sketch, "E1319", {"start": v(-295.63, 5177.77) * mm, "end": v(-262.93, 5157.23) * mm});
            skLineSegment(sketch, "E1320", {"start": v(-262.93, 5157.23) * mm, "end": v(-273.12, 5077.24) * mm});
            skLineSegment(sketch, "E1321", {"start": v(-273.12, 5077.24) * mm, "end": v(-288, 4981.6) * mm});
            skLineSegment(sketch, "E1322", {"start": v(-288, 4981.6) * mm, "end": v(-306.01, 4872.8) * mm});
            skLineSegment(sketch, "E1323", {"start": v(-306.01, 4872.8) * mm, "end": v(-325.62, 4753.27) * mm});
            skLineSegment(sketch, "E1324", {"start": v(-325.62, 4753.27) * mm, "end": v(-345.3, 4625.52) * mm});
            skLineSegment(sketch, "E1325", {"start": v(-345.3, 4625.52) * mm, "end": v(-363.47, 4492) * mm});
            skLineSegment(sketch, "E1326", {"start": v(-363.47, 4492) * mm, "end": v(-378.63, 4355.18) * mm});
            skLineSegment(sketch, "E1327", {"start": v(-378.63, 4355.18) * mm, "end": v(-389.22, 4217.53) * mm});
            skLineSegment(sketch, "E1328", {"start": v(-389.22, 4217.53) * mm, "end": v(-393.71, 4132.41) * mm});
            skLineSegment(sketch, "E1329", {"start": v(-393.71, 4132.41) * mm, "end": v(-396.17, 4054.2) * mm});
            skLineSegment(sketch, "E1330", {"start": v(-396.17, 4054.2) * mm, "end": v(-395.69, 3982.82) * mm});
            skLineSegment(sketch, "E1331", {"start": v(-395.69, 3982.82) * mm, "end": v(-391.33, 3918.18) * mm});
            skLineSegment(sketch, "E1332", {"start": v(-391.33, 3918.18) * mm, "end": v(-382.17, 3860.2) * mm});
            skLineSegment(sketch, "E1333", {"start": v(-382.17, 3860.2) * mm, "end": v(-367.3, 3808.8) * mm});
            skLineSegment(sketch, "E1334", {"start": v(-367.3, 3808.8) * mm, "end": v(-345.78, 3763.9) * mm});
            skLineSegment(sketch, "E1335", {"start": v(-345.78, 3763.9) * mm, "end": v(-316.7, 3725.4) * mm});
            skLineSegment(sketch, "E1336", {"start": v(-316.7, 3725.4) * mm, "end": v(-284.72, 3697.85) * mm});
            skLineSegment(sketch, "E1337", {"start": v(-284.72, 3697.85) * mm, "end": v(-314.52, 3671.26) * mm});
            skLineSegment(sketch, "E1338", {"start": v(-314.52, 3671.26) * mm, "end": v(-335.7, 3639.37) * mm});
            skLineSegment(sketch, "E1339", {"start": v(-335.7, 3639.37) * mm, "end": v(-348.64, 3603.92) * mm});
            skLineSegment(sketch, "E1340", {"start": v(-348.64, 3603.92) * mm, "end": v(-353.65, 3566.66) * mm});
            skLineSegment(sketch, "E1341", {"start": v(-353.65, 3566.66) * mm, "end": v(-351.09, 3529.36) * mm});
            skLineSegment(sketch, "E1342", {"start": v(-351.09, 3529.36) * mm, "end": v(-341.3, 3493.75) * mm});
            skLineSegment(sketch, "E1343", {"start": v(-341.3, 3493.75) * mm, "end": v(-324.61, 3461.59) * mm});
            skLineSegment(sketch, "E1344", {"start": v(-324.61, 3461.59) * mm, "end": v(-301.38, 3434.63) * mm});
            skLineSegment(sketch, "E1345", {"start": v(-301.38, 3434.63) * mm, "end": v(-355.66, 3386.15) * mm});
            skLineSegment(sketch, "E1346", {"start": v(-355.66, 3386.15) * mm, "end": v(-394.55, 3327.84) * mm});
            skLineSegment(sketch, "E1347", {"start": v(-394.55, 3327.84) * mm, "end": v(-418.1, 3262.95) * mm});
            skLineSegment(sketch, "E1348", {"start": v(-418.1, 3262.95) * mm, "end": v(-426.34, 3194.73) * mm});
            skLineSegment(sketch, "E1349", {"start": v(-426.34, 3194.73) * mm, "end": v(-419.32, 3126.43) * mm});
            skLineSegment(sketch, "E1350", {"start": v(-419.32, 3126.43) * mm, "end": v(-397.08, 3061.3) * mm});
            skLineSegment(sketch, "E1351", {"start": v(-397.08, 3061.3) * mm, "end": v(-359.67, 3002.6) * mm});
            skLineSegment(sketch, "E1352", {"start": v(-359.67, 3002.6) * mm, "end": v(-307.12, 2953.58) * mm});
            skLineSegment(sketch, "E1353", {"start": v(-307.12, 2953.58) * mm, "end": v(-316.6, 2912.74) * mm});
            skLineSegment(sketch, "E1354", {"start": v(-316.6, 2912.74) * mm, "end": v(-330.94, 2815.68) * mm});
            skLineSegment(sketch, "E1355", {"start": v(-330.94, 2815.68) * mm, "end": v(-348.25, 2681.25) * mm});
            skLineSegment(sketch, "E1356", {"start": v(-348.25, 2681.25) * mm, "end": v(-366.66, 2528.3) * mm});
            skLineSegment(sketch, "E1357", {"start": v(-366.66, 2528.3) * mm, "end": v(-384.26, 2375.7) * mm});
            skLineSegment(sketch, "E1358", {"start": v(-384.26, 2375.7) * mm, "end": v(-399.17, 2242.27) * mm});
            skLineSegment(sketch, "E1359", {"start": v(-399.17, 2242.27) * mm, "end": v(-409.5, 2146.86) * mm});
            skLineSegment(sketch, "E1360", {"start": v(-409.5, 2146.86) * mm, "end": v(-413.37, 2108.34) * mm});
            skLineSegment(sketch, "E1361", {"start": v(-413.37, 2108.34) * mm, "end": v(-413.37, 1633) * mm});
            skLineSegment(sketch, "E1362", {"start": v(-413.37, 1633) * mm, "end": v(-472.92, 1616.8) * mm});
            skLineSegment(sketch, "E1363", {"start": v(-472.92, 1616.8) * mm, "end": v(-531.56, 1598.52) * mm});
            skLineSegment(sketch, "E1364", {"start": v(-531.56, 1598.52) * mm, "end": v(-589.25, 1578.2) * mm});
            skLineSegment(sketch, "E1365", {"start": v(-589.25, 1578.2) * mm, "end": v(-645.94, 1555.87) * mm});
            skLineSegment(sketch, "E1366", {"start": v(-645.94, 1555.87) * mm, "end": v(-701.6, 1531.57) * mm});
            skLineSegment(sketch, "E1367", {"start": v(-701.6, 1531.57) * mm, "end": v(-756.22, 1505.33) * mm});
            skLineSegment(sketch, "E1368", {"start": v(-756.22, 1505.33) * mm, "end": v(-809.72, 1477.2) * mm});
            skLineSegment(sketch, "E1369", {"start": v(-809.72, 1477.2) * mm, "end": v(-862.09, 1447.2) * mm});
            skLineSegment(sketch, "E1370", {"start": v(-862.09, 1447.2) * mm, "end": v(-1198.26, 1783.37) * mm});
            skLineSegment(sketch, "E1371", {"start": v(-1198.26, 1783.37) * mm, "end": v(-1228.36, 1807.96) * mm});
            skLineSegment(sketch, "E1372", {"start": v(-1228.36, 1807.96) * mm, "end": v(-1303.26, 1868.13) * mm});
            skLineSegment(sketch, "E1373", {"start": v(-1303.26, 1868.13) * mm, "end": v(-1408.28, 1951.9) * mm});
            skLineSegment(sketch, "E1374", {"start": v(-1408.28, 1951.9) * mm, "end": v(-1528.73, 2047.3) * mm});
            skLineSegment(sketch, "E1375", {"start": v(-1528.73, 2047.3) * mm, "end": v(-1649.94, 2142.37) * mm});
            skLineSegment(sketch, "E1376", {"start": v(-1649.94, 2142.37) * mm, "end": v(-1757.22, 2225.1) * mm});
            skLineSegment(sketch, "E1377", {"start": v(-1757.22, 2225.1) * mm, "end": v(-1835.9, 2283.54) * mm});
            skLineSegment(sketch, "E1378", {"start": v(-1835.9, 2283.54) * mm, "end": v(-1871.28, 2305.7) * mm});
            skLineSegment(sketch, "E1379", {"start": v(-1871.28, 2305.7) * mm, "end": v(-1868.86, 2377.28) * mm});
            skLineSegment(sketch, "E1380", {"start": v(-1868.86, 2377.28) * mm, "end": v(-1883.88, 2445.15) * mm});
            skLineSegment(sketch, "E1381", {"start": v(-1883.88, 2445.15) * mm, "end": v(-1914.12, 2506.95) * mm});
            skLineSegment(sketch, "E1382", {"start": v(-1914.12, 2506.95) * mm, "end": v(-1957.35, 2560.29) * mm});
            skLineSegment(sketch, "E1383", {"start": v(-1957.35, 2560.29) * mm, "end": v(-2011.34, 2602.8) * mm});
            skLineSegment(sketch, "E1384", {"start": v(-2011.34, 2602.8) * mm, "end": v(-2073.87, 2632.12) * mm});
            skLineSegment(sketch, "E1385", {"start": v(-2073.87, 2632.12) * mm, "end": v(-2142.7, 2645.87) * mm});
            skLineSegment(sketch, "E1386", {"start": v(-2142.7, 2645.87) * mm, "end": v(-2215.63, 2641.69) * mm});
            skLineSegment(sketch, "E1387", {"start": v(-2215.63, 2641.69) * mm, "end": v(-2218.4, 2677.58) * mm});
            skLineSegment(sketch, "E1388", {"start": v(-2218.4, 2677.58) * mm, "end": v(-2229.58, 2712.3) * mm});
            skLineSegment(sketch, "E1389", {"start": v(-2229.58, 2712.3) * mm, "end": v(-2248.12, 2744.4) * mm});
            skLineSegment(sketch, "E1390", {"start": v(-2248.12, 2744.4) * mm, "end": v(-2272.94, 2772.45) * mm});
            skLineSegment(sketch, "E1391", {"start": v(-2272.94, 2772.45) * mm, "end": v(-2302.98, 2795.05) * mm});
            skLineSegment(sketch, "E1392", {"start": v(-2302.98, 2795.05) * mm, "end": v(-2337.17, 2810.76) * mm});
            skLineSegment(sketch, "E1393", {"start": v(-2337.17, 2810.76) * mm, "end": v(-2374.44, 2818.17) * mm});
            skLineSegment(sketch, "E1394", {"start": v(-2374.44, 2818.17) * mm, "end": v(-2413.72, 2815.83) * mm});
            skLineSegment(sketch, "E1395", {"start": v(-2413.72, 2815.83) * mm, "end": v(-2410.4, 2858.15) * mm});
            skLineSegment(sketch, "E1396", {"start": v(-2410.4, 2858.15) * mm, "end": v(-2417.03, 2905.95) * mm});
            skLineSegment(sketch, "E1397", {"start": v(-2417.03, 2905.95) * mm, "end": v(-2433.57, 2952.91) * mm});
            skLineSegment(sketch, "E1398", {"start": v(-2433.57, 2952.91) * mm, "end": v(-2459.4, 2999.77) * mm});
            skLineSegment(sketch, "E1399", {"start": v(-2459.4, 2999.77) * mm, "end": v(-2493.93, 3047.23) * mm});
            skLineSegment(sketch, "E1400", {"start": v(-2493.93, 3047.23) * mm, "end": v(-2536.56, 3096) * mm});
            skLineSegment(sketch, "E1401", {"start": v(-2536.56, 3096) * mm, "end": v(-2586.68, 3146.83) * mm});
            skLineSegment(sketch, "E1402", {"start": v(-2586.68, 3146.83) * mm, "end": v(-2643.7, 3200.42) * mm});
            skLineSegment(sketch, "E1403", {"start": v(-2643.7, 3200.42) * mm, "end": v(-2707, 3257.49) * mm});
            skLineSegment(sketch, "E1404", {"start": v(-2707, 3257.49) * mm, "end": v(-2811.91, 3347.23) * mm});
            skLineSegment(sketch, "E1405", {"start": v(-2811.91, 3347.23) * mm, "end": v(-2919.44, 3433.2) * mm});
            skLineSegment(sketch, "E1406", {"start": v(-2919.44, 3433.2) * mm, "end": v(-3026.74, 3514.72) * mm});
            skLineSegment(sketch, "E1407", {"start": v(-3026.74, 3514.72) * mm, "end": v(-3131, 3591.15) * mm});
            skLineSegment(sketch, "E1408", {"start": v(-3131, 3591.15) * mm, "end": v(-3229.35, 3661.82) * mm});
            skLineSegment(sketch, "E1409", {"start": v(-3229.35, 3661.82) * mm, "end": v(-3319, 3726.07) * mm});
            skLineSegment(sketch, "E1410", {"start": v(-3319, 3726.07) * mm, "end": v(-3397.08, 3783.24) * mm});
            skLineSegment(sketch, "E1411", {"start": v(-3397.08, 3783.24) * mm, "end": v(-3460.79, 3832.67) * mm});
            skLineSegment(sketch, "E1412", {"start": v(-3460.79, 3832.67) * mm, "end": v(-3452.18, 3870.53) * mm});
            skLineSegment(sketch, "E1413", {"start": v(-3452.18, 3870.53) * mm, "end": v(-3453, 3906.86) * mm});
            skLineSegment(sketch, "E1414", {"start": v(-3453, 3906.86) * mm, "end": v(-3461.93, 3940.89) * mm});
            skLineSegment(sketch, "E1415", {"start": v(-3461.93, 3940.89) * mm, "end": v(-3477.68, 3971.87) * mm});
            skLineSegment(sketch, "E1416", {"start": v(-3477.68, 3971.87) * mm, "end": v(-3498.93, 3999.05) * mm});
            skLineSegment(sketch, "E1417", {"start": v(-3498.93, 3999.05) * mm, "end": v(-3524.38, 4021.66) * mm});
            skLineSegment(sketch, "E1418", {"start": v(-3524.38, 4021.66) * mm, "end": v(-3552.7, 4038.95) * mm});
            skLineSegment(sketch, "E1419", {"start": v(-3552.7, 4038.95) * mm, "end": v(-3582.6, 4050.17) * mm});
            skLineSegment(sketch, "E1420", {"start": v(-3582.6, 4050.17) * mm, "end": v(-3578.82, 4062.3) * mm});
            skLineSegment(sketch, "E1421", {"start": v(-3578.82, 4062.3) * mm, "end": v(-3576.07, 4074.64) * mm});
            skLineSegment(sketch, "E1422", {"start": v(-3576.07, 4074.64) * mm, "end": v(-3574.32, 4087.13) * mm});
            skLineSegment(sketch, "E1423", {"start": v(-3574.32, 4087.13) * mm, "end": v(-3573.55, 4099.71) * mm});
            skLineSegment(sketch, "E1424", {"start": v(-3573.55, 4099.71) * mm, "end": v(-3573.74, 4112.33) * mm});
            skLineSegment(sketch, "E1425", {"start": v(-3573.74, 4112.33) * mm, "end": v(-3574.86, 4124.94) * mm});
            skLineSegment(sketch, "E1426", {"start": v(-3574.86, 4124.94) * mm, "end": v(-3576.9, 4137.47) * mm});
            skLineSegment(sketch, "E1427", {"start": v(-3576.9, 4137.47) * mm, "end": v(-3579.81, 4149.86) * mm});
            skLineSegment(sketch, "E1428", {"start": v(-3579.81, 4149.86) * mm, "end": v(-3244.52, 4417.3) * mm});
            skLineSegment(sketch, "E1429", {"start": v(-3244.52, 4417.3) * mm, "end": v(-2888.62, 4658.26) * mm});
            skLineSegment(sketch, "E1430", {"start": v(-2888.62, 4658.26) * mm, "end": v(-2513.6, 4871.28) * mm});
            skLineSegment(sketch, "E1431", {"start": v(-2513.6, 4871.28) * mm, "end": v(-2120.9, 5054.89) * mm});
            skLineSegment(sketch, "E1432", {"start": v(-2120.9, 5054.89) * mm, "end": v(-1712.05, 5207.6) * mm});
            skLineSegment(sketch, "E1433", {"start": v(-1712.05, 5207.6) * mm, "end": v(-1288.48, 5327.95) * mm});
            skLineSegment(sketch, "E1434", {"start": v(-1288.48, 5327.95) * mm, "end": v(-851.68, 5414.45) * mm});
            skLineSegment(sketch, "E1435", {"start": v(-851.68, 5414.45) * mm, "end": v(-403.14, 5465.64) * mm});
            skLineSegment(sketch, "E1436", {"start": v(29.86, 6359.56) * mm, "end": v(70.17, 6355.23) * mm});
            skLineSegment(sketch, "E1437", {"start": v(70.17, 6355.23) * mm, "end": v(107.4, 6343.63) * mm});
            skLineSegment(sketch, "E1438", {"start": v(107.4, 6343.63) * mm, "end": v(140.78, 6325.55) * mm});
            skLineSegment(sketch, "E1439", {"start": v(140.78, 6325.55) * mm, "end": v(169.53, 6301.77) * mm});
            skLineSegment(sketch, "E1440", {"start": v(169.53, 6301.77) * mm, "end": v(192.86, 6273.08) * mm});
            skLineSegment(sketch, "E1441", {"start": v(192.86, 6273.08) * mm, "end": v(210.02, 6240.25) * mm});
            skLineSegment(sketch, "E1442", {"start": v(210.02, 6240.25) * mm, "end": v(220.2, 6204.07) * mm});
            skLineSegment(sketch, "E1443", {"start": v(220.2, 6204.07) * mm, "end": v(222.67, 6165.33) * mm});
            skLineSegment(sketch, "E1444", {"start": v(222.67, 6165.33) * mm, "end": v(217.26, 6126.68) * mm});
            skLineSegment(sketch, "E1445", {"start": v(217.26, 6126.68) * mm, "end": v(204.88, 6090.75) * mm});
            skLineSegment(sketch, "E1446", {"start": v(204.88, 6090.75) * mm, "end": v(186.3, 6058.31) * mm});
            skLineSegment(sketch, "E1447", {"start": v(186.3, 6058.31) * mm, "end": v(162.3, 6030.13) * mm});
            skLineSegment(sketch, "E1448", {"start": v(162.3, 6030.13) * mm, "end": v(133.69, 6006.98) * mm});
            skLineSegment(sketch, "E1449", {"start": v(133.69, 6006.98) * mm, "end": v(101.22, 5989.61) * mm});
            skLineSegment(sketch, "E1450", {"start": v(101.22, 5989.61) * mm, "end": v(65.69, 5978.8) * mm});
            skLineSegment(sketch, "E1451", {"start": v(65.69, 5978.8) * mm, "end": v(27.88, 5975.31) * mm});
            skLineSegment(sketch, "E1452", {"start": v(27.88, 5975.31) * mm, "end": v(-9.9, 5979.98) * mm});
            skLineSegment(sketch, "E1453", {"start": v(-9.9, 5979.98) * mm, "end": v(-45.31, 5991.45) * mm});
            skLineSegment(sketch, "E1454", {"start": v(-45.31, 5991.45) * mm, "end": v(-77.59, 6009.04) * mm});
            skLineSegment(sketch, "E1455", {"start": v(-77.59, 6009.04) * mm, "end": v(-105.96, 6032.11) * mm});
            skLineSegment(sketch, "E1456", {"start": v(-105.96, 6032.11) * mm, "end": v(-129.64, 6060) * mm});
            skLineSegment(sketch, "E1457", {"start": v(-129.64, 6060) * mm, "end": v(-147.87, 6092.05) * mm});
            skLineSegment(sketch, "E1458", {"start": v(-147.87, 6092.05) * mm, "end": v(-159.88, 6127.6) * mm});
            skLineSegment(sketch, "E1459", {"start": v(-159.88, 6127.6) * mm, "end": v(-164.88, 6165.99) * mm});
            skLineSegment(sketch, "E1460", {"start": v(-164.88, 6165.99) * mm, "end": v(-162.03, 6205.02) * mm});
            skLineSegment(sketch, "E1461", {"start": v(-162.03, 6205.02) * mm, "end": v(-151.47, 6241.6) * mm});
            skLineSegment(sketch, "E1462", {"start": v(-151.47, 6241.6) * mm, "end": v(-133.99, 6274.82) * mm});
            skLineSegment(sketch, "E1463", {"start": v(-133.99, 6274.82) * mm, "end": v(-110.37, 6303.81) * mm});
            skLineSegment(sketch, "E1464", {"start": v(-110.37, 6303.81) * mm, "end": v(-81.39, 6327.67) * mm});
            skLineSegment(sketch, "E1465", {"start": v(-81.39, 6327.67) * mm, "end": v(-47.84, 6345.51) * mm});
            skLineSegment(sketch, "E1466", {"start": v(-47.84, 6345.51) * mm, "end": v(-10.5, 6356.44) * mm});
            skLineSegment(sketch, "E1467", {"start": v(-10.5, 6356.44) * mm, "end": v(29.86, 6359.56) * mm});
            skLineSegment(sketch, "E1468", {"start": v(330.6, 5397.18) * mm, "end": v(341.84, 5403.08) * mm});
            skLineSegment(sketch, "E1469", {"start": v(341.84, 5403.08) * mm, "end": v(352.51, 5409.86) * mm});
            skLineSegment(sketch, "E1470", {"start": v(352.51, 5409.86) * mm, "end": v(362.58, 5417.44) * mm});
            skLineSegment(sketch, "E1471", {"start": v(362.58, 5417.44) * mm, "end": v(372.01, 5425.79) * mm});
            skLineSegment(sketch, "E1472", {"start": v(372.01, 5425.79) * mm, "end": v(380.8, 5434.84) * mm});
            skLineSegment(sketch, "E1473", {"start": v(380.8, 5434.84) * mm, "end": v(388.92, 5444.53) * mm});
            skLineSegment(sketch, "E1474", {"start": v(388.92, 5444.53) * mm, "end": v(396.33, 5454.82) * mm});
            skLineSegment(sketch, "E1475", {"start": v(396.33, 5454.82) * mm, "end": v(403.03, 5465.64) * mm});
            skLineSegment(sketch, "E1476", {"start": v(403.03, 5465.64) * mm, "end": v(851.6, 5414.46) * mm});
            skLineSegment(sketch, "E1477", {"start": v(851.6, 5414.46) * mm, "end": v(1288.4, 5327.96) * mm});
            skLineSegment(sketch, "E1478", {"start": v(1288.4, 5327.96) * mm, "end": v(1711.97, 5207.61) * mm});
            skLineSegment(sketch, "E1479", {"start": v(1711.97, 5207.61) * mm, "end": v(2120.84, 5054.9) * mm});
            skLineSegment(sketch, "E1480", {"start": v(2120.84, 5054.9) * mm, "end": v(2513.52, 4871.28) * mm});
            skLineSegment(sketch, "E1481", {"start": v(2513.52, 4871.28) * mm, "end": v(2888.54, 4658.25) * mm});
            skLineSegment(sketch, "E1482", {"start": v(2888.54, 4658.25) * mm, "end": v(3244.43, 4417.28) * mm});
            skLineSegment(sketch, "E1483", {"start": v(3244.43, 4417.28) * mm, "end": v(3579.71, 4149.84) * mm});
            skLineSegment(sketch, "E1484", {"start": v(3579.71, 4149.84) * mm, "end": v(3576.78, 4137.47) * mm});
            skLineSegment(sketch, "E1485", {"start": v(3576.78, 4137.47) * mm, "end": v(3574.74, 4124.96) * mm});
            skLineSegment(sketch, "E1486", {"start": v(3574.74, 4124.96) * mm, "end": v(3573.62, 4112.37) * mm});
            skLineSegment(sketch, "E1487", {"start": v(3573.62, 4112.37) * mm, "end": v(3573.44, 4099.76) * mm});
            skLineSegment(sketch, "E1488", {"start": v(3573.44, 4099.76) * mm, "end": v(3574.22, 4087.17) * mm});
            skLineSegment(sketch, "E1489", {"start": v(3574.22, 4087.17) * mm, "end": v(3576, 4074.67) * mm});
            skLineSegment(sketch, "E1490", {"start": v(3576, 4074.67) * mm, "end": v(3578.8, 4062.3) * mm});
            skLineSegment(sketch, "E1491", {"start": v(3578.8, 4062.3) * mm, "end": v(3582.63, 4050.12) * mm});
            skLineSegment(sketch, "E1492", {"start": v(3582.63, 4050.12) * mm, "end": v(3552.27, 4038.75) * mm});
            skLineSegment(sketch, "E1493", {"start": v(3552.27, 4038.75) * mm, "end": v(3523.75, 4021.34) * mm});
            skLineSegment(sketch, "E1494", {"start": v(3523.75, 4021.34) * mm, "end": v(3498.31, 3998.63) * mm});
            skLineSegment(sketch, "E1495", {"start": v(3498.31, 3998.63) * mm, "end": v(3477.2, 3971.41) * mm});
            skLineSegment(sketch, "E1496", {"start": v(3477.2, 3971.41) * mm, "end": v(3461.64, 3940.44) * mm});
            skLineSegment(sketch, "E1497", {"start": v(3461.64, 3940.44) * mm, "end": v(3452.9, 3906.48) * mm});
            skLineSegment(sketch, "E1498", {"start": v(3452.9, 3906.48) * mm, "end": v(3452.2, 3870.29) * mm});
            skLineSegment(sketch, "E1499", {"start": v(3452.2, 3870.29) * mm, "end": v(3460.81, 3832.64) * mm});
            skLineSegment(sketch, "E1500", {"start": v(3460.81, 3832.64) * mm, "end": v(3397.03, 3783.29) * mm});
            skLineSegment(sketch, "E1501", {"start": v(3397.03, 3783.29) * mm, "end": v(3318.88, 3726.17) * mm});
            skLineSegment(sketch, "E1502", {"start": v(3318.88, 3726.17) * mm, "end": v(3229.2, 3661.96) * mm});
            skLineSegment(sketch, "E1503", {"start": v(3229.2, 3661.96) * mm, "end": v(3130.8, 3591.32) * mm});
            skLineSegment(sketch, "E1504", {"start": v(3130.8, 3591.32) * mm, "end": v(3026.56, 3514.88) * mm});
            skLineSegment(sketch, "E1505", {"start": v(3026.56, 3514.88) * mm, "end": v(2919.3, 3433.33) * mm});
            skLineSegment(sketch, "E1506", {"start": v(2919.3, 3433.33) * mm, "end": v(2811.83, 3347.3) * mm});
            skLineSegment(sketch, "E1507", {"start": v(2811.83, 3347.3) * mm, "end": v(2707.02, 3257.46) * mm});
            skLineSegment(sketch, "E1508", {"start": v(2707.02, 3257.46) * mm, "end": v(2643.66, 3200.45) * mm});
            skLineSegment(sketch, "E1509", {"start": v(2643.66, 3200.45) * mm, "end": v(2586.62, 3146.9) * mm});
            skLineSegment(sketch, "E1510", {"start": v(2586.62, 3146.9) * mm, "end": v(2536.5, 3096.08) * mm});
            skLineSegment(sketch, "E1511", {"start": v(2536.5, 3096.08) * mm, "end": v(2493.87, 3047.29) * mm});
            skLineSegment(sketch, "E1512", {"start": v(2493.87, 3047.29) * mm, "end": v(2459.35, 2999.81) * mm});
            skLineSegment(sketch, "E1513", {"start": v(2459.35, 2999.81) * mm, "end": v(2433.52, 2952.95) * mm});
            skLineSegment(sketch, "E1514", {"start": v(2433.52, 2952.95) * mm, "end": v(2416.98, 2905.98) * mm});
            skLineSegment(sketch, "E1515", {"start": v(2416.98, 2905.98) * mm, "end": v(2410.32, 2858.2) * mm});
            skLineSegment(sketch, "E1516", {"start": v(2410.32, 2858.2) * mm, "end": v(2413.44, 2816.11) * mm});
            skLineSegment(sketch, "E1517", {"start": v(2413.44, 2816.11) * mm, "end": v(2373.58, 2818.38) * mm});
            skLineSegment(sketch, "E1518", {"start": v(2373.58, 2818.38) * mm, "end": v(2336.04, 2810.81) * mm});
            skLineSegment(sketch, "E1519", {"start": v(2336.04, 2810.81) * mm, "end": v(2301.83, 2794.89) * mm});
            skLineSegment(sketch, "E1520", {"start": v(2301.83, 2794.89) * mm, "end": v(2271.94, 2772.09) * mm});
            skLineSegment(sketch, "E1521", {"start": v(2271.94, 2772.09) * mm, "end": v(2247.37, 2743.9) * mm});
            skLineSegment(sketch, "E1522", {"start": v(2247.37, 2743.9) * mm, "end": v(2229.11, 2711.78) * mm});
            skLineSegment(sketch, "E1523", {"start": v(2229.11, 2711.78) * mm, "end": v(2218.17, 2677.25) * mm});
            skLineSegment(sketch, "E1524", {"start": v(2218.17, 2677.25) * mm, "end": v(2215.53, 2641.77) * mm});
            skLineSegment(sketch, "E1525", {"start": v(2215.53, 2641.77) * mm, "end": v(2142.88, 2645.86) * mm});
            skLineSegment(sketch, "E1526", {"start": v(2142.88, 2645.86) * mm, "end": v(2074.15, 2632.13) * mm});
            skLineSegment(sketch, "E1527", {"start": v(2074.15, 2632.13) * mm, "end": v(2011.61, 2602.9) * mm});
            skLineSegment(sketch, "E1528", {"start": v(2011.61, 2602.9) * mm, "end": v(1957.54, 2560.48) * mm});
            skLineSegment(sketch, "E1529", {"start": v(1957.54, 2560.48) * mm, "end": v(1914.2, 2507.22) * mm});
            skLineSegment(sketch, "E1530", {"start": v(1914.2, 2507.22) * mm, "end": v(1883.88, 2445.45) * mm});
            skLineSegment(sketch, "E1531", {"start": v(1883.88, 2445.45) * mm, "end": v(1868.83, 2377.5) * mm});
            skLineSegment(sketch, "E1532", {"start": v(1868.83, 2377.5) * mm, "end": v(1871.33, 2305.67) * mm});
            skLineSegment(sketch, "E1533", {"start": v(1871.33, 2305.67) * mm, "end": v(1835.75, 2283.5) * mm});
            skLineSegment(sketch, "E1534", {"start": v(1835.75, 2283.5) * mm, "end": v(1756.98, 2225) * mm});
            skLineSegment(sketch, "E1535", {"start": v(1756.98, 2225) * mm, "end": v(1649.68, 2142.19) * mm});
            skLineSegment(sketch, "E1536", {"start": v(1649.68, 2142.19) * mm, "end": v(1528.51, 2047.05) * mm});
            skLineSegment(sketch, "E1537", {"start": v(1528.51, 2047.05) * mm, "end": v(1408.15, 1951.59) * mm});
            skLineSegment(sketch, "E1538", {"start": v(1408.15, 1951.59) * mm, "end": v(1303.25, 1867.78) * mm});
            skLineSegment(sketch, "E1539", {"start": v(1303.25, 1867.78) * mm, "end": v(1228.48, 1807.62) * mm});
            skLineSegment(sketch, "E1540", {"start": v(1228.48, 1807.62) * mm, "end": v(1198.51, 1783.12) * mm});
            skLineSegment(sketch, "E1541", {"start": v(1198.51, 1783.12) * mm, "end": v(862.4, 1447) * mm});
            skLineSegment(sketch, "E1542", {"start": v(862.4, 1447) * mm, "end": v(810.03, 1477.02) * mm});
            skLineSegment(sketch, "E1543", {"start": v(810.03, 1477.02) * mm, "end": v(756.52, 1505.17) * mm});
            skLineSegment(sketch, "E1544", {"start": v(756.52, 1505.17) * mm, "end": v(701.92, 1531.41) * mm});
            skLineSegment(sketch, "E1545", {"start": v(701.92, 1531.41) * mm, "end": v(646.26, 1555.73) * mm});
            skLineSegment(sketch, "E1546", {"start": v(646.26, 1555.73) * mm, "end": v(589.57, 1578.07) * mm});
            skLineSegment(sketch, "E1547", {"start": v(589.57, 1578.07) * mm, "end": v(531.9, 1598.4) * mm});
            skLineSegment(sketch, "E1548", {"start": v(531.9, 1598.4) * mm, "end": v(473.27, 1616.7) * mm});
            skLineSegment(sketch, "E1549", {"start": v(473.27, 1616.7) * mm, "end": v(413.73, 1632.93) * mm});
            skLineSegment(sketch, "E1550", {"start": v(413.73, 1632.93) * mm, "end": v(413.73, 2108.34) * mm});
            skLineSegment(sketch, "E1551", {"start": v(413.73, 2108.34) * mm, "end": v(409.83, 2147) * mm});
            skLineSegment(sketch, "E1552", {"start": v(409.83, 2147) * mm, "end": v(399.42, 2242.51) * mm});
            skLineSegment(sketch, "E1553", {"start": v(399.42, 2242.51) * mm, "end": v(384.4, 2376) * mm});
            skLineSegment(sketch, "E1554", {"start": v(384.4, 2376) * mm, "end": v(366.7, 2528.64) * mm});
            skLineSegment(sketch, "E1555", {"start": v(366.7, 2528.64) * mm, "end": v(348.2, 2681.57) * mm});
            skLineSegment(sketch, "E1556", {"start": v(348.2, 2681.57) * mm, "end": v(330.84, 2815.93) * mm});
            skLineSegment(sketch, "E1557", {"start": v(330.84, 2815.93) * mm, "end": v(316.53, 2912.88) * mm});
            skLineSegment(sketch, "E1558", {"start": v(316.53, 2912.88) * mm, "end": v(307.17, 2953.58) * mm});
            skLineSegment(sketch, "E1559", {"start": v(307.17, 2953.58) * mm, "end": v(359.5, 3002.47) * mm});
            skLineSegment(sketch, "E1560", {"start": v(359.5, 3002.47) * mm, "end": v(396.88, 3061.09) * mm});
            skLineSegment(sketch, "E1561", {"start": v(396.88, 3061.09) * mm, "end": v(419.2, 3126.16) * mm});
            skLineSegment(sketch, "E1562", {"start": v(419.2, 3126.16) * mm, "end": v(426.34, 3194.44) * mm});
            skLineSegment(sketch, "E1563", {"start": v(426.34, 3194.44) * mm, "end": v(418.22, 3262.68) * mm});
            skLineSegment(sketch, "E1564", {"start": v(418.22, 3262.68) * mm, "end": v(394.74, 3327.63) * mm});
            skLineSegment(sketch, "E1565", {"start": v(394.74, 3327.63) * mm, "end": v(355.8, 3386.03) * mm});
            skLineSegment(sketch, "E1566", {"start": v(355.8, 3386.03) * mm, "end": v(301.28, 3434.63) * mm});
            skLineSegment(sketch, "E1567", {"start": v(301.28, 3434.63) * mm, "end": v(324.7, 3461.97) * mm});
            skLineSegment(sketch, "E1568", {"start": v(324.7, 3461.97) * mm, "end": v(341.34, 3494.42) * mm});
            skLineSegment(sketch, "E1569", {"start": v(341.34, 3494.42) * mm, "end": v(350.92, 3530.23) * mm});
            skLineSegment(sketch, "E1570", {"start": v(350.92, 3530.23) * mm, "end": v(353.2, 3567.63) * mm});
            skLineSegment(sketch, "E1571", {"start": v(353.2, 3567.63) * mm, "end": v(347.94, 3604.85) * mm});
            skLineSegment(sketch, "E1572", {"start": v(347.94, 3604.85) * mm, "end": v(334.87, 3640.14) * mm});
            skLineSegment(sketch, "E1573", {"start": v(334.87, 3640.14) * mm, "end": v(313.75, 3671.72) * mm});
            skLineSegment(sketch, "E1574", {"start": v(313.75, 3671.72) * mm, "end": v(284.31, 3697.85) * mm});
            skLineSegment(sketch, "E1575", {"start": v(284.31, 3697.85) * mm, "end": v(316.6, 3725.4) * mm});
            skLineSegment(sketch, "E1576", {"start": v(316.6, 3725.4) * mm, "end": v(345.7, 3763.9) * mm});
            skLineSegment(sketch, "E1577", {"start": v(345.7, 3763.9) * mm, "end": v(367.23, 3808.8) * mm});
            skLineSegment(sketch, "E1578", {"start": v(367.23, 3808.8) * mm, "end": v(382.09, 3860.2) * mm});
            skLineSegment(sketch, "E1579", {"start": v(382.09, 3860.2) * mm, "end": v(391.23, 3918.18) * mm});
            skLineSegment(sketch, "E1580", {"start": v(391.23, 3918.18) * mm, "end": v(395.59, 3982.82) * mm});
            skLineSegment(sketch, "E1581", {"start": v(395.59, 3982.82) * mm, "end": v(396.1, 4054.2) * mm});
            skLineSegment(sketch, "E1582", {"start": v(396.1, 4054.2) * mm, "end": v(393.67, 4132.41) * mm});
            skLineSegment(sketch, "E1583", {"start": v(393.67, 4132.41) * mm, "end": v(389.27, 4217.53) * mm});
            skLineSegment(sketch, "E1584", {"start": v(389.27, 4217.53) * mm, "end": v(378.54, 4355.18) * mm});
            skLineSegment(sketch, "E1585", {"start": v(378.54, 4355.18) * mm, "end": v(363.29, 4492) * mm});
            skLineSegment(sketch, "E1586", {"start": v(363.29, 4492) * mm, "end": v(345.06, 4625.52) * mm});
            skLineSegment(sketch, "E1587", {"start": v(345.06, 4625.52) * mm, "end": v(325.39, 4753.27) * mm});
            skLineSegment(sketch, "E1588", {"start": v(325.39, 4753.27) * mm, "end": v(305.8, 4872.8) * mm});
            skLineSegment(sketch, "E1589", {"start": v(305.8, 4872.8) * mm, "end": v(287.85, 4981.6) * mm});
            skLineSegment(sketch, "E1590", {"start": v(287.85, 4981.6) * mm, "end": v(273.05, 5077.24) * mm});
            skLineSegment(sketch, "E1591", {"start": v(273.05, 5077.24) * mm, "end": v(262.95, 5157.23) * mm});
            skLineSegment(sketch, "E1592", {"start": v(262.95, 5157.23) * mm, "end": v(295.82, 5177.92) * mm});
            skLineSegment(sketch, "E1593", {"start": v(295.82, 5177.92) * mm, "end": v(320.93, 5204.2) * mm});
            skLineSegment(sketch, "E1594", {"start": v(320.93, 5204.2) * mm, "end": v(338.67, 5234.58) * mm});
            skLineSegment(sketch, "E1595", {"start": v(338.67, 5234.58) * mm, "end": v(349.45, 5267.63) * mm});
            skLineSegment(sketch, "E1596", {"start": v(349.45, 5267.63) * mm, "end": v(353.63, 5301.88) * mm});
            skLineSegment(sketch, "E1597", {"start": v(353.63, 5301.88) * mm, "end": v(351.63, 5335.86) * mm});
            skLineSegment(sketch, "E1598", {"start": v(351.63, 5335.86) * mm, "end": v(343.82, 5368.12) * mm});
            skLineSegment(sketch, "E1599", {"start": v(343.82, 5368.12) * mm, "end": v(330.6, 5397.18) * mm});
            skLineSegment(sketch, "E1600", {"start": v(1749.36, 5917.5) * mm, "end": v(1764.05, 5953.67) * mm});
            skLineSegment(sketch, "E1601", {"start": v(1764.05, 5953.67) * mm, "end": v(1785.24, 5984.85) * mm});
            skLineSegment(sketch, "E1602", {"start": v(1785.24, 5984.85) * mm, "end": v(1811.94, 6010.56) * mm});
            skLineSegment(sketch, "E1603", {"start": v(1811.94, 6010.56) * mm, "end": v(1843.18, 6030.35) * mm});
            skLineSegment(sketch, "E1604", {"start": v(1843.18, 6030.35) * mm, "end": v(1878, 6043.73) * mm});
            skLineSegment(sketch, "E1605", {"start": v(1878, 6043.73) * mm, "end": v(1915.39, 6050.23) * mm});
            skLineSegment(sketch, "E1606", {"start": v(1915.39, 6050.23) * mm, "end": v(1954.4, 6049.37) * mm});
            skLineSegment(sketch, "E1607", {"start": v(1954.4, 6049.37) * mm, "end": v(1994.04, 6040.7) * mm});
            skLineSegment(sketch, "E1608", {"start": v(1994.04, 6040.7) * mm, "end": v(2031.33, 6024.87) * mm});
            skLineSegment(sketch, "E1609", {"start": v(2031.33, 6024.87) * mm, "end": v(2063.26, 6002.57) * mm});
            skLineSegment(sketch, "E1610", {"start": v(2063.26, 6002.57) * mm, "end": v(2089.38, 5974.92) * mm});
            skLineSegment(sketch, "E1611", {"start": v(2089.38, 5974.92) * mm, "end": v(2109.25, 5943.01) * mm});
            skLineSegment(sketch, "E1612", {"start": v(2109.25, 5943.01) * mm, "end": v(2122.4, 5907.96) * mm});
            skLineSegment(sketch, "E1613", {"start": v(2122.4, 5907.96) * mm, "end": v(2128.39, 5870.87) * mm});
            skLineSegment(sketch, "E1614", {"start": v(2128.39, 5870.87) * mm, "end": v(2126.75, 5832.86) * mm});
            skLineSegment(sketch, "E1615", {"start": v(2126.75, 5832.86) * mm, "end": v(2117.05, 5795.02) * mm});
            skLineSegment(sketch, "E1616", {"start": v(2117.05, 5795.02) * mm, "end": v(2100.05, 5760.16) * mm});
            skLineSegment(sketch, "E1617", {"start": v(2100.05, 5760.16) * mm, "end": v(2077.35, 5730.27) * mm});
            skLineSegment(sketch, "E1618", {"start": v(2077.35, 5730.27) * mm, "end": v(2049.87, 5705.72) * mm});
            skLineSegment(sketch, "E1619", {"start": v(2049.87, 5705.72) * mm, "end": v(2018.56, 5686.87) * mm});
            skLineSegment(sketch, "E1620", {"start": v(2018.56, 5686.87) * mm, "end": v(1984.36, 5674.08) * mm});
            skLineSegment(sketch, "E1621", {"start": v(1984.36, 5674.08) * mm, "end": v(1948.2, 5667.72) * mm});
            skLineSegment(sketch, "E1622", {"start": v(1948.2, 5667.72) * mm, "end": v(1911.01, 5668.15) * mm});
            skLineSegment(sketch, "E1623", {"start": v(1911.01, 5668.15) * mm, "end": v(1873.75, 5675.72) * mm});
            skLineSegment(sketch, "E1624", {"start": v(1873.75, 5675.72) * mm, "end": v(1839.03, 5691.02) * mm});
            skLineSegment(sketch, "E1625", {"start": v(1839.03, 5691.02) * mm, "end": v(1808.8, 5712.58) * mm});
            skLineSegment(sketch, "E1626", {"start": v(1808.8, 5712.58) * mm, "end": v(1783.57, 5739.4) * mm});
            skLineSegment(sketch, "E1627", {"start": v(1783.57, 5739.4) * mm, "end": v(1763.8, 5770.48) * mm});
            skLineSegment(sketch, "E1628", {"start": v(1763.8, 5770.48) * mm, "end": v(1750, 5804.83) * mm});
            skLineSegment(sketch, "E1629", {"start": v(1750, 5804.83) * mm, "end": v(1742.68, 5841.45) * mm});
            skLineSegment(sketch, "E1630", {"start": v(1742.68, 5841.45) * mm, "end": v(1742.3, 5879.34) * mm});
            skLineSegment(sketch, "E1631", {"start": v(1742.3, 5879.34) * mm, "end": v(1749.36, 5917.5) * mm});
            skLineSegment(sketch, "E1632", {"start": v(3490.91, 5085.52) * mm, "end": v(3515.98, 5115.15) * mm});
            skLineSegment(sketch, "E1633", {"start": v(3515.98, 5115.15) * mm, "end": v(3545.89, 5138.33) * mm});
            skLineSegment(sketch, "E1634", {"start": v(3545.89, 5138.33) * mm, "end": v(3579.5, 5154.84) * mm});
            skLineSegment(sketch, "E1635", {"start": v(3579.5, 5154.84) * mm, "end": v(3615.7, 5164.44) * mm});
            skLineSegment(sketch, "E1636", {"start": v(3615.7, 5164.44) * mm, "end": v(3653.32, 5166.9) * mm});
            skLineSegment(sketch, "E1637", {"start": v(3653.32, 5166.9) * mm, "end": v(3691.23, 5161.97) * mm});
            skLineSegment(sketch, "E1638", {"start": v(3691.23, 5161.97) * mm, "end": v(3728.3, 5149.43) * mm});
            skLineSegment(sketch, "E1639", {"start": v(3728.3, 5149.43) * mm, "end": v(3763.38, 5129.03) * mm});
            skLineSegment(sketch, "E1640", {"start": v(3763.38, 5129.03) * mm, "end": v(3793.1, 5101.35) * mm});
            skLineSegment(sketch, "E1641", {"start": v(3793.1, 5101.35) * mm, "end": v(3816.07, 5069.63) * mm});
            skLineSegment(sketch, "E1642", {"start": v(3816.07, 5069.63) * mm, "end": v(3832.14, 5035) * mm});
            skLineSegment(sketch, "E1643", {"start": v(3832.14, 5035) * mm, "end": v(3841.15, 4998.52) * mm});
            skLineSegment(sketch, "E1644", {"start": v(3841.15, 4998.52) * mm, "end": v(3842.93, 4961.3) * mm});
            skLineSegment(sketch, "E1645", {"start": v(3842.93, 4961.3) * mm, "end": v(3837.34, 4924.47) * mm});
            skLineSegment(sketch, "E1646", {"start": v(3837.34, 4924.47) * mm, "end": v(3824.2, 4889.09) * mm});
            skLineSegment(sketch, "E1647", {"start": v(3824.2, 4889.09) * mm, "end": v(3803.36, 4856.26) * mm});
            skLineSegment(sketch, "E1648", {"start": v(3803.36, 4856.26) * mm, "end": v(3776.28, 4828.24) * mm});
            skLineSegment(sketch, "E1649", {"start": v(3776.28, 4828.24) * mm, "end": v(3745.22, 4806.61) * mm});
            skLineSegment(sketch, "E1650", {"start": v(3745.22, 4806.61) * mm, "end": v(3711.27, 4791.52) * mm});
            skLineSegment(sketch, "E1651", {"start": v(3711.27, 4791.52) * mm, "end": v(3675.5, 4783.12) * mm});
            skLineSegment(sketch, "E1652", {"start": v(3675.5, 4783.12) * mm, "end": v(3638.98, 4781.55) * mm});
            skLineSegment(sketch, "E1653", {"start": v(3638.98, 4781.55) * mm, "end": v(3602.8, 4786.98) * mm});
            skLineSegment(sketch, "E1654", {"start": v(3602.8, 4786.98) * mm, "end": v(3568.04, 4799.55) * mm});
            skLineSegment(sketch, "E1655", {"start": v(3568.04, 4799.55) * mm, "end": v(3535.77, 4819.4) * mm});
            skLineSegment(sketch, "E1656", {"start": v(3535.77, 4819.4) * mm, "end": v(3507.4, 4844.58) * mm});
            skLineSegment(sketch, "E1657", {"start": v(3507.4, 4844.58) * mm, "end": v(3485.1, 4874.08) * mm});
            skLineSegment(sketch, "E1658", {"start": v(3485.1, 4874.08) * mm, "end": v(3469.07, 4906.92) * mm});
            skLineSegment(sketch, "E1659", {"start": v(3469.07, 4906.92) * mm, "end": v(3459.54, 4942.07) * mm});
            skLineSegment(sketch, "E1660", {"start": v(3459.54, 4942.07) * mm, "end": v(3456.75, 4978.51) * mm});
            skLineSegment(sketch, "E1661", {"start": v(3456.75, 4978.51) * mm, "end": v(3460.9, 5015.25) * mm});
            skLineSegment(sketch, "E1662", {"start": v(3460.9, 5015.25) * mm, "end": v(3472.21, 5051.26) * mm});
            skLineSegment(sketch, "E1663", {"start": v(3472.21, 5051.26) * mm, "end": v(3490.91, 5085.52) * mm});
            skLineSegment(sketch, "E1664", {"start": v(4892.4, 3758.25) * mm, "end": v(4925.62, 3778.92) * mm});
            skLineSegment(sketch, "E1665", {"start": v(4925.62, 3778.92) * mm, "end": v(4961.12, 3791.72) * mm});
            skLineSegment(sketch, "E1666", {"start": v(4961.12, 3791.72) * mm, "end": v(4997.86, 3796.85) * mm});
            skLineSegment(sketch, "E1667", {"start": v(4997.86, 3796.85) * mm, "end": v(5034.77, 3794.5) * mm});
            skLineSegment(sketch, "E1668", {"start": v(5034.77, 3794.5) * mm, "end": v(5070.79, 3784.87) * mm});
            skLineSegment(sketch, "E1669", {"start": v(5070.79, 3784.87) * mm, "end": v(5104.85, 3768.15) * mm});
            skLineSegment(sketch, "E1670", {"start": v(5104.85, 3768.15) * mm, "end": v(5135.9, 3744.55) * mm});
            skLineSegment(sketch, "E1671", {"start": v(5135.9, 3744.55) * mm, "end": v(5162.87, 3714.25) * mm});
            skLineSegment(sketch, "E1672", {"start": v(5162.87, 3714.25) * mm, "end": v(5183.73, 3679.54) * mm});
            skLineSegment(sketch, "E1673", {"start": v(5183.73, 3679.54) * mm, "end": v(5196.44, 3642.73) * mm});
            skLineSegment(sketch, "E1674", {"start": v(5196.44, 3642.73) * mm, "end": v(5201.3, 3604.99) * mm});
            skLineSegment(sketch, "E1675", {"start": v(5201.3, 3604.99) * mm, "end": v(5198.59, 3567.47) * mm});
            skLineSegment(sketch, "E1676", {"start": v(5198.59, 3567.47) * mm, "end": v(5188.6, 3531.37) * mm});
            skLineSegment(sketch, "E1677", {"start": v(5188.6, 3531.37) * mm, "end": v(5171.65, 3497.83) * mm});
            skLineSegment(sketch, "E1678", {"start": v(5171.65, 3497.83) * mm, "end": v(5148.02, 3468.03) * mm});
            skLineSegment(sketch, "E1679", {"start": v(5148.02, 3468.03) * mm, "end": v(5117.99, 3443.14) * mm});
            skLineSegment(sketch, "E1680", {"start": v(5117.99, 3443.14) * mm, "end": v(5083.71, 3424.87) * mm});
            skLineSegment(sketch, "E1681", {"start": v(5083.71, 3424.87) * mm, "end": v(5047.77, 3414) * mm});
            skLineSegment(sketch, "E1682", {"start": v(5047.77, 3414) * mm, "end": v(5011.12, 3410.28) * mm});
            skLineSegment(sketch, "E1683", {"start": v(5011.12, 3410.28) * mm, "end": v(4974.73, 3413.44) * mm});
            skLineSegment(sketch, "E1684", {"start": v(4974.73, 3413.44) * mm, "end": v(4939.57, 3423.21) * mm});
            skLineSegment(sketch, "E1685", {"start": v(4939.57, 3423.21) * mm, "end": v(4906.6, 3439.34) * mm});
            skLineSegment(sketch, "E1686", {"start": v(4906.6, 3439.34) * mm, "end": v(4876.78, 3461.56) * mm});
            skLineSegment(sketch, "E1687", {"start": v(4876.78, 3461.56) * mm, "end": v(4851.08, 3489.62) * mm});
            skLineSegment(sketch, "E1688", {"start": v(4851.08, 3489.62) * mm, "end": v(4831.96, 3522.4) * mm});
            skLineSegment(sketch, "E1689", {"start": v(4831.96, 3522.4) * mm, "end": v(4820.17, 3557.62) * mm});
            skLineSegment(sketch, "E1690", {"start": v(4820.17, 3557.62) * mm, "end": v(4815.5, 3594.16) * mm});
            skLineSegment(sketch, "E1691", {"start": v(4815.5, 3594.16) * mm, "end": v(4817.79, 3630.93) * mm});
            skLineSegment(sketch, "E1692", {"start": v(4817.79, 3630.93) * mm, "end": v(4826.81, 3666.83) * mm});
            skLineSegment(sketch, "E1693", {"start": v(4826.81, 3666.83) * mm, "end": v(4842.38, 3700.75) * mm});
            skLineSegment(sketch, "E1694", {"start": v(4842.38, 3700.75) * mm, "end": v(4864.32, 3731.59) * mm});
            skLineSegment(sketch, "E1695", {"start": v(4864.32, 3731.59) * mm, "end": v(4892.4, 3758.25) * mm});
            skLineSegment(sketch, "E1696", {"start": v(5814.17, 2062.47) * mm, "end": v(5851.81, 2071.74) * mm});
            skLineSegment(sketch, "E1697", {"start": v(5851.81, 2071.74) * mm, "end": v(5889.67, 2072.97) * mm});
            skLineSegment(sketch, "E1698", {"start": v(5889.67, 2072.97) * mm, "end": v(5926.66, 2066.63) * mm});
            skLineSegment(sketch, "E1699", {"start": v(5926.66, 2066.63) * mm, "end": v(5961.68, 2053.19) * mm});
            skLineSegment(sketch, "E1700", {"start": v(5961.68, 2053.19) * mm, "end": v(5993.63, 2033.1) * mm});
            skLineSegment(sketch, "E1701", {"start": v(5993.63, 2033.1) * mm, "end": v(6021.43, 2006.86) * mm});
            skLineSegment(sketch, "E1702", {"start": v(6021.43, 2006.86) * mm, "end": v(6043.99, 1974.91) * mm});
            skLineSegment(sketch, "E1703", {"start": v(6043.99, 1974.91) * mm, "end": v(6060.2, 1937.73) * mm});
            skLineSegment(sketch, "E1704", {"start": v(6060.2, 1937.73) * mm, "end": v(6068.04, 1897.87) * mm});
            skLineSegment(sketch, "E1705", {"start": v(6068.04, 1897.87) * mm, "end": v(6068.06, 1858.7) * mm});
            skLineSegment(sketch, "E1706", {"start": v(6068.06, 1858.7) * mm, "end": v(6060.76, 1821.23) * mm});
            skLineSegment(sketch, "E1707", {"start": v(6060.76, 1821.23) * mm, "end": v(6046.67, 1786.42) * mm});
            skLineSegment(sketch, "E1708", {"start": v(6046.67, 1786.42) * mm, "end": v(6026.3, 1755.26) * mm});
            skLineSegment(sketch, "E1709", {"start": v(6026.3, 1755.26) * mm, "end": v(6000.16, 1728.72) * mm});
            skLineSegment(sketch, "E1710", {"start": v(6000.16, 1728.72) * mm, "end": v(5968.77, 1707.8) * mm});
            skLineSegment(sketch, "E1711", {"start": v(5968.77, 1707.8) * mm, "end": v(5932.64, 1693.48) * mm});
            skLineSegment(sketch, "E1712", {"start": v(5932.64, 1693.48) * mm, "end": v(5894.25, 1686.7) * mm});
            skLineSegment(sketch, "E1713", {"start": v(5894.25, 1686.7) * mm, "end": v(5856.4, 1687.43) * mm});
            skLineSegment(sketch, "E1714", {"start": v(5856.4, 1687.43) * mm, "end": v(5820.03, 1695.15) * mm});
            skLineSegment(sketch, "E1715", {"start": v(5820.03, 1695.15) * mm, "end": v(5786.11, 1709.34) * mm});
            skLineSegment(sketch, "E1716", {"start": v(5786.11, 1709.34) * mm, "end": v(5755.6, 1729.5) * mm});
            skLineSegment(sketch, "E1717", {"start": v(5755.6, 1729.5) * mm, "end": v(5729.48, 1755.12) * mm});
            skLineSegment(sketch, "E1718", {"start": v(5729.48, 1755.12) * mm, "end": v(5708.68, 1785.69) * mm});
            skLineSegment(sketch, "E1719", {"start": v(5708.68, 1785.69) * mm, "end": v(5694.18, 1820.68) * mm});
            skLineSegment(sketch, "E1720", {"start": v(5694.18, 1820.68) * mm, "end": v(5686.21, 1857.77) * mm});
            skLineSegment(sketch, "E1721", {"start": v(5686.21, 1857.77) * mm, "end": v(5685.57, 1894.77) * mm});
            skLineSegment(sketch, "E1722", {"start": v(5685.57, 1894.77) * mm, "end": v(5691.87, 1930.76) * mm});
            skLineSegment(sketch, "E1723", {"start": v(5691.87, 1930.76) * mm, "end": v(5704.74, 1964.78) * mm});
            skLineSegment(sketch, "E1724", {"start": v(5704.74, 1964.78) * mm, "end": v(5723.78, 1995.9) * mm});
            skLineSegment(sketch, "E1725", {"start": v(5723.78, 1995.9) * mm, "end": v(5748.62, 2023.18) * mm});
            skLineSegment(sketch, "E1726", {"start": v(5748.62, 2023.18) * mm, "end": v(5778.88, 2045.68) * mm});
            skLineSegment(sketch, "E1727", {"start": v(5778.88, 2045.68) * mm, "end": v(5814.17, 2062.47) * mm});
            skLineSegment(sketch, "E1728", {"start": v(7846.68, 249.95) * mm, "end": v(7761.7, 249.78) * mm});
            skLineSegment(sketch, "E1729", {"start": v(7761.7, 249.78) * mm, "end": v(7656.06, 257) * mm});
            skLineSegment(sketch, "E1730", {"start": v(7656.06, 257) * mm, "end": v(7539.62, 269.3) * mm});
            skLineSegment(sketch, "E1731", {"start": v(7539.62, 269.3) * mm, "end": v(7422.25, 284.47) * mm});
            skLineSegment(sketch, "E1732", {"start": v(7422.25, 284.47) * mm, "end": v(7313.8, 300.2) * mm});
            skLineSegment(sketch, "E1733", {"start": v(7313.8, 300.2) * mm, "end": v(7224.13, 314.25) * mm});
            skLineSegment(sketch, "E1734", {"start": v(7224.13, 314.25) * mm, "end": v(7163.1, 324.34) * mm});
            skLineSegment(sketch, "E1735", {"start": v(7163.1, 324.34) * mm, "end": v(7140.56, 328.2) * mm});
            skLineSegment(sketch, "E1736", {"start": v(7140.56, 328.2) * mm, "end": v(7129.4, 348.9) * mm});
            skLineSegment(sketch, "E1737", {"start": v(7129.4, 348.9) * mm, "end": v(7115.54, 367.68) * mm});
            skLineSegment(sketch, "E1738", {"start": v(7115.54, 367.68) * mm, "end": v(7099.23, 384.3) * mm});
            skLineSegment(sketch, "E1739", {"start": v(7099.23, 384.3) * mm, "end": v(7080.73, 398.48) * mm});
            skLineSegment(sketch, "E1740", {"start": v(7080.73, 398.48) * mm, "end": v(7060.3, 409.97) * mm});
            skLineSegment(sketch, "E1741", {"start": v(7060.3, 409.97) * mm, "end": v(7038.18, 418.5) * mm});
            skLineSegment(sketch, "E1742", {"start": v(7038.18, 418.5) * mm, "end": v(7014.64, 423.81) * mm});
            skLineSegment(sketch, "E1743", {"start": v(7014.64, 423.81) * mm, "end": v(6989.94, 425.64) * mm});
            skLineSegment(sketch, "E1744", {"start": v(6989.94, 425.64) * mm, "end": v(6815.67, 425.64) * mm});
            skLineSegment(sketch, "E1745", {"start": v(6815.67, 425.64) * mm, "end": v(6755.17, 1005.66) * mm});
            skLineSegment(sketch, "E1746", {"start": v(6755.17, 1005.66) * mm, "end": v(6647.3, 1570.21) * mm});
            skLineSegment(sketch, "E1747", {"start": v(6647.3, 1570.21) * mm, "end": v(6494.12, 2117.24) * mm});
            skLineSegment(sketch, "E1748", {"start": v(6494.12, 2117.24) * mm, "end": v(6297.67, 2644.71) * mm});
            skLineSegment(sketch, "E1749", {"start": v(6297.67, 2644.71) * mm, "end": v(6060, 3150.6) * mm});
            skLineSegment(sketch, "E1750", {"start": v(6060, 3150.6) * mm, "end": v(5783.17, 3632.83) * mm});
            skLineSegment(sketch, "E1751", {"start": v(5783.17, 3632.83) * mm, "end": v(5469.23, 4089.4) * mm});
            skLineSegment(sketch, "E1752", {"start": v(5469.23, 4089.4) * mm, "end": v(5120.22, 4518.24) * mm});
            skLineSegment(sketch, "E1753", {"start": v(5120.22, 4518.24) * mm, "end": v(5243.61, 4641.66) * mm});
            skLineSegment(sketch, "E1754", {"start": v(5243.61, 4641.66) * mm, "end": v(5259.78, 4660.43) * mm});
            skLineSegment(sketch, "E1755", {"start": v(5259.78, 4660.43) * mm, "end": v(5272.65, 4680.85) * mm});
            skLineSegment(sketch, "E1756", {"start": v(5272.65, 4680.85) * mm, "end": v(5282.23, 4702.54) * mm});
            skLineSegment(sketch, "E1757", {"start": v(5282.23, 4702.54) * mm, "end": v(5288.53, 4725.13) * mm});
            skLineSegment(sketch, "E1758", {"start": v(5288.53, 4725.13) * mm, "end": v(5291.57, 4748.25) * mm});
            skLineSegment(sketch, "E1759", {"start": v(5291.57, 4748.25) * mm, "end": v(5291.36, 4771.53) * mm});
            skLineSegment(sketch, "E1760", {"start": v(5291.36, 4771.53) * mm, "end": v(5287.9, 4794.58) * mm});
            skLineSegment(sketch, "E1761", {"start": v(5287.9, 4794.58) * mm, "end": v(5281.23, 4817.05) * mm});
            skLineSegment(sketch, "E1762", {"start": v(5281.23, 4817.05) * mm, "end": v(5382.62, 4960.62) * mm});
            skLineSegment(sketch, "E1763", {"start": v(5382.62, 4960.62) * mm, "end": v(5460.49, 5069.99) * mm});
            skLineSegment(sketch, "E1764", {"start": v(5460.49, 5069.99) * mm, "end": v(5520.04, 5151.65) * mm});
            skLineSegment(sketch, "E1765", {"start": v(5520.04, 5151.65) * mm, "end": v(5566.46, 5212.1) * mm});
            skLineSegment(sketch, "E1766", {"start": v(5566.46, 5212.1) * mm, "end": v(5604.97, 5257.85) * mm});
            skLineSegment(sketch, "E1767", {"start": v(5604.97, 5257.85) * mm, "end": v(5640.77, 5295.4) * mm});
            skLineSegment(sketch, "E1768", {"start": v(5640.77, 5295.4) * mm, "end": v(5679.04, 5331.25) * mm});
            skLineSegment(sketch, "E1769", {"start": v(5679.04, 5331.25) * mm, "end": v(5725, 5371.9) * mm});
            skLineSegment(sketch, "E1770", {"start": v(5725, 5371.9) * mm, "end": v(5809.35, 5436.9) * mm});
            skLineSegment(sketch, "E1771", {"start": v(5809.35, 5436.9) * mm, "end": v(5917.66, 5514.62) * mm});
            skLineSegment(sketch, "E1772", {"start": v(5917.66, 5514.62) * mm, "end": v(6034.72, 5603.65) * mm});
            skLineSegment(sketch, "E1773", {"start": v(6034.72, 5603.65) * mm, "end": v(6145.28, 5702.58) * mm});
            skLineSegment(sketch, "E1774", {"start": v(6145.28, 5702.58) * mm, "end": v(6234.13, 5810.03) * mm});
            skLineSegment(sketch, "E1775", {"start": v(6234.13, 5810.03) * mm, "end": v(6286.04, 5924.57) * mm});
            skLineSegment(sketch, "E1776", {"start": v(6286.04, 5924.57) * mm, "end": v(6285.79, 6044.82) * mm});
            skLineSegment(sketch, "E1777", {"start": v(6285.79, 6044.82) * mm, "end": v(6218.14, 6169.37) * mm});
            skLineSegment(sketch, "E1778", {"start": v(6218.14, 6169.37) * mm, "end": v(6084.56, 6266.46) * mm});
            skLineSegment(sketch, "E1779", {"start": v(6084.56, 6266.46) * mm, "end": v(5960.34, 6290.53) * mm});
            skLineSegment(sketch, "E1780", {"start": v(5960.34, 6290.53) * mm, "end": v(5844.76, 6256.3) * mm});
            skLineSegment(sketch, "E1781", {"start": v(5844.76, 6256.3) * mm, "end": v(5737.12, 6178.47) * mm});
            skLineSegment(sketch, "E1782", {"start": v(5737.12, 6178.47) * mm, "end": v(5636.7, 6071.74) * mm});
            skLineSegment(sketch, "E1783", {"start": v(5636.7, 6071.74) * mm, "end": v(5542.8, 5950.8) * mm});
            skLineSegment(sketch, "E1784", {"start": v(5542.8, 5950.8) * mm, "end": v(5454.71, 5830.39) * mm});
            skLineSegment(sketch, "E1785", {"start": v(5454.71, 5830.39) * mm, "end": v(5371.7, 5725.17) * mm});
            skLineSegment(sketch, "E1786", {"start": v(5371.7, 5725.17) * mm, "end": v(5311.73, 5664.97) * mm});
            skLineSegment(sketch, "E1787", {"start": v(5311.73, 5664.97) * mm, "end": v(5231.93, 5595.37) * mm});
            skLineSegment(sketch, "E1788", {"start": v(5231.93, 5595.37) * mm, "end": v(5140.89, 5521.75) * mm});
            skLineSegment(sketch, "E1789", {"start": v(5140.89, 5521.75) * mm, "end": v(5047.17, 5449.48) * mm});
            skLineSegment(sketch, "E1790", {"start": v(5047.17, 5449.48) * mm, "end": v(4959.36, 5383.92) * mm});
            skLineSegment(sketch, "E1791", {"start": v(4959.36, 5383.92) * mm, "end": v(4886.03, 5330.45) * mm});
            skLineSegment(sketch, "E1792", {"start": v(4886.03, 5330.45) * mm, "end": v(4835.74, 5294.43) * mm});
            skLineSegment(sketch, "E1793", {"start": v(4835.74, 5294.43) * mm, "end": v(4817.07, 5281.23) * mm});
            skLineSegment(sketch, "E1794", {"start": v(4817.07, 5281.23) * mm, "end": v(4794.55, 5287.96) * mm});
            skLineSegment(sketch, "E1795", {"start": v(4794.55, 5287.96) * mm, "end": v(4771.47, 5291.43) * mm});
            skLineSegment(sketch, "E1796", {"start": v(4771.47, 5291.43) * mm, "end": v(4748.2, 5291.65) * mm});
            skLineSegment(sketch, "E1797", {"start": v(4748.2, 5291.65) * mm, "end": v(4725.08, 5288.6) * mm});
            skLineSegment(sketch, "E1798", {"start": v(4725.08, 5288.6) * mm, "end": v(4702.51, 5282.27) * mm});
            skLineSegment(sketch, "E1799", {"start": v(4702.51, 5282.27) * mm, "end": v(4680.84, 5272.67) * mm});
            skLineSegment(sketch, "E1800", {"start": v(4680.84, 5272.67) * mm, "end": v(4660.45, 5259.79) * mm});
            skLineSegment(sketch, "E1801", {"start": v(4660.45, 5259.79) * mm, "end": v(4641.68, 5243.61) * mm});
            skLineSegment(sketch, "E1802", {"start": v(4641.68, 5243.61) * mm, "end": v(4518.3, 5120.2) * mm});
            skLineSegment(sketch, "E1803", {"start": v(4518.3, 5120.2) * mm, "end": v(4089.44, 5469.25) * mm});
            skLineSegment(sketch, "E1804", {"start": v(4089.44, 5469.25) * mm, "end": v(3632.88, 5783.23) * mm});
            skLineSegment(sketch, "E1805", {"start": v(3632.88, 5783.23) * mm, "end": v(3150.63, 6060.1) * mm});
            skLineSegment(sketch, "E1806", {"start": v(3150.63, 6060.1) * mm, "end": v(2644.75, 6297.79) * mm});
            skLineSegment(sketch, "E1807", {"start": v(2644.75, 6297.79) * mm, "end": v(2117.28, 6494.26) * mm});
            skLineSegment(sketch, "E1808", {"start": v(2117.28, 6494.26) * mm, "end": v(1570.24, 6647.46) * mm});
            skLineSegment(sketch, "E1809", {"start": v(1570.24, 6647.46) * mm, "end": v(1005.7, 6755.34) * mm});
            skLineSegment(sketch, "E1810", {"start": v(1005.7, 6755.34) * mm, "end": v(425.67, 6815.85) * mm});
            skLineSegment(sketch, "E1811", {"start": v(425.67, 6815.85) * mm, "end": v(425.67, 6989.97) * mm});
            skLineSegment(sketch, "E1812", {"start": v(425.67, 6989.97) * mm, "end": v(423.82, 7014.66) * mm});
            skLineSegment(sketch, "E1813", {"start": v(423.82, 7014.66) * mm, "end": v(418.48, 7038.2) * mm});
            skLineSegment(sketch, "E1814", {"start": v(418.48, 7038.2) * mm, "end": v(409.91, 7060.3) * mm});
            skLineSegment(sketch, "E1815", {"start": v(409.91, 7060.3) * mm, "end": v(398.39, 7080.74) * mm});
            skLineSegment(sketch, "E1816", {"start": v(398.39, 7080.74) * mm, "end": v(384.19, 7099.24) * mm});
            skLineSegment(sketch, "E1817", {"start": v(384.19, 7099.24) * mm, "end": v(367.58, 7115.55) * mm});
            skLineSegment(sketch, "E1818", {"start": v(367.58, 7115.55) * mm, "end": v(348.83, 7129.42) * mm});
            skLineSegment(sketch, "E1819", {"start": v(348.83, 7129.42) * mm, "end": v(328.23, 7140.59) * mm});
            skLineSegment(sketch, "E1820", {"start": v(328.23, 7140.59) * mm, "end": v(298.4, 7313.8) * mm});
            skLineSegment(sketch, "E1821", {"start": v(298.4, 7313.8) * mm, "end": v(276.13, 7446.19) * mm});
            skLineSegment(sketch, "E1822", {"start": v(276.13, 7446.19) * mm, "end": v(260.5, 7546.03) * mm});
            skLineSegment(sketch, "E1823", {"start": v(260.5, 7546.03) * mm, "end": v(250.58, 7621.6) * mm});
            skLineSegment(sketch, "E1824", {"start": v(250.58, 7621.6) * mm, "end": v(245.46, 7681.18) * mm});
            skLineSegment(sketch, "E1825", {"start": v(245.46, 7681.18) * mm, "end": v(244.22, 7733.04) * mm});
            skLineSegment(sketch, "E1826", {"start": v(244.22, 7733.04) * mm, "end": v(245.94, 7785.45) * mm});
            skLineSegment(sketch, "E1827", {"start": v(245.94, 7785.45) * mm, "end": v(249.7, 7846.68) * mm});
            skLineSegment(sketch, "E1828", {"start": v(249.7, 7846.68) * mm, "end": v(263.37, 7952.3) * mm});
            skLineSegment(sketch, "E1829", {"start": v(263.37, 7952.3) * mm, "end": v(285, 8083.84) * mm});
            skLineSegment(sketch, "E1830", {"start": v(285, 8083.84) * mm, "end": v(304.82, 8229.57) * mm});
            skLineSegment(sketch, "E1831", {"start": v(304.82, 8229.57) * mm, "end": v(313.05, 8377.71) * mm});
            skLineSegment(sketch, "E1832", {"start": v(313.05, 8377.71) * mm, "end": v(299.9, 8516.52) * mm});
            skLineSegment(sketch, "E1833", {"start": v(299.9, 8516.52) * mm, "end": v(255.61, 8634.22) * mm});
            skLineSegment(sketch, "E1834", {"start": v(255.61, 8634.22) * mm, "end": v(170.4, 8719.06) * mm});
            skLineSegment(sketch, "E1835", {"start": v(170.4, 8719.06) * mm, "end": v(34.5, 8759.28) * mm});
            skLineSegment(sketch, "E1836", {"start": v(34.5, 8759.28) * mm, "end": v(-128.6, 8733.48) * mm});
            skLineSegment(sketch, "E1837", {"start": v(-128.6, 8733.48) * mm, "end": v(-233.48, 8662.67) * mm});
            skLineSegment(sketch, "E1838", {"start": v(-233.48, 8662.67) * mm, "end": v(-291, 8556.74) * mm});
            skLineSegment(sketch, "E1839", {"start": v(-291, 8556.74) * mm, "end": v(-312.08, 8425.6) * mm});
            skLineSegment(sketch, "E1840", {"start": v(-312.08, 8425.6) * mm, "end": v(-307.61, 8279.12) * mm});
            skLineSegment(sketch, "E1841", {"start": v(-307.61, 8279.12) * mm, "end": v(-288.5, 8127.22) * mm});
            skLineSegment(sketch, "E1842", {"start": v(-288.5, 8127.22) * mm, "end": v(-265.65, 7979.77) * mm});
            skLineSegment(sketch, "E1843", {"start": v(-265.65, 7979.77) * mm, "end": v(-249.95, 7846.68) * mm});
            skLineSegment(sketch, "E1844", {"start": v(-249.95, 7846.68) * mm, "end": v(-249.78, 7761.7) * mm});
            skLineSegment(sketch, "E1845", {"start": v(-249.78, 7761.7) * mm, "end": v(-257, 7656.06) * mm});
            skLineSegment(sketch, "E1846", {"start": v(-257, 7656.06) * mm, "end": v(-269.3, 7539.63) * mm});
            skLineSegment(sketch, "E1847", {"start": v(-269.3, 7539.63) * mm, "end": v(-284.47, 7422.26) * mm});
            skLineSegment(sketch, "E1848", {"start": v(-284.47, 7422.26) * mm, "end": v(-300.2, 7313.82) * mm});
            skLineSegment(sketch, "E1849", {"start": v(-300.2, 7313.82) * mm, "end": v(-314.25, 7224.15) * mm});
            skLineSegment(sketch, "E1850", {"start": v(-314.25, 7224.15) * mm, "end": v(-324.34, 7163.12) * mm});
            skLineSegment(sketch, "E1851", {"start": v(-324.34, 7163.12) * mm, "end": v(-328.2, 7140.59) * mm});
            skLineSegment(sketch, "E1852", {"start": v(-328.2, 7140.59) * mm, "end": v(-348.89, 7129.42) * mm});
            skLineSegment(sketch, "E1853", {"start": v(-348.89, 7129.42) * mm, "end": v(-367.66, 7115.55) * mm});
            skLineSegment(sketch, "E1854", {"start": v(-367.66, 7115.55) * mm, "end": v(-384.28, 7099.24) * mm});
            skLineSegment(sketch, "E1855", {"start": v(-384.28, 7099.24) * mm, "end": v(-398.46, 7080.74) * mm});
            skLineSegment(sketch, "E1856", {"start": v(-398.46, 7080.74) * mm, "end": v(-409.94, 7060.3) * mm});
            skLineSegment(sketch, "E1857", {"start": v(-409.94, 7060.3) * mm, "end": v(-418.47, 7038.2) * mm});
            skLineSegment(sketch, "E1858", {"start": v(-418.47, 7038.2) * mm, "end": v(-423.79, 7014.66) * mm});
            skLineSegment(sketch, "E1859", {"start": v(-423.79, 7014.66) * mm, "end": v(-425.62, 6989.97) * mm});
            skLineSegment(sketch, "E1860", {"start": v(-425.62, 6989.97) * mm, "end": v(-425.62, 6815.85) * mm});
            skLineSegment(sketch, "E1861", {"start": v(-425.62, 6815.85) * mm, "end": v(-1005.65, 6755.35) * mm});
            skLineSegment(sketch, "E1862", {"start": v(-1005.65, 6755.35) * mm, "end": v(-1570.2, 6647.48) * mm});
            skLineSegment(sketch, "E1863", {"start": v(-1570.2, 6647.48) * mm, "end": v(-2117.24, 6494.28) * mm});
            skLineSegment(sketch, "E1864", {"start": v(-2117.24, 6494.28) * mm, "end": v(-2644.72, 6297.8) * mm});
            skLineSegment(sketch, "E1865", {"start": v(-2644.72, 6297.8) * mm, "end": v(-3150.6, 6060.12) * mm});
            skLineSegment(sketch, "E1866", {"start": v(-3150.6, 6060.12) * mm, "end": v(-3632.85, 5783.26) * mm});
            skLineSegment(sketch, "E1867", {"start": v(-3632.85, 5783.26) * mm, "end": v(-4089.42, 5469.27) * mm});
            skLineSegment(sketch, "E1868", {"start": v(-4089.42, 5469.27) * mm, "end": v(-4518.27, 5120.22) * mm});
            skLineSegment(sketch, "E1869", {"start": v(-4518.27, 5120.22) * mm, "end": v(-4641.66, 5243.64) * mm});
            skLineSegment(sketch, "E1870", {"start": v(-4641.66, 5243.64) * mm, "end": v(-4660.43, 5259.8) * mm});
            skLineSegment(sketch, "E1871", {"start": v(-4660.43, 5259.8) * mm, "end": v(-4680.85, 5272.67) * mm});
            skLineSegment(sketch, "E1872", {"start": v(-4680.85, 5272.67) * mm, "end": v(-4702.54, 5282.25) * mm});
            skLineSegment(sketch, "E1873", {"start": v(-4702.54, 5282.25) * mm, "end": v(-4725.13, 5288.56) * mm});
            skLineSegment(sketch, "E1874", {"start": v(-4725.13, 5288.56) * mm, "end": v(-4748.25, 5291.6) * mm});
            skLineSegment(sketch, "E1875", {"start": v(-4748.25, 5291.6) * mm, "end": v(-4771.53, 5291.38) * mm});
            skLineSegment(sketch, "E1876", {"start": v(-4771.53, 5291.38) * mm, "end": v(-4794.58, 5287.93) * mm});
            skLineSegment(sketch, "E1877", {"start": v(-4794.58, 5287.93) * mm, "end": v(-4817.05, 5281.26) * mm});
            skLineSegment(sketch, "E1878", {"start": v(-4817.05, 5281.26) * mm, "end": v(-4960.62, 5382.64) * mm});
            skLineSegment(sketch, "E1879", {"start": v(-4960.62, 5382.64) * mm, "end": v(-5069.99, 5460.5) * mm});
            skLineSegment(sketch, "E1880", {"start": v(-5069.99, 5460.5) * mm, "end": v(-5151.65, 5520.04) * mm});
            skLineSegment(sketch, "E1881", {"start": v(-5151.65, 5520.04) * mm, "end": v(-5212.1, 5566.47) * mm});
            skLineSegment(sketch, "E1882", {"start": v(-5212.1, 5566.47) * mm, "end": v(-5257.85, 5604.98) * mm});
            skLineSegment(sketch, "E1883", {"start": v(-5257.85, 5604.98) * mm, "end": v(-5295.4, 5640.77) * mm});
            skLineSegment(sketch, "E1884", {"start": v(-5295.4, 5640.77) * mm, "end": v(-5331.24, 5679.04) * mm});
            skLineSegment(sketch, "E1885", {"start": v(-5331.24, 5679.04) * mm, "end": v(-5371.88, 5725) * mm});
            skLineSegment(sketch, "E1886", {"start": v(-5371.88, 5725) * mm, "end": v(-5436.89, 5809.35) * mm});
            skLineSegment(sketch, "E1887", {"start": v(-5436.89, 5809.35) * mm, "end": v(-5514.6, 5917.66) * mm});
            skLineSegment(sketch, "E1888", {"start": v(-5514.6, 5917.66) * mm, "end": v(-5603.64, 6034.72) * mm});
            skLineSegment(sketch, "E1889", {"start": v(-5603.64, 6034.72) * mm, "end": v(-5702.58, 6145.29) * mm});
            skLineSegment(sketch, "E1890", {"start": v(-5702.58, 6145.29) * mm, "end": v(-5810.02, 6234.14) * mm});
            skLineSegment(sketch, "E1891", {"start": v(-5810.02, 6234.14) * mm, "end": v(-5924.56, 6286.05) * mm});
            skLineSegment(sketch, "E1892", {"start": v(-5924.56, 6286.05) * mm, "end": v(-6044.8, 6285.8) * mm});
            skLineSegment(sketch, "E1893", {"start": v(-6044.8, 6285.8) * mm, "end": v(-6169.34, 6218.16) * mm});
            skLineSegment(sketch, "E1894", {"start": v(-6169.34, 6218.16) * mm, "end": v(-6266.44, 6084.57) * mm});
            skLineSegment(sketch, "E1895", {"start": v(-6266.44, 6084.57) * mm, "end": v(-6290.52, 5960.35) * mm});
            skLineSegment(sketch, "E1896", {"start": v(-6290.52, 5960.35) * mm, "end": v(-6256.3, 5844.77) * mm});
            skLineSegment(sketch, "E1897", {"start": v(-6256.3, 5844.77) * mm, "end": v(-6178.47, 5737.13) * mm});
            skLineSegment(sketch, "E1898", {"start": v(-6178.47, 5737.13) * mm, "end": v(-6071.74, 5636.71) * mm});
            skLineSegment(sketch, "E1899", {"start": v(-6071.74, 5636.71) * mm, "end": v(-5950.8, 5542.8) * mm});
            skLineSegment(sketch, "E1900", {"start": v(-5950.8, 5542.8) * mm, "end": v(-5830.39, 5454.71) * mm});
            skLineSegment(sketch, "E1901", {"start": v(-5830.39, 5454.71) * mm, "end": v(-5725.17, 5371.7) * mm});
            skLineSegment(sketch, "E1902", {"start": v(-5725.17, 5371.7) * mm, "end": v(-5664.97, 5311.73) * mm});
            skLineSegment(sketch, "E1903", {"start": v(-5664.97, 5311.73) * mm, "end": v(-5595.37, 5231.94) * mm});
            skLineSegment(sketch, "E1904", {"start": v(-5595.37, 5231.94) * mm, "end": v(-5521.74, 5140.9) * mm});
            skLineSegment(sketch, "E1905", {"start": v(-5521.74, 5140.9) * mm, "end": v(-5449.47, 5047.18) * mm});
            skLineSegment(sketch, "E1906", {"start": v(-5449.47, 5047.18) * mm, "end": v(-5383.9, 4959.37) * mm});
            skLineSegment(sketch, "E1907", {"start": v(-5383.9, 4959.37) * mm, "end": v(-5330.43, 4886.03) * mm});
            skLineSegment(sketch, "E1908", {"start": v(-5330.43, 4886.03) * mm, "end": v(-5294.4, 4835.74) * mm});
            skLineSegment(sketch, "E1909", {"start": v(-5294.4, 4835.74) * mm, "end": v(-5281.2, 4817.07) * mm});
            skLineSegment(sketch, "E1910", {"start": v(-5281.2, 4817.07) * mm, "end": v(-5287.94, 4794.55) * mm});
            skLineSegment(sketch, "E1911", {"start": v(-5287.94, 4794.55) * mm, "end": v(-5291.42, 4771.47) * mm});
            skLineSegment(sketch, "E1912", {"start": v(-5291.42, 4771.47) * mm, "end": v(-5291.63, 4748.2) * mm});
            skLineSegment(sketch, "E1913", {"start": v(-5291.63, 4748.2) * mm, "end": v(-5288.58, 4725.08) * mm});
            skLineSegment(sketch, "E1914", {"start": v(-5288.58, 4725.08) * mm, "end": v(-5282.26, 4702.51) * mm});
            skLineSegment(sketch, "E1915", {"start": v(-5282.26, 4702.51) * mm, "end": v(-5272.65, 4680.84) * mm});
            skLineSegment(sketch, "E1916", {"start": v(-5272.65, 4680.84) * mm, "end": v(-5259.76, 4660.45) * mm});
            skLineSegment(sketch, "E1917", {"start": v(-5259.76, 4660.45) * mm, "end": v(-5243.59, 4641.68) * mm});
            skLineSegment(sketch, "E1918", {"start": v(-5243.59, 4641.68) * mm, "end": v(-5120.2, 4518.3) * mm});
            skLineSegment(sketch, "E1919", {"start": v(-5120.2, 4518.3) * mm, "end": v(-5469.21, 4089.44) * mm});
            skLineSegment(sketch, "E1920", {"start": v(-5469.21, 4089.44) * mm, "end": v(-5783.16, 3632.88) * mm});
            skLineSegment(sketch, "E1921", {"start": v(-5783.16, 3632.88) * mm, "end": v(-6060, 3150.64) * mm});
            skLineSegment(sketch, "E1922", {"start": v(-6060, 3150.64) * mm, "end": v(-6297.67, 2644.76) * mm});
            skLineSegment(sketch, "E1923", {"start": v(-6297.67, 2644.76) * mm, "end": v(-6494.12, 2117.29) * mm});
            skLineSegment(sketch, "E1924", {"start": v(-6494.12, 2117.29) * mm, "end": v(-6647.3, 1570.25) * mm});
            skLineSegment(sketch, "E1925", {"start": v(-6647.3, 1570.25) * mm, "end": v(-6755.17, 1005.7) * mm});
            skLineSegment(sketch, "E1926", {"start": v(-6755.17, 1005.7) * mm, "end": v(-6815.67, 425.67) * mm});
            skLineSegment(sketch, "E1927", {"start": v(-6815.67, 425.67) * mm, "end": v(-6989.97, 425.67) * mm});
            skLineSegment(sketch, "E1928", {"start": v(-6989.97, 425.67) * mm, "end": v(-7014.66, 423.83) * mm});
            skLineSegment(sketch, "E1929", {"start": v(-7014.66, 423.83) * mm, "end": v(-7038.2, 418.49) * mm});
            skLineSegment(sketch, "E1930", {"start": v(-7038.2, 418.49) * mm, "end": v(-7060.3, 409.92) * mm});
            skLineSegment(sketch, "E1931", {"start": v(-7060.3, 409.92) * mm, "end": v(-7080.73, 398.4) * mm});
            skLineSegment(sketch, "E1932", {"start": v(-7080.73, 398.4) * mm, "end": v(-7099.23, 384.2) * mm});
            skLineSegment(sketch, "E1933", {"start": v(-7099.23, 384.2) * mm, "end": v(-7115.54, 367.6) * mm});
            skLineSegment(sketch, "E1934", {"start": v(-7115.54, 367.6) * mm, "end": v(-7129.4, 348.86) * mm});
            skLineSegment(sketch, "E1935", {"start": v(-7129.4, 348.86) * mm, "end": v(-7140.56, 328.26) * mm});
            skLineSegment(sketch, "E1936", {"start": v(-7140.56, 328.26) * mm, "end": v(-7313.78, 298.42) * mm});
            skLineSegment(sketch, "E1937", {"start": v(-7313.78, 298.42) * mm, "end": v(-7446.18, 276.14) * mm});
            skLineSegment(sketch, "E1938", {"start": v(-7446.18, 276.14) * mm, "end": v(-7546.02, 260.5) * mm});
            skLineSegment(sketch, "E1939", {"start": v(-7546.02, 260.5) * mm, "end": v(-7621.6, 250.58) * mm});
            skLineSegment(sketch, "E1940", {"start": v(-7621.6, 250.58) * mm, "end": v(-7681.18, 245.46) * mm});
            skLineSegment(sketch, "E1941", {"start": v(-7681.18, 245.46) * mm, "end": v(-7733.04, 244.22) * mm});
            skLineSegment(sketch, "E1942", {"start": v(-7733.04, 244.22) * mm, "end": v(-7785.45, 245.94) * mm});
            skLineSegment(sketch, "E1943", {"start": v(-7785.45, 245.94) * mm, "end": v(-7846.68, 249.7) * mm});
            skLineSegment(sketch, "E1944", {"start": v(-7846.68, 249.7) * mm, "end": v(-7952.3, 263.38) * mm});
            skLineSegment(sketch, "E1945", {"start": v(-7952.3, 263.38) * mm, "end": v(-8083.84, 285.02) * mm});
            skLineSegment(sketch, "E1946", {"start": v(-8083.84, 285.02) * mm, "end": v(-8229.56, 304.83) * mm});
            skLineSegment(sketch, "E1947", {"start": v(-8229.56, 304.83) * mm, "end": v(-8377.7, 313.05) * mm});
            skLineSegment(sketch, "E1948", {"start": v(-8377.7, 313.05) * mm, "end": v(-8516.5, 299.9) * mm});
            skLineSegment(sketch, "E1949", {"start": v(-8516.5, 299.9) * mm, "end": v(-8634.2, 255.62) * mm});
            skLineSegment(sketch, "E1950", {"start": v(-8634.2, 255.62) * mm, "end": v(-8719.05, 170.4) * mm});
            skLineSegment(sketch, "E1951", {"start": v(-8719.05, 170.4) * mm, "end": v(-8759.28, 34.5) * mm});
            skLineSegment(sketch, "E1952", {"start": v(-8759.28, 34.5) * mm, "end": v(-8733.48, -128.6) * mm});
            skLineSegment(sketch, "E1953", {"start": v(-8733.48, -128.6) * mm, "end": v(-8662.67, -233.47) * mm});
            skLineSegment(sketch, "E1954", {"start": v(-8662.67, -233.47) * mm, "end": v(-8556.74, -290.99) * mm});
            skLineSegment(sketch, "E1955", {"start": v(-8556.74, -290.99) * mm, "end": v(-8425.6, -312.07) * mm});
            skLineSegment(sketch, "E1956", {"start": v(-8425.6, -312.07) * mm, "end": v(-8279.12, -307.6) * mm});
            skLineSegment(sketch, "E1957", {"start": v(-8279.12, -307.6) * mm, "end": v(-8127.22, -288.49) * mm});
            skLineSegment(sketch, "E1958", {"start": v(-8127.22, -288.49) * mm, "end": v(-7979.77, -265.63) * mm});
            skLineSegment(sketch, "E1959", {"start": v(-7979.77, -265.63) * mm, "end": v(-7846.68, -249.92) * mm});
            skLineSegment(sketch, "E1960", {"start": v(-7846.68, -249.92) * mm, "end": v(-7761.7, -249.76) * mm});
            skLineSegment(sketch, "E1961", {"start": v(-7761.7, -249.76) * mm, "end": v(-7656.06, -256.98) * mm});
            skLineSegment(sketch, "E1962", {"start": v(-7656.06, -256.98) * mm, "end": v(-7539.62, -269.3) * mm});
            skLineSegment(sketch, "E1963", {"start": v(-7539.62, -269.3) * mm, "end": v(-7422.25, -284.45) * mm});
            skLineSegment(sketch, "E1964", {"start": v(-7422.25, -284.45) * mm, "end": v(-7313.8, -300.18) * mm});
            skLineSegment(sketch, "E1965", {"start": v(-7313.8, -300.18) * mm, "end": v(-7224.13, -314.23) * mm});
            skLineSegment(sketch, "E1966", {"start": v(-7224.13, -314.23) * mm, "end": v(-7163.1, -324.31) * mm});
            skLineSegment(sketch, "E1967", {"start": v(-7163.1, -324.31) * mm, "end": v(-7140.56, -328.18) * mm});
            skLineSegment(sketch, "E1968", {"start": v(-7140.56, -328.18) * mm, "end": v(-7129.4, -348.87) * mm});
            skLineSegment(sketch, "E1969", {"start": v(-7129.4, -348.87) * mm, "end": v(-7115.54, -367.65) * mm});
            skLineSegment(sketch, "E1970", {"start": v(-7115.54, -367.65) * mm, "end": v(-7099.23, -384.27) * mm});
            skLineSegment(sketch, "E1971", {"start": v(-7099.23, -384.27) * mm, "end": v(-7080.73, -398.45) * mm});
            skLineSegment(sketch, "E1972", {"start": v(-7080.73, -398.45) * mm, "end": v(-7060.3, -409.94) * mm});
            skLineSegment(sketch, "E1973", {"start": v(-7060.3, -409.94) * mm, "end": v(-7038.2, -418.47) * mm});
            skLineSegment(sketch, "E1974", {"start": v(-7038.2, -418.47) * mm, "end": v(-7014.66, -423.79) * mm});
            skLineSegment(sketch, "E1975", {"start": v(-7014.66, -423.79) * mm, "end": v(-6989.97, -425.62) * mm});
            skLineSegment(sketch, "E1976", {"start": v(-6989.97, -425.62) * mm, "end": v(-6815.67, -425.62) * mm});
            skLineSegment(sketch, "E1977", {"start": v(-6815.67, -425.62) * mm, "end": v(-6755.17, -1005.64) * mm});
            skLineSegment(sketch, "E1978", {"start": v(-6755.17, -1005.64) * mm, "end": v(-6647.3, -1570.19) * mm});
            skLineSegment(sketch, "E1979", {"start": v(-6647.3, -1570.19) * mm, "end": v(-6494.1, -2117.22) * mm});
            skLineSegment(sketch, "E1980", {"start": v(-6494.1, -2117.22) * mm, "end": v(-6297.65, -2644.69) * mm});
            skLineSegment(sketch, "E1981", {"start": v(-6297.65, -2644.69) * mm, "end": v(-6059.98, -3150.57) * mm});
            skLineSegment(sketch, "E1982", {"start": v(-6059.98, -3150.57) * mm, "end": v(-5783.15, -3632.8) * mm});
            skLineSegment(sketch, "E1983", {"start": v(-5783.15, -3632.8) * mm, "end": v(-5469.2, -4089.37) * mm});
            skLineSegment(sketch, "E1984", {"start": v(-5469.2, -4089.37) * mm, "end": v(-5120.2, -4518.22) * mm});
            skLineSegment(sketch, "E1985", {"start": v(-5120.2, -4518.22) * mm, "end": v(-5243.64, -4641.63) * mm});
            skLineSegment(sketch, "E1986", {"start": v(-5243.64, -4641.63) * mm, "end": v(-5259.8, -4660.4) * mm});
            skLineSegment(sketch, "E1987", {"start": v(-5259.8, -4660.4) * mm, "end": v(-5272.67, -4680.82) * mm});
            skLineSegment(sketch, "E1988", {"start": v(-5272.67, -4680.82) * mm, "end": v(-5282.25, -4702.52) * mm});
            skLineSegment(sketch, "E1989", {"start": v(-5282.25, -4702.52) * mm, "end": v(-5288.56, -4725.11) * mm});
            skLineSegment(sketch, "E1990", {"start": v(-5288.56, -4725.11) * mm, "end": v(-5291.6, -4748.24) * mm});
            skLineSegment(sketch, "E1991", {"start": v(-5291.6, -4748.24) * mm, "end": v(-5291.38, -4771.51) * mm});
            skLineSegment(sketch, "E1992", {"start": v(-5291.38, -4771.51) * mm, "end": v(-5287.93, -4794.58) * mm});
            skLineSegment(sketch, "E1993", {"start": v(-5287.93, -4794.58) * mm, "end": v(-5281.26, -4817.05) * mm});
            skLineSegment(sketch, "E1994", {"start": v(-5281.26, -4817.05) * mm, "end": v(-5382.64, -4960.61) * mm});
            skLineSegment(sketch, "E1995", {"start": v(-5382.64, -4960.61) * mm, "end": v(-5460.5, -5069.97) * mm});
            skLineSegment(sketch, "E1996", {"start": v(-5460.5, -5069.97) * mm, "end": v(-5520.04, -5151.63) * mm});
            skLineSegment(sketch, "E1997", {"start": v(-5520.04, -5151.63) * mm, "end": v(-5566.47, -5212.08) * mm});
            skLineSegment(sketch, "E1998", {"start": v(-5566.47, -5212.08) * mm, "end": v(-5604.98, -5257.83) * mm});
            skLineSegment(sketch, "E1999", {"start": v(-5604.98, -5257.83) * mm, "end": v(-5640.77, -5295.38) * mm});
            skLineSegment(sketch, "E2000", {"start": v(-5640.77, -5295.38) * mm, "end": v(-5679.04, -5331.23) * mm});
            skLineSegment(sketch, "E2001", {"start": v(-5679.04, -5331.23) * mm, "end": v(-5725, -5371.88) * mm});
            skLineSegment(sketch, "E2002", {"start": v(-5725, -5371.88) * mm, "end": v(-5809.35, -5436.89) * mm});
            skLineSegment(sketch, "E2003", {"start": v(-5809.35, -5436.89) * mm, "end": v(-5917.66, -5514.6) * mm});
            skLineSegment(sketch, "E2004", {"start": v(-5917.66, -5514.6) * mm, "end": v(-6034.72, -5603.64) * mm});
            skLineSegment(sketch, "E2005", {"start": v(-6034.72, -5603.64) * mm, "end": v(-6145.29, -5702.58) * mm});
            skLineSegment(sketch, "E2006", {"start": v(-6145.29, -5702.58) * mm, "end": v(-6234.14, -5810.02) * mm});
            skLineSegment(sketch, "E2007", {"start": v(-6234.14, -5810.02) * mm, "end": v(-6286.05, -5924.56) * mm});
            skLineSegment(sketch, "E2008", {"start": v(-6286.05, -5924.56) * mm, "end": v(-6285.8, -6044.8) * mm});
            skLineSegment(sketch, "E2009", {"start": v(-6285.8, -6044.8) * mm, "end": v(-6218.16, -6169.34) * mm});
            skLineSegment(sketch, "E2010", {"start": v(-6218.16, -6169.34) * mm, "end": v(-6084.57, -6266.43) * mm});
            skLineSegment(sketch, "E2011", {"start": v(-6084.57, -6266.43) * mm, "end": v(-5960.35, -6290.51) * mm});
            skLineSegment(sketch, "E2012", {"start": v(-5960.35, -6290.51) * mm, "end": v(-5844.77, -6256.29) * mm});
            skLineSegment(sketch, "E2013", {"start": v(-5844.77, -6256.29) * mm, "end": v(-5737.13, -6178.46) * mm});
            skLineSegment(sketch, "E2014", {"start": v(-5737.13, -6178.46) * mm, "end": v(-5636.71, -6071.73) * mm});
            skLineSegment(sketch, "E2015", {"start": v(-5636.71, -6071.73) * mm, "end": v(-5542.8, -5950.8) * mm});
            skLineSegment(sketch, "E2016", {"start": v(-5542.8, -5950.8) * mm, "end": v(-5454.71, -5830.38) * mm});
            skLineSegment(sketch, "E2017", {"start": v(-5454.71, -5830.38) * mm, "end": v(-5371.7, -5725.17) * mm});
            skLineSegment(sketch, "E2018", {"start": v(-5371.7, -5725.17) * mm, "end": v(-5311.73, -5664.96) * mm});
            skLineSegment(sketch, "E2019", {"start": v(-5311.73, -5664.96) * mm, "end": v(-5231.94, -5595.36) * mm});
            skLineSegment(sketch, "E2020", {"start": v(-5231.94, -5595.36) * mm, "end": v(-5140.9, -5521.73) * mm});
            skLineSegment(sketch, "E2021", {"start": v(-5140.9, -5521.73) * mm, "end": v(-5047.18, -5449.46) * mm});
            skLineSegment(sketch, "E2022", {"start": v(-5047.18, -5449.46) * mm, "end": v(-4959.37, -5383.9) * mm});
            skLineSegment(sketch, "E2023", {"start": v(-4959.37, -5383.9) * mm, "end": v(-4886.03, -5330.43) * mm});
            skLineSegment(sketch, "E2024", {"start": v(-4886.03, -5330.43) * mm, "end": v(-4835.74, -5294.4) * mm});
            skLineSegment(sketch, "E2025", {"start": v(-4835.74, -5294.4) * mm, "end": v(-4817.07, -5281.2) * mm});
            skLineSegment(sketch, "E2026", {"start": v(-4817.07, -5281.2) * mm, "end": v(-4794.55, -5287.94) * mm});
            skLineSegment(sketch, "E2027", {"start": v(-4794.55, -5287.94) * mm, "end": v(-4771.47, -5291.42) * mm});
            skLineSegment(sketch, "E2028", {"start": v(-4771.47, -5291.42) * mm, "end": v(-4748.2, -5291.63) * mm});
            skLineSegment(sketch, "E2029", {"start": v(-4748.2, -5291.63) * mm, "end": v(-4725.08, -5288.58) * mm});
            skLineSegment(sketch, "E2030", {"start": v(-4725.08, -5288.58) * mm, "end": v(-4702.51, -5282.26) * mm});
            skLineSegment(sketch, "E2031", {"start": v(-4702.51, -5282.26) * mm, "end": v(-4680.84, -5272.65) * mm});
            skLineSegment(sketch, "E2032", {"start": v(-4680.84, -5272.65) * mm, "end": v(-4660.45, -5259.76) * mm});
            skLineSegment(sketch, "E2033", {"start": v(-4660.45, -5259.76) * mm, "end": v(-4641.68, -5243.59) * mm});
            skLineSegment(sketch, "E2034", {"start": v(-4641.68, -5243.59) * mm, "end": v(-4518.27, -5120.17) * mm});
            skLineSegment(sketch, "E2035", {"start": v(-4518.27, -5120.17) * mm, "end": v(-4089.43, -5469.22) * mm});
            skLineSegment(sketch, "E2036", {"start": v(-4089.43, -5469.22) * mm, "end": v(-3632.87, -5783.2) * mm});
            skLineSegment(sketch, "E2037", {"start": v(-3632.87, -5783.2) * mm, "end": v(-3150.63, -6060.08) * mm});
            skLineSegment(sketch, "E2038", {"start": v(-3150.63, -6060.08) * mm, "end": v(-2644.75, -6297.77) * mm});
            skLineSegment(sketch, "E2039", {"start": v(-2644.75, -6297.77) * mm, "end": v(-2117.27, -6494.25) * mm});
            skLineSegment(sketch, "E2040", {"start": v(-2117.27, -6494.25) * mm, "end": v(-1570.24, -6647.45) * mm});
            skLineSegment(sketch, "E2041", {"start": v(-1570.24, -6647.45) * mm, "end": v(-1005.7, -6755.32) * mm});
            skLineSegment(sketch, "E2042", {"start": v(-1005.7, -6755.32) * mm, "end": v(-425.67, -6815.82) * mm});
            skLineSegment(sketch, "E2043", {"start": v(-425.67, -6815.82) * mm, "end": v(-425.67, -6989.94) * mm});
            skLineSegment(sketch, "E2044", {"start": v(-425.67, -6989.94) * mm, "end": v(-423.83, -7014.64) * mm});
            skLineSegment(sketch, "E2045", {"start": v(-423.83, -7014.64) * mm, "end": v(-418.49, -7038.18) * mm});
            skLineSegment(sketch, "E2046", {"start": v(-418.49, -7038.18) * mm, "end": v(-409.92, -7060.3) * mm});
            skLineSegment(sketch, "E2047", {"start": v(-409.92, -7060.3) * mm, "end": v(-398.4, -7080.73) * mm});
            skLineSegment(sketch, "E2048", {"start": v(-398.4, -7080.73) * mm, "end": v(-384.2, -7099.23) * mm});
            skLineSegment(sketch, "E2049", {"start": v(-384.2, -7099.23) * mm, "end": v(-367.6, -7115.54) * mm});
            skLineSegment(sketch, "E2050", {"start": v(-367.6, -7115.54) * mm, "end": v(-348.86, -7129.4) * mm});
            skLineSegment(sketch, "E2051", {"start": v(-348.86, -7129.4) * mm, "end": v(-328.26, -7140.56) * mm});
            skLineSegment(sketch, "E2052", {"start": v(-328.26, -7140.56) * mm, "end": v(-298.42, -7313.77) * mm});
            skLineSegment(sketch, "E2053", {"start": v(-298.42, -7313.77) * mm, "end": v(-276.14, -7446.16) * mm});
            skLineSegment(sketch, "E2054", {"start": v(-276.14, -7446.16) * mm, "end": v(-260.5, -7546) * mm});
            skLineSegment(sketch, "E2055", {"start": v(-260.5, -7546) * mm, "end": v(-250.58, -7621.58) * mm});
            skLineSegment(sketch, "E2056", {"start": v(-250.58, -7621.58) * mm, "end": v(-245.46, -7681.16) * mm});
            skLineSegment(sketch, "E2057", {"start": v(-245.46, -7681.16) * mm, "end": v(-244.22, -7733.02) * mm});
            skLineSegment(sketch, "E2058", {"start": v(-244.22, -7733.02) * mm, "end": v(-245.94, -7785.44) * mm});
            skLineSegment(sketch, "E2059", {"start": v(-245.94, -7785.44) * mm, "end": v(-249.7, -7846.68) * mm});
            skLineSegment(sketch, "E2060", {"start": v(-249.7, -7846.68) * mm, "end": v(-263.38, -7952.29) * mm});
            skLineSegment(sketch, "E2061", {"start": v(-263.38, -7952.29) * mm, "end": v(-285.02, -8083.83) * mm});
            skLineSegment(sketch, "E2062", {"start": v(-285.02, -8083.83) * mm, "end": v(-304.83, -8229.55) * mm});
            skLineSegment(sketch, "E2063", {"start": v(-304.83, -8229.55) * mm, "end": v(-313.05, -8377.7) * mm});
            skLineSegment(sketch, "E2064", {"start": v(-313.05, -8377.7) * mm, "end": v(-299.9, -8516.5) * mm});
            skLineSegment(sketch, "E2065", {"start": v(-299.9, -8516.5) * mm, "end": v(-255.62, -8634.2) * mm});
            skLineSegment(sketch, "E2066", {"start": v(-255.62, -8634.2) * mm, "end": v(-170.4, -8719.05) * mm});
            skLineSegment(sketch, "E2067", {"start": v(-170.4, -8719.05) * mm, "end": v(-34.5, -8759.28) * mm});
            skLineSegment(sketch, "E2068", {"start": v(-34.5, -8759.28) * mm, "end": v(128.6, -8733.48) * mm});
            skLineSegment(sketch, "E2069", {"start": v(128.6, -8733.48) * mm, "end": v(233.47, -8662.67) * mm});
            skLineSegment(sketch, "E2070", {"start": v(233.47, -8662.67) * mm, "end": v(290.99, -8556.74) * mm});
            skLineSegment(sketch, "E2071", {"start": v(290.99, -8556.74) * mm, "end": v(312.07, -8425.6) * mm});
            skLineSegment(sketch, "E2072", {"start": v(312.07, -8425.6) * mm, "end": v(307.6, -8279.12) * mm});
            skLineSegment(sketch, "E2073", {"start": v(307.6, -8279.12) * mm, "end": v(288.49, -8127.22) * mm});
            skLineSegment(sketch, "E2074", {"start": v(288.49, -8127.22) * mm, "end": v(265.63, -7979.77) * mm});
            skLineSegment(sketch, "E2075", {"start": v(265.63, -7979.77) * mm, "end": v(249.92, -7846.68) * mm});
            skLineSegment(sketch, "E2076", {"start": v(249.92, -7846.68) * mm, "end": v(249.76, -7761.7) * mm});
            skLineSegment(sketch, "E2077", {"start": v(249.76, -7761.7) * mm, "end": v(256.98, -7656.05) * mm});
            skLineSegment(sketch, "E2078", {"start": v(256.98, -7656.05) * mm, "end": v(269.3, -7539.61) * mm});
            skLineSegment(sketch, "E2079", {"start": v(269.3, -7539.61) * mm, "end": v(284.46, -7422.24) * mm});
            skLineSegment(sketch, "E2080", {"start": v(284.46, -7422.24) * mm, "end": v(300.2, -7313.8) * mm});
            skLineSegment(sketch, "E2081", {"start": v(300.2, -7313.8) * mm, "end": v(314.25, -7224.13) * mm});
            skLineSegment(sketch, "E2082", {"start": v(314.25, -7224.13) * mm, "end": v(324.34, -7163.1) * mm});
            skLineSegment(sketch, "E2083", {"start": v(324.34, -7163.1) * mm, "end": v(328.2, -7140.56) * mm});
            skLineSegment(sketch, "E2084", {"start": v(328.2, -7140.56) * mm, "end": v(348.89, -7129.4) * mm});
            skLineSegment(sketch, "E2085", {"start": v(348.89, -7129.4) * mm, "end": v(367.67, -7115.54) * mm});
            skLineSegment(sketch, "E2086", {"start": v(367.67, -7115.54) * mm, "end": v(384.28, -7099.23) * mm});
            skLineSegment(sketch, "E2087", {"start": v(384.28, -7099.23) * mm, "end": v(398.46, -7080.73) * mm});
            skLineSegment(sketch, "E2088", {"start": v(398.46, -7080.73) * mm, "end": v(409.94, -7060.3) * mm});
            skLineSegment(sketch, "E2089", {"start": v(409.94, -7060.3) * mm, "end": v(418.47, -7038.18) * mm});
            skLineSegment(sketch, "E2090", {"start": v(418.47, -7038.18) * mm, "end": v(423.79, -7014.64) * mm});
            skLineSegment(sketch, "E2091", {"start": v(423.79, -7014.64) * mm, "end": v(425.62, -6989.94) * mm});
            skLineSegment(sketch, "E2092", {"start": v(425.62, -6989.94) * mm, "end": v(425.62, -6815.82) * mm});
            skLineSegment(sketch, "E2093", {"start": v(425.62, -6815.82) * mm, "end": v(1005.65, -6755.32) * mm});
            skLineSegment(sketch, "E2094", {"start": v(1005.65, -6755.32) * mm, "end": v(1570.2, -6647.45) * mm});
            skLineSegment(sketch, "E2095", {"start": v(1570.2, -6647.45) * mm, "end": v(2117.23, -6494.25) * mm});
            skLineSegment(sketch, "E2096", {"start": v(2117.23, -6494.25) * mm, "end": v(2644.7, -6297.78) * mm});
            skLineSegment(sketch, "E2097", {"start": v(2644.7, -6297.78) * mm, "end": v(3150.58, -6060.1) * mm});
            skLineSegment(sketch, "E2098", {"start": v(3150.58, -6060.1) * mm, "end": v(3632.82, -5783.23) * mm});
            skLineSegment(sketch, "E2099", {"start": v(3632.82, -5783.23) * mm, "end": v(4089.38, -5469.25) * mm});
            skLineSegment(sketch, "E2100", {"start": v(4089.38, -5469.25) * mm, "end": v(4518.22, -5120.2) * mm});
            skLineSegment(sketch, "E2101", {"start": v(4518.22, -5120.2) * mm, "end": v(4641.63, -5243.61) * mm});
            skLineSegment(sketch, "E2102", {"start": v(4641.63, -5243.61) * mm, "end": v(4660.4, -5259.78) * mm});
            skLineSegment(sketch, "E2103", {"start": v(4660.4, -5259.78) * mm, "end": v(4680.83, -5272.65) * mm});
            skLineSegment(sketch, "E2104", {"start": v(4680.83, -5272.65) * mm, "end": v(4702.52, -5282.23) * mm});
            skLineSegment(sketch, "E2105", {"start": v(4702.52, -5282.23) * mm, "end": v(4725.12, -5288.53) * mm});
            skLineSegment(sketch, "E2106", {"start": v(4725.12, -5288.53) * mm, "end": v(4748.25, -5291.57) * mm});
            skLineSegment(sketch, "E2107", {"start": v(4748.25, -5291.57) * mm, "end": v(4771.53, -5291.36) * mm});
            skLineSegment(sketch, "E2108", {"start": v(4771.53, -5291.36) * mm, "end": v(4794.58, -5287.9) * mm});
            skLineSegment(sketch, "E2109", {"start": v(4794.58, -5287.9) * mm, "end": v(4817.05, -5281.23) * mm});
            skLineSegment(sketch, "E2110", {"start": v(4817.05, -5281.23) * mm, "end": v(4960.61, -5382.62) * mm});
            skLineSegment(sketch, "E2111", {"start": v(4960.61, -5382.62) * mm, "end": v(5069.97, -5460.49) * mm});
            skLineSegment(sketch, "E2112", {"start": v(5069.97, -5460.49) * mm, "end": v(5151.63, -5520.04) * mm});
            skLineSegment(sketch, "E2113", {"start": v(5151.63, -5520.04) * mm, "end": v(5212.08, -5566.46) * mm});
            skLineSegment(sketch, "E2114", {"start": v(5212.08, -5566.46) * mm, "end": v(5257.83, -5604.97) * mm});
            skLineSegment(sketch, "E2115", {"start": v(5257.83, -5604.97) * mm, "end": v(5295.38, -5640.77) * mm});
            skLineSegment(sketch, "E2116", {"start": v(5295.38, -5640.77) * mm, "end": v(5331.23, -5679.04) * mm});
            skLineSegment(sketch, "E2117", {"start": v(5331.23, -5679.04) * mm, "end": v(5371.88, -5725) * mm});
            skLineSegment(sketch, "E2118", {"start": v(5371.88, -5725) * mm, "end": v(5436.89, -5809.35) * mm});
            skLineSegment(sketch, "E2119", {"start": v(5436.89, -5809.35) * mm, "end": v(5514.6, -5917.66) * mm});
            skLineSegment(sketch, "E2120", {"start": v(5514.6, -5917.66) * mm, "end": v(5603.63, -6034.72) * mm});
            skLineSegment(sketch, "E2121", {"start": v(5603.63, -6034.72) * mm, "end": v(5702.57, -6145.28) * mm});
            skLineSegment(sketch, "E2122", {"start": v(5702.57, -6145.28) * mm, "end": v(5810, -6234.13) * mm});
            skLineSegment(sketch, "E2123", {"start": v(5810, -6234.13) * mm, "end": v(5924.55, -6286.04) * mm});
            skLineSegment(sketch, "E2124", {"start": v(5924.55, -6286.04) * mm, "end": v(6044.8, -6285.79) * mm});
            skLineSegment(sketch, "E2125", {"start": v(6044.8, -6285.79) * mm, "end": v(6169.34, -6218.14) * mm});
            skLineSegment(sketch, "E2126", {"start": v(6169.34, -6218.14) * mm, "end": v(6266.44, -6084.56) * mm});
            skLineSegment(sketch, "E2127", {"start": v(6266.44, -6084.56) * mm, "end": v(6290.52, -5960.34) * mm});
            skLineSegment(sketch, "E2128", {"start": v(6290.52, -5960.34) * mm, "end": v(6256.3, -5844.76) * mm});
            skLineSegment(sketch, "E2129", {"start": v(6256.3, -5844.76) * mm, "end": v(6178.47, -5737.12) * mm});
            skLineSegment(sketch, "E2130", {"start": v(6178.47, -5737.12) * mm, "end": v(6071.74, -5636.7) * mm});
            skLineSegment(sketch, "E2131", {"start": v(6071.74, -5636.7) * mm, "end": v(5950.8, -5542.8) * mm});
            skLineSegment(sketch, "E2132", {"start": v(5950.8, -5542.8) * mm, "end": v(5830.39, -5454.71) * mm});
            skLineSegment(sketch, "E2133", {"start": v(5830.39, -5454.71) * mm, "end": v(5725.17, -5371.7) * mm});
            skLineSegment(sketch, "E2134", {"start": v(5725.17, -5371.7) * mm, "end": v(5664.97, -5311.73) * mm});
            skLineSegment(sketch, "E2135", {"start": v(5664.97, -5311.73) * mm, "end": v(5595.37, -5231.93) * mm});
            skLineSegment(sketch, "E2136", {"start": v(5595.37, -5231.93) * mm, "end": v(5521.75, -5140.89) * mm});
            skLineSegment(sketch, "E2137", {"start": v(5521.75, -5140.89) * mm, "end": v(5449.48, -5047.17) * mm});
            skLineSegment(sketch, "E2138", {"start": v(5449.48, -5047.17) * mm, "end": v(5383.92, -4959.36) * mm});
            skLineSegment(sketch, "E2139", {"start": v(5383.92, -4959.36) * mm, "end": v(5330.45, -4886.03) * mm});
            skLineSegment(sketch, "E2140", {"start": v(5330.45, -4886.03) * mm, "end": v(5294.43, -4835.74) * mm});
            skLineSegment(sketch, "E2141", {"start": v(5294.43, -4835.74) * mm, "end": v(5281.23, -4817.07) * mm});
            skLineSegment(sketch, "E2142", {"start": v(5281.23, -4817.07) * mm, "end": v(5287.96, -4794.55) * mm});
            skLineSegment(sketch, "E2143", {"start": v(5287.96, -4794.55) * mm, "end": v(5291.43, -4771.47) * mm});
            skLineSegment(sketch, "E2144", {"start": v(5291.43, -4771.47) * mm, "end": v(5291.64, -4748.2) * mm});
            skLineSegment(sketch, "E2145", {"start": v(5291.64, -4748.2) * mm, "end": v(5288.58, -4725.08) * mm});
            skLineSegment(sketch, "E2146", {"start": v(5288.58, -4725.08) * mm, "end": v(5282.26, -4702.51) * mm});
            skLineSegment(sketch, "E2147", {"start": v(5282.26, -4702.51) * mm, "end": v(5272.65, -4680.84) * mm});
            skLineSegment(sketch, "E2148", {"start": v(5272.65, -4680.84) * mm, "end": v(5259.76, -4660.45) * mm});
            skLineSegment(sketch, "E2149", {"start": v(5259.76, -4660.45) * mm, "end": v(5243.59, -4641.68) * mm});
            skLineSegment(sketch, "E2150", {"start": v(5243.59, -4641.68) * mm, "end": v(5120.17, -4518.24) * mm});
            skLineSegment(sketch, "E2151", {"start": v(5120.17, -4518.24) * mm, "end": v(5469.18, -4089.4) * mm});
            skLineSegment(sketch, "E2152", {"start": v(5469.18, -4089.4) * mm, "end": v(5783.12, -3632.85) * mm});
            skLineSegment(sketch, "E2153", {"start": v(5783.12, -3632.85) * mm, "end": v(6059.96, -3150.61) * mm});
            skLineSegment(sketch, "E2154", {"start": v(6059.96, -3150.61) * mm, "end": v(6297.63, -2644.74) * mm});
            skLineSegment(sketch, "E2155", {"start": v(6297.63, -2644.74) * mm, "end": v(6494.08, -2117.27) * mm});
            skLineSegment(sketch, "E2156", {"start": v(6494.08, -2117.27) * mm, "end": v(6647.27, -1570.24) * mm});
            skLineSegment(sketch, "E2157", {"start": v(6647.27, -1570.24) * mm, "end": v(6755.14, -1005.7) * mm});
            skLineSegment(sketch, "E2158", {"start": v(6755.14, -1005.7) * mm, "end": v(6815.65, -425.67) * mm});
            skLineSegment(sketch, "E2159", {"start": v(6815.65, -425.67) * mm, "end": v(6989.94, -425.67) * mm});
            skLineSegment(sketch, "E2160", {"start": v(6989.94, -425.67) * mm, "end": v(7014.64, -423.83) * mm});
            skLineSegment(sketch, "E2161", {"start": v(7014.64, -423.83) * mm, "end": v(7038.18, -418.49) * mm});
            skLineSegment(sketch, "E2162", {"start": v(7038.18, -418.49) * mm, "end": v(7060.3, -409.92) * mm});
            skLineSegment(sketch, "E2163", {"start": v(7060.3, -409.92) * mm, "end": v(7080.73, -398.4) * mm});
            skLineSegment(sketch, "E2164", {"start": v(7080.73, -398.4) * mm, "end": v(7099.23, -384.2) * mm});
            skLineSegment(sketch, "E2165", {"start": v(7099.23, -384.2) * mm, "end": v(7115.54, -367.59) * mm});
            skLineSegment(sketch, "E2166", {"start": v(7115.54, -367.59) * mm, "end": v(7129.4, -348.84) * mm});
            skLineSegment(sketch, "E2167", {"start": v(7129.4, -348.84) * mm, "end": v(7140.56, -328.23) * mm});
            skLineSegment(sketch, "E2168", {"start": v(7140.56, -328.23) * mm, "end": v(7313.78, -298.4) * mm});
            skLineSegment(sketch, "E2169", {"start": v(7313.78, -298.4) * mm, "end": v(7446.18, -276.13) * mm});
            skLineSegment(sketch, "E2170", {"start": v(7446.18, -276.13) * mm, "end": v(7546.02, -260.5) * mm});
            skLineSegment(sketch, "E2171", {"start": v(7546.02, -260.5) * mm, "end": v(7621.6, -250.58) * mm});
            skLineSegment(sketch, "E2172", {"start": v(7621.6, -250.58) * mm, "end": v(7681.18, -245.46) * mm});
            skLineSegment(sketch, "E2173", {"start": v(7681.18, -245.46) * mm, "end": v(7733.04, -244.22) * mm});
            skLineSegment(sketch, "E2174", {"start": v(7733.04, -244.22) * mm, "end": v(7785.45, -245.94) * mm});
            skLineSegment(sketch, "E2175", {"start": v(7785.45, -245.94) * mm, "end": v(7846.68, -249.7) * mm});
            skLineSegment(sketch, "E2176", {"start": v(7846.68, -249.7) * mm, "end": v(7952.29, -263.37) * mm});
            skLineSegment(sketch, "E2177", {"start": v(7952.29, -263.37) * mm, "end": v(8083.83, -285) * mm});
            skLineSegment(sketch, "E2178", {"start": v(8083.83, -285) * mm, "end": v(8229.55, -304.81) * mm});
            skLineSegment(sketch, "E2179", {"start": v(8229.55, -304.81) * mm, "end": v(8377.7, -313.04) * mm});
            skLineSegment(sketch, "E2180", {"start": v(8377.7, -313.04) * mm, "end": v(8516.5, -299.89) * mm});
            skLineSegment(sketch, "E2181", {"start": v(8516.5, -299.89) * mm, "end": v(8634.2, -255.6) * mm});
            skLineSegment(sketch, "E2182", {"start": v(8634.2, -255.6) * mm, "end": v(8719.05, -170.4) * mm});
            skLineSegment(sketch, "E2183", {"start": v(8719.05, -170.4) * mm, "end": v(8759.28, -34.5) * mm});
            skLineSegment(sketch, "E2184", {"start": v(8759.28, -34.5) * mm, "end": v(8733.48, 128.6) * mm});
            skLineSegment(sketch, "E2185", {"start": v(8733.48, 128.6) * mm, "end": v(8662.67, 233.48) * mm});
            skLineSegment(sketch, "E2186", {"start": v(8662.67, 233.48) * mm, "end": v(8556.74, 291) * mm});
            skLineSegment(sketch, "E2187", {"start": v(8556.74, 291) * mm, "end": v(8425.6, 312.08) * mm});
            skLineSegment(sketch, "E2188", {"start": v(8425.6, 312.08) * mm, "end": v(8279.12, 307.61) * mm});
            skLineSegment(sketch, "E2189", {"start": v(8279.12, 307.61) * mm, "end": v(8127.22, 288.5) * mm});
            skLineSegment(sketch, "E2190", {"start": v(8127.22, 288.5) * mm, "end": v(7979.77, 265.65) * mm});
            skLineSegment(sketch, "E2191", {"start": v(7979.77, 265.65) * mm, "end": v(7846.68, 249.95) * mm});
            skSolve(sketch);
        }
        {
            var Q0;
            Q0=makeQuery(id+"F0.imprint","IMPRINT",FACE,{"disambiguationData":[TD([[makeQuery(id+"F0.imprint","IMPRINT",EDGE,{"derivedFrom":sQuery(id+"F0.wireOp",EDGE,"E0")}),1.0]])]});
            extrude(context, id + "F1", {"entities" : qUnion([Q0]), "depth" : 254 * mm, "offsetDistance" : 25.4 * mm});
        }
    });
